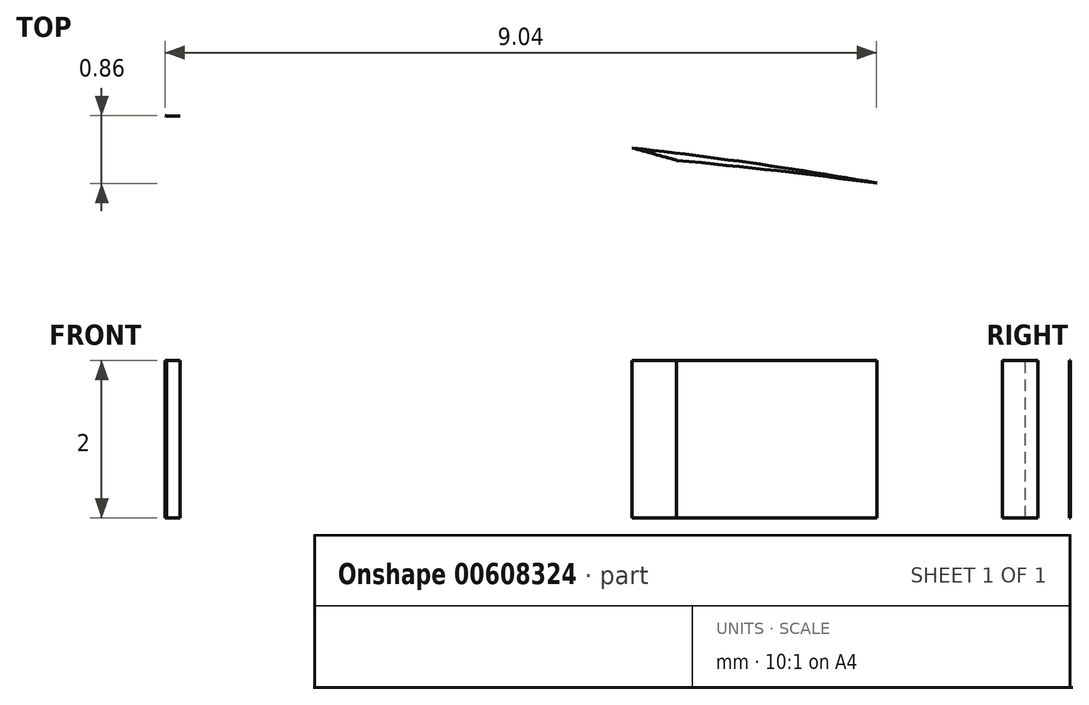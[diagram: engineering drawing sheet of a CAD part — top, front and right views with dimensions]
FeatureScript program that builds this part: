
annotation { "Feature Type Name" : "Feature", "Feature Type Description" : "" }
export const myFeature = defineFeature(function(context is Context, id is Id, definition is map)
    precondition{}
    {
        {
            var Q0;
            Q0=qCreatedBy(makeId("Top.planeOp"),FACE);
            var sketch = newSketch(context, id + "F0", { "sketchPlane" : qUnion([Q0])});
            skFitSpline(sketch, "E0", {"points": [v(-12.37, -64.8) * mm, v(-14.42, -64.57) * mm, v(-15.26, -64.38) * mm, v(-16.13, -63.98) * mm]});
            skFitSpline(sketch, "E1", {"points": [v(-16.13, -63.98) * mm, v(-17.35, -63.42) * mm, v(-19.53, -61.11) * mm, v(-21, -58.82) * mm]});
            skFitSpline(sketch, "E2", {"points": [v(-21, -58.82) * mm, v(-21.68, -57.77) * mm, v(-24.63, -53.13) * mm, v(-27.56, -48.51) * mm]});
            skFitSpline(sketch, "E3", {"points": [v(-33.46, -32.34) * mm, v(-34.25, -21.46) * mm, v(-34.5, -18.5) * mm, v(-34.87, -16.5) * mm]});
            skFitSpline(sketch, "E4", {"points": [v(-34.87, -16.5) * mm, v(-35.26, -14.33) * mm, v(-35.89, -11.88) * mm, v(-36.54, -9.98) * mm]});
            skFitSpline(sketch, "E5", {"points": [v(-36.54, -9.98) * mm, v(-36.87, -9.01) * mm, v(-37.03, -8.22) * mm, v(-37.03, -7.54) * mm]});
            skFitSpline(sketch, "E6", {"points": [v(-37.03, -7.54) * mm, v(-37.03, -6.71) * mm, v(-37.14, -6.31) * mm, v(-37.6, -5.39) * mm]});
            skFitSpline(sketch, "E7", {"points": [v(-37.6, -5.39) * mm, v(-39.55, -1.57) * mm, v(-40.93, 5.83) * mm, v(-40.92, 12.33) * mm]});
            skFitSpline(sketch, "E8", {"points": [v(-40.92, 12.33) * mm, v(-40.92, 15.03) * mm, v(-40.86, 15.87) * mm, v(-40.56, 17.29) * mm]});
            skFitSpline(sketch, "E9", {"points": [v(-40.56, 17.29) * mm, v(-39.91, 20.3) * mm, v(-39, 22.4) * mm, v(-37.7, 23.92) * mm]});
            skLineSegment(sketch, "E10", {"start": v(-27.56, -48.51) * mm, "end": v(-32.9, -40.1) * mm});
            skLineSegment(sketch, "E11", {"start": v(-32.9, -40.1) * mm, "end": v(-33.46, -32.34) * mm});
            skFitSpline(sketch, "E12", {"points": [v(-36.97, 26.7) * mm, v(-36.91, 27.82) * mm, v(-36.79, 32.12) * mm, v(-36.7, 36.25) * mm]});
            skFitSpline(sketch, "E13", {"points": [v(-36.7, 36.25) * mm, v(-36.5, 44.48) * mm, v(-36.48, 44.88) * mm, v(-36.03, 46.58) * mm]});
            skFitSpline(sketch, "E14", {"points": [v(-36.03, 46.58) * mm, v(-34, 54.2) * mm, v(-25.6, 60.7) * mm, v(-14.03, 63.58) * mm]});
            skFitSpline(sketch, "E15", {"points": [v(-14.03, 63.58) * mm, v(-9.87, 64.61) * mm, v(-6.05, 65) * mm, v(0.05, 65) * mm]});
            skFitSpline(sketch, "E16", {"points": [v(0.05, 65) * mm, v(7.64, 65) * mm, v(12.07, 64.37) * mm, v(17.71, 62.49) * mm]});
            skFitSpline(sketch, "E17", {"points": [v(17.71, 62.49) * mm, v(23.1, 60.7) * mm, v(27.42, 58.2) * mm, v(30.77, 54.93) * mm]});
            skFitSpline(sketch, "E18", {"points": [v(30.77, 54.93) * mm, v(33.12, 52.64) * mm, v(34.58, 50.51) * mm, v(35.53, 47.98) * mm]});
            skFitSpline(sketch, "E19", {"points": [v(35.53, 47.98) * mm, v(36.33, 45.85) * mm, v(36.44, 44.7) * mm, v(36.63, 36.91) * mm]});
            skFitSpline(sketch, "E20", {"points": [v(36.63, 36.91) * mm, v(36.72, 32.88) * mm, v(36.84, 28.48) * mm, v(36.9, 27.14) * mm]});
            skLineSegment(sketch, "E21", {"start": v(-37.7, 23.92) * mm, "end": v(-37.07, 24.64) * mm});
            skLineSegment(sketch, "E22", {"start": v(-37.07, 24.64) * mm, "end": v(-36.97, 26.7) * mm});
            skFitSpline(sketch, "E23", {"points": [v(37.74, 23.8) * mm, v(40.15, 20.9) * mm, v(41.27, 15.81) * mm, v(40.83, 9.7) * mm]});
            skFitSpline(sketch, "E24", {"points": [v(40.83, 9.7) * mm, v(40.37, 3.3) * mm, v(39.2, -2.14) * mm, v(37.55, -5.4) * mm]});
            skFitSpline(sketch, "E25", {"points": [v(37.55, -5.4) * mm, v(37.07, -6.35) * mm, v(36.96, -6.75) * mm, v(36.96, -7.58) * mm]});
            skFitSpline(sketch, "E26", {"points": [v(36.96, -7.58) * mm, v(36.96, -8.28) * mm, v(36.8, -9.07) * mm, v(36.46, -10.1) * mm]});
            skFitSpline(sketch, "E27", {"points": [v(36.46, -10.1) * mm, v(35.83, -11.95) * mm, v(35.07, -14.94) * mm, v(34.73, -16.92) * mm]});
            skFitSpline(sketch, "E28", {"points": [v(34.73, -16.92) * mm, v(34.48, -18.3) * mm, v(33.93, -24.93) * mm, v(33.16, -35.76) * mm]});
            skLineSegment(sketch, "E29", {"start": v(36.9, 27.14) * mm, "end": v(37, 24.7) * mm});
            skLineSegment(sketch, "E30", {"start": v(37, 24.7) * mm, "end": v(37.74, 23.8) * mm});
            skFitSpline(sketch, "E31", {"points": [v(27.67, -48.26) * mm, v(19.52, -61.11) * mm, v(19.87, -60.6) * mm, v(18.22, -62.25) * mm]});
            skFitSpline(sketch, "E32", {"points": [v(18.22, -62.25) * mm, v(16.5, -63.98) * mm, v(15.65, -64.4) * mm, v(13.38, -64.7) * mm]});
            skFitSpline(sketch, "E33", {"points": [v(13.38, -64.7) * mm, v(11.7, -64.91) * mm, v(-10.67, -65) * mm, v(-12.37, -64.8) * mm]});
            skLineSegment(sketch, "E34", {"start": v(33.16, -35.76) * mm, "end": v(32.84, -40.1) * mm});
            skLineSegment(sketch, "E35", {"start": v(32.84, -40.1) * mm, "end": v(27.67, -48.26) * mm});
            skFitSpline(sketch, "E36", {"points": [v(11.8, -61.94) * mm, v(14.15, -61.52) * mm, v(14.92, -61.22) * mm, v(15.85, -60.35) * mm]});
            skFitSpline(sketch, "E37", {"points": [v(15.85, -60.35) * mm, v(17, -59.27) * mm, v(17.39, -58.7) * mm, v(23.96, -48.34) * mm]});
            skFitSpline(sketch, "E38", {"points": [v(30.23, -33.5) * mm, v(30.46, -30.43) * mm, v(30.74, -26.57) * mm, v(30.87, -24.92) * mm]});
            skFitSpline(sketch, "E39", {"points": [v(30.87, -24.92) * mm, v(31, -23.27) * mm, v(31.08, -21.9) * mm, v(31.06, -21.87) * mm]});
            skFitSpline(sketch, "E40", {"points": [v(31.06, -21.87) * mm, v(31.03, -21.85) * mm, v(30.73, -22.29) * mm, v(30.39, -22.85) * mm]});
            skFitSpline(sketch, "E41", {"points": [v(30.39, -22.85) * mm, v(30.04, -23.4) * mm, v(28.89, -25.08) * mm, v(27.83, -26.56) * mm]});
            skFitSpline(sketch, "E42", {"points": [v(27.83, -26.56) * mm, v(24.27, -31.52) * mm, v(22.79, -34.32) * mm, v(20.88, -39.66) * mm]});
            skLineSegment(sketch, "E43", {"start": v(23.96, -48.34) * mm, "end": v(29.83, -39.1) * mm});
            skLineSegment(sketch, "E44", {"start": v(29.83, -39.1) * mm, "end": v(30.23, -33.5) * mm});
            skFitSpline(sketch, "E45", {"points": [v(20.7, -43.9) * mm, v(20.94, -45.29) * mm, v(21.14, -46.67) * mm, v(21.14, -46.98) * mm]});
            skFitSpline(sketch, "E46", {"points": [v(21.14, -46.98) * mm, v(21.13, -48) * mm, v(18.6, -53.5) * mm, v(17.35, -55.2) * mm]});
            skFitSpline(sketch, "E47", {"points": [v(17.35, -55.2) * mm, v(16.02, -57.02) * mm, v(14.23, -57.14) * mm, v(9.94, -55.72) * mm]});
            skFitSpline(sketch, "E48", {"points": [v(9.94, -55.72) * mm, v(9.7, -55.65) * mm, v(9.57, -55.9) * mm, v(9.2, -57.09) * mm]});
            skFitSpline(sketch, "E49", {"points": [v(9.2, -57.09) * mm, v(8.95, -57.94) * mm, v(8.6, -58.71) * mm, v(8.37, -58.94) * mm]});
            skLineSegment(sketch, "E50", {"start": v(20.88, -39.66) * mm, "end": v(20.26, -41.4) * mm});
            skLineSegment(sketch, "E51", {"start": v(20.26, -41.4) * mm, "end": v(20.7, -43.9) * mm});
            skFitSpline(sketch, "E52", {"points": [v(-8.42, -58.95) * mm, v(-8.63, -58.74) * mm, v(-9, -57.92) * mm, v(-9.26, -57.1) * mm]});
            skFitSpline(sketch, "E53", {"points": [v(-9.26, -57.1) * mm, v(-9.64, -55.9) * mm, v(-9.77, -55.65) * mm, v(-10, -55.72) * mm]});
            skFitSpline(sketch, "E54", {"points": [v(-10, -55.72) * mm, v(-12.14, -56.43) * mm, v(-13.2, -56.66) * mm, v(-14.3, -56.66) * mm]});
            skFitSpline(sketch, "E55", {"points": [v(-14.3, -56.66) * mm, v(-15.94, -56.66) * mm, v(-16.64, -56.3) * mm, v(-17.5, -55.04) * mm]});
            skFitSpline(sketch, "E56", {"points": [v(-17.5, -55.04) * mm, v(-18.27, -53.9) * mm, v(-19.78, -50.93) * mm, v(-20.63, -48.9) * mm]});
            skFitSpline(sketch, "E57", {"points": [v(-20.63, -48.9) * mm, v(-21.32, -47.22) * mm, v(-21.32, -47.02) * mm, v(-20.7, -43.5) * mm]});
            skLineSegment(sketch, "E58", {"start": v(8.37, -58.94) * mm, "end": v(7.98, -59.33) * mm});
            skLineSegment(sketch, "E59", {"start": v(7.98, -59.33) * mm, "end": v(-0.03, -59.33) * mm});
            skLineSegment(sketch, "E60", {"start": v(-0.03, -59.33) * mm, "end": v(-8.05, -59.33) * mm});
            skLineSegment(sketch, "E61", {"start": v(-8.05, -59.33) * mm, "end": v(-8.42, -58.95) * mm});
            skFitSpline(sketch, "E62", {"points": [v(-21.19, -38.91) * mm, v(-22.53, -35.33) * mm, v(-24.6, -31.2) * mm, v(-26.06, -29.25) * mm]});
            skFitSpline(sketch, "E63", {"points": [v(-26.06, -29.25) * mm, v(-26.74, -28.33) * mm, v(-28.15, -26.3) * mm, v(-29.2, -24.72) * mm]});
            skFitSpline(sketch, "E64", {"points": [v(-29.2, -24.72) * mm, v(-30.25, -23.14) * mm, v(-31.11, -21.86) * mm, v(-31.13, -21.88) * mm]});
            skFitSpline(sketch, "E65", {"points": [v(-31.13, -21.88) * mm, v(-31.24, -22.03) * mm, v(-29.85, -39.05) * mm, v(-29.7, -39.33) * mm]});
            skFitSpline(sketch, "E66", {"points": [v(-29.7, -39.33) * mm, v(-29.45, -39.8) * mm, v(-18.29, -57.39) * mm, v(-17.67, -58.29) * mm]});
            skFitSpline(sketch, "E67", {"points": [v(-17.67, -58.29) * mm, v(-17.4, -58.67) * mm, v(-16.77, -59.44) * mm, v(-16.27, -59.99) * mm]});
            skFitSpline(sketch, "E68", {"points": [v(-16.27, -59.99) * mm, v(-15.16, -61.18) * mm, v(-14.38, -61.51) * mm, v(-11.86, -61.9) * mm]});
            skFitSpline(sketch, "E69", {"points": [v(-11.86, -61.9) * mm, v(-9.22, -62.3) * mm, v(-9.42, -62.29) * mm, v(0.72, -62.25) * mm]});
            skFitSpline(sketch, "E70", {"points": [v(0.72, -62.25) * mm, v(8.81, -62.23) * mm, v(10.45, -62.18) * mm, v(11.8, -61.94) * mm]});
            skLineSegment(sketch, "E71", {"start": v(-20.7, -43.5) * mm, "end": v(-20.32, -41.25) * mm});
            skLineSegment(sketch, "E72", {"start": v(-20.32, -41.25) * mm, "end": v(-21.19, -38.91) * mm});
            skFitSpline(sketch, "E73", {"points": [v(6.4, -55.75) * mm, v(6.52, -55.43) * mm, v(6.63, -55.13) * mm, v(6.63, -55.09) * mm]});
            skFitSpline(sketch, "E74", {"points": [v(6.63, -55.09) * mm, v(6.63, -55.04) * mm, v(3.64, -55) * mm, v(-0.02, -55) * mm]});
            skFitSpline(sketch, "E75", {"points": [v(-6.53, -55.5) * mm, v(-6.46, -55.76) * mm, v(-6.34, -56.06) * mm, v(-6.29, -56.16) * mm]});
            skFitSpline(sketch, "E76", {"points": [v(-6.29, -56.16) * mm, v(-6.22, -56.27) * mm, v(-4.07, -56.33) * mm, v(-0.01, -56.33) * mm]});
            skLineSegment(sketch, "E77", {"start": v(-0.02, -55) * mm, "end": v(-6.68, -55) * mm});
            skLineSegment(sketch, "E78", {"start": v(-6.68, -55) * mm, "end": v(-6.53, -55.5) * mm});
            skFitSpline(sketch, "E79", {"points": [v(-12.22, -53.17) * mm, v(-11.45, -52.9) * mm, v(-10.75, -52.61) * mm, v(-10.66, -52.52) * mm]});
            skFitSpline(sketch, "E80", {"points": [v(-10.66, -52.52) * mm, v(-10.49, -52.35) * mm, v(-11.45, -48.42) * mm, v(-11.74, -48.08) * mm]});
            skFitSpline(sketch, "E81", {"points": [v(-11.74, -48.08) * mm, v(-11.83, -47.98) * mm, v(-12.1, -48.17) * mm, v(-12.46, -48.61) * mm]});
            skFitSpline(sketch, "E82", {"points": [v(-12.46, -48.61) * mm, v(-13.19, -49.48) * mm, v(-14, -50) * mm, v(-14.66, -50) * mm]});
            skFitSpline(sketch, "E83", {"points": [v(-14.66, -50) * mm, v(-15.3, -50) * mm, v(-15.83, -49.4) * mm, v(-16.95, -47.46) * mm]});
            skFitSpline(sketch, "E84", {"points": [v(-16.95, -47.46) * mm, v(-17.4, -46.65) * mm, v(-17.83, -46) * mm, v(-17.89, -46) * mm]});
            skFitSpline(sketch, "E85", {"points": [v(-17.89, -46) * mm, v(-18.42, -46) * mm, v(-17.67, -48.27) * mm, v(-16.13, -51.33) * mm]});
            skFitSpline(sketch, "E86", {"points": [v(-16.13, -51.33) * mm, v(-15.13, -53.31) * mm, v(-14.84, -53.66) * mm, v(-14.2, -53.66) * mm]});
            skFitSpline(sketch, "E87", {"points": [v(-14.2, -53.66) * mm, v(-13.88, -53.66) * mm, v(-12.99, -53.44) * mm, v(-12.22, -53.17) * mm]});
            skLineSegment(sketch, "E88", {"start": v(-0.01, -56.33) * mm, "end": v(6.15, -56.33) * mm});
            skLineSegment(sketch, "E89", {"start": v(6.15, -56.33) * mm, "end": v(6.4, -55.75) * mm});
            skFitSpline(sketch, "E90", {"points": [v(15.16, -52.96) * mm, v(16.4, -50.95) * mm, v(18.16, -46.9) * mm, v(18.02, -46.36) * mm]});
            skFitSpline(sketch, "E91", {"points": [v(18.02, -46.36) * mm, v(17.97, -46.16) * mm, v(17.88, -46) * mm, v(17.82, -46) * mm]});
            skFitSpline(sketch, "E92", {"points": [v(17.82, -46) * mm, v(17.76, -46) * mm, v(17.35, -46.65) * mm, v(16.9, -47.43) * mm]});
            skFitSpline(sketch, "E93", {"points": [v(16.9, -47.43) * mm, v(15.79, -49.4) * mm, v(15.24, -50) * mm, v(14.56, -50) * mm]});
            skFitSpline(sketch, "E94", {"points": [v(14.56, -50) * mm, v(13.97, -50) * mm, v(13.06, -49.38) * mm, v(12.27, -48.44) * mm]});
            skFitSpline(sketch, "E95", {"points": [v(12.27, -48.44) * mm, v(11.98, -48.1) * mm, v(11.77, -47.97) * mm, v(11.67, -48.08) * mm]});
            skFitSpline(sketch, "E96", {"points": [v(11.67, -48.08) * mm, v(11.55, -48.22) * mm, v(10.83, -50.7) * mm, v(10.51, -52.12) * mm]});
            skFitSpline(sketch, "E97", {"points": [v(10.51, -52.12) * mm, v(10.42, -52.55) * mm, v(10.9, -52.81) * mm, v(12.72, -53.35) * mm]});
            skFitSpline(sketch, "E98", {"points": [v(12.72, -53.35) * mm, v(14.35, -53.83) * mm, v(14.65, -53.78) * mm, v(15.16, -52.96) * mm]});
            skFitSpline(sketch, "E99", {"points": [v(7.59, -51.12) * mm, v(7.68, -50.73) * mm, v(8, -49.55) * mm, v(8.28, -48.5) * mm]});
            skFitSpline(sketch, "E100", {"points": [v(8.28, -48.5) * mm, v(8.56, -47.44) * mm, v(8.8, -46.56) * mm, v(8.8, -46.54) * mm]});
            skFitSpline(sketch, "E101", {"points": [v(8.8, -46.54) * mm, v(8.8, -46.52) * mm, v(4.82, -46.5) * mm, v(-0.05, -46.5) * mm]});
            skFitSpline(sketch, "E102", {"points": [v(-0.05, -46.5) * mm, v(-7.06, -46.5) * mm, v(-8.89, -46.54) * mm, v(-8.83, -46.7) * mm]});
            skFitSpline(sketch, "E103", {"points": [v(-8.83, -46.7) * mm, v(-8.8, -46.82) * mm, v(-8.46, -48.02) * mm, v(-8.1, -49.37) * mm]});
            skLineSegment(sketch, "E104", {"start": v(-8.1, -49.37) * mm, "end": v(-7.45, -51.83) * mm});
            skLineSegment(sketch, "E105", {"start": v(-7.45, -51.83) * mm, "end": v(-0.02, -51.83) * mm});
            skLineSegment(sketch, "E106", {"start": v(-0.02, -51.83) * mm, "end": v(7.41, -51.83) * mm});
            skLineSegment(sketch, "E107", {"start": v(7.41, -51.83) * mm, "end": v(7.59, -51.12) * mm});
            skFitSpline(sketch, "E108", {"points": [v(-13.31, -43.77) * mm, v(-14.02, -42.38) * mm, v(-14.97, -41.07) * mm, v(-16.41, -39.53) * mm]});
            skFitSpline(sketch, "E109", {"points": [v(-16.41, -39.53) * mm, v(-18.41, -37.4) * mm, v(-18.43, -37.39) * mm, v(-17.83, -39.2) * mm]});
            skFitSpline(sketch, "E110", {"points": [v(-17.83, -39.2) * mm, v(-17.5, -40.18) * mm, v(-16.78, -41.64) * mm, v(-15.82, -43.28) * mm]});
            skFitSpline(sketch, "E111", {"points": [v(-15.82, -43.28) * mm, v(-15, -44.68) * mm, v(-14.28, -45.83) * mm, v(-14.23, -45.83) * mm]});
            skFitSpline(sketch, "E112", {"points": [v(-14.23, -45.83) * mm, v(-14.17, -45.83) * mm, v(-13.85, -45.56) * mm, v(-13.5, -45.22) * mm]});
            skLineSegment(sketch, "E113", {"start": v(-13.5, -45.22) * mm, "end": v(-12.88, -44.62) * mm});
            skLineSegment(sketch, "E114", {"start": v(-12.88, -44.62) * mm, "end": v(-13.31, -43.77) * mm});
            skFitSpline(sketch, "E115", {"points": [v(15.75, -43.29) * mm, v(16.68, -41.71) * mm, v(17.45, -40.16) * mm, v(17.78, -39.19) * mm]});
            skFitSpline(sketch, "E116", {"points": [v(17.78, -39.19) * mm, v(18.08, -38.33) * mm, v(18.29, -37.6) * mm, v(18.25, -37.56) * mm]});
            skFitSpline(sketch, "E117", {"points": [v(18.25, -37.56) * mm, v(18.14, -37.45) * mm, v(14.96, -41.02) * mm, v(14.3, -42) * mm]});
            skFitSpline(sketch, "E118", {"points": [v(14.3, -42) * mm, v(13.58, -43.06) * mm, v(12.97, -44.23) * mm, v(12.97, -44.53) * mm]});
            skFitSpline(sketch, "E119", {"points": [v(12.97, -44.53) * mm, v(12.97, -44.74) * mm, v(13.95, -45.83) * mm, v(14.15, -45.83) * mm]});
            skFitSpline(sketch, "E120", {"points": [v(14.15, -45.83) * mm, v(14.2, -45.83) * mm, v(14.93, -44.69) * mm, v(15.75, -43.29) * mm]});
            skFitSpline(sketch, "E121", {"points": [v(10.61, -42.12) * mm, v(11.7, -40.15) * mm, v(12.9, -38.67) * mm, v(16.57, -34.8) * mm]});
            skFitSpline(sketch, "E122", {"points": [v(16.57, -34.8) * mm, v(21.04, -30.07) * mm, v(22.06, -28.95) * mm, v(23.68, -26.92) * mm]});
            skFitSpline(sketch, "E123", {"points": [v(23.68, -26.92) * mm, v(26.76, -23.08) * mm, v(27.13, -21.96) * mm, v(27.47, -15.42) * mm]});
            skFitSpline(sketch, "E124", {"points": [v(27.47, -15.42) * mm, v(27.56, -13.67) * mm, v(27.68, -11.74) * mm, v(27.74, -11.13) * mm]});
            skFitSpline(sketch, "E125", {"points": [v(27.2, -10.61) * mm, v(25.5, -12.21) * mm, v(23.11, -13.58) * mm, v(20.55, -14.4) * mm]});
            skFitSpline(sketch, "E126", {"points": [v(20.55, -14.4) * mm, v(18.94, -14.92) * mm, v(11.85, -16.35) * mm, v(10.8, -16.37) * mm]});
            skFitSpline(sketch, "E127", {"points": [v(10.8, -16.37) * mm, v(10.1, -16.39) * mm, v(10.01, -16.33) * mm, v(9.14, -15.38) * mm]});
            skFitSpline(sketch, "E128", {"points": [v(9.14, -15.38) * mm, v(8.4, -14.57) * mm, v(7.14, -12.74) * mm, v(6.93, -12.14) * mm]});
            skFitSpline(sketch, "E129", {"points": [v(6.93, -12.14) * mm, v(6.9, -12.08) * mm, v(6.38, -12.13) * mm, v(5.77, -12.26) * mm]});
            skFitSpline(sketch, "E130", {"points": [v(5.77, -12.26) * mm, v(4.04, -12.62) * mm, v(0.4, -12.86) * mm, v(-1.53, -12.75) * mm]});
            skFitSpline(sketch, "E131", {"points": [v(-1.53, -12.75) * mm, v(-3.14, -12.65) * mm, v(-6.09, -12.27) * mm, v(-6.7, -12.08) * mm]});
            skFitSpline(sketch, "E132", {"points": [v(-6.7, -12.08) * mm, v(-6.89, -12.02) * mm, v(-7.08, -12.24) * mm, v(-7.34, -12.78) * mm]});
            skFitSpline(sketch, "E133", {"points": [v(-7.34, -12.78) * mm, v(-7.77, -13.65) * mm, v(-8.9, -15.17) * mm, v(-9.68, -15.9) * mm]});
            skFitSpline(sketch, "E134", {"points": [v(-9.68, -15.9) * mm, v(-10.09, -16.29) * mm, v(-10.33, -16.38) * mm, v(-10.9, -16.37) * mm]});
            skFitSpline(sketch, "E135", {"points": [v(-10.9, -16.37) * mm, v(-11.92, -16.35) * mm, v(-19.03, -14.9) * mm, v(-20.61, -14.4) * mm]});
            skFitSpline(sketch, "E136", {"points": [v(-20.61, -14.4) * mm, v(-23.23, -13.56) * mm, v(-25.65, -12.17) * mm, v(-27.27, -10.57) * mm]});
            skLineSegment(sketch, "E137", {"start": v(27.74, -11.13) * mm, "end": v(27.84, -10) * mm});
            skLineSegment(sketch, "E138", {"start": v(27.84, -10) * mm, "end": v(27.2, -10.61) * mm});
            skFitSpline(sketch, "E139", {"points": [v(-27.8, -11) * mm, v(-27.75, -11.6) * mm, v(-27.63, -13.43) * mm, v(-27.54, -15.08) * mm]});
            skFitSpline(sketch, "E140", {"points": [v(-27.54, -15.08) * mm, v(-27.32, -19.1) * mm, v(-27.22, -20.04) * mm, v(-26.86, -21.44) * mm]});
            skFitSpline(sketch, "E141", {"points": [v(-26.86, -21.44) * mm, v(-26.45, -23.05) * mm, v(-26, -23.9) * mm, v(-24.1, -26.58) * mm]});
            skFitSpline(sketch, "E142", {"points": [v(-24.1, -26.58) * mm, v(-22.75, -28.48) * mm, v(-21.68, -29.69) * mm, v(-17.9, -33.56) * mm]});
            skFitSpline(sketch, "E143", {"points": [v(-17.9, -33.56) * mm, v(-13.18, -38.4) * mm, v(-11.84, -39.99) * mm, v(-10.68, -42.1) * mm]});
            skLineSegment(sketch, "E144", {"start": v(-27.27, -10.57) * mm, "end": v(-27.92, -9.93) * mm});
            skLineSegment(sketch, "E145", {"start": v(-27.92, -9.93) * mm, "end": v(-27.8, -11) * mm});
            skFitSpline(sketch, "E146", {"points": [v(-30.6, -14.37) * mm, v(-30.66, -13.76) * mm, v(-30.8, -12.5) * mm, v(-30.9, -11.58) * mm]});
            skFitSpline(sketch, "E147", {"points": [v(-30.9, -11.58) * mm, v(-31.2, -8.73) * mm, v(-30.6, -4.2) * mm, v(-29.27, 0.6) * mm]});
            skLineSegment(sketch, "E148", {"start": v(-10.68, -42.1) * mm, "end": v(-10, -43.33) * mm});
            skLineSegment(sketch, "E149", {"start": v(-10, -43.33) * mm, "end": v(-0.03, -43.33) * mm});
            skLineSegment(sketch, "E150", {"start": v(-0.03, -43.33) * mm, "end": v(9.94, -43.33) * mm});
            skLineSegment(sketch, "E151", {"start": v(9.94, -43.33) * mm, "end": v(10.61, -42.12) * mm});
            skFitSpline(sketch, "E152", {"points": [v(-28.75, 11.08) * mm, v(-28.82, 19.6) * mm, v(-28.88, 20.42) * mm, v(-29.61, 24.66) * mm]});
            skFitSpline(sketch, "E153", {"points": [v(-29.61, 24.66) * mm, v(-29.76, 25.53) * mm, v(-29.92, 26.28) * mm, v(-29.96, 26.32) * mm]});
            skFitSpline(sketch, "E154", {"points": [v(-29.96, 26.32) * mm, v(-30, 26.35) * mm, v(-30.03, 21.26) * mm, v(-30.03, 14.99) * mm]});
            skLineSegment(sketch, "E155", {"start": v(-29.27, 0.6) * mm, "end": v(-28.68, 2.75) * mm});
            skLineSegment(sketch, "E156", {"start": v(-28.68, 2.75) * mm, "end": v(-28.75, 11.08) * mm});
            skFitSpline(sketch, "E157", {"points": [v(-32.19, -12.3) * mm, v(-31.53, -13.74) * mm, v(-30.96, -15.05) * mm, v(-30.91, -15.2) * mm]});
            skFitSpline(sketch, "E158", {"points": [v(-30.91, -15.2) * mm, v(-30.86, -15.37) * mm, v(-30.75, -15.5) * mm, v(-30.66, -15.5) * mm]});
            skFitSpline(sketch, "E159", {"points": [v(-30.66, -15.5) * mm, v(-30.57, -15.5) * mm, v(-30.55, -15.06) * mm, v(-30.6, -14.37) * mm]});
            skLineSegment(sketch, "E160", {"start": v(-30.03, 14.99) * mm, "end": v(-30.03, 3.59) * mm});
            skLineSegment(sketch, "E161", {"start": v(-30.03, 3.59) * mm, "end": v(-31.7, -3.04) * mm});
            skLineSegment(sketch, "E162", {"start": v(-31.7, -3.04) * mm, "end": v(-33.37, -9.67) * mm});
            skLineSegment(sketch, "E163", {"start": v(-33.37, -9.67) * mm, "end": v(-32.19, -12.3) * mm});
            skFitSpline(sketch, "E164", {"points": [v(31.1, -14.7) * mm, v(31.28, -14.27) * mm, v(31.85, -12.96) * mm, v(32.37, -11.78) * mm]});
            skFitSpline(sketch, "E165", {"points": [v(29.97, 14.75) * mm, v(29.87, 27.47) * mm, v(29.9, 27.25) * mm, v(29.1, 21.75) * mm]});
            skFitSpline(sketch, "E166", {"points": [v(29.1, 21.75) * mm, v(28.8, 19.72) * mm, v(28.75, 18.33) * mm, v(28.68, 11.2) * mm]});
            skLineSegment(sketch, "E167", {"start": v(32.37, -11.78) * mm, "end": v(33.3, -9.65) * mm});
            skLineSegment(sketch, "E168", {"start": v(33.3, -9.65) * mm, "end": v(31.67, -3.28) * mm});
            skLineSegment(sketch, "E169", {"start": v(31.67, -3.28) * mm, "end": v(30.05, 3.08) * mm});
            skLineSegment(sketch, "E170", {"start": v(30.05, 3.08) * mm, "end": v(29.97, 14.75) * mm});
            skFitSpline(sketch, "E171", {"points": [v(29.36, 0.04) * mm, v(30.67, -5.06) * mm, v(31.13, -8.85) * mm, v(30.82, -11.93) * mm]});
            skFitSpline(sketch, "E172", {"points": [v(30.82, -11.93) * mm, v(30.48, -15.23) * mm, v(30.46, -15.5) * mm, v(30.6, -15.5) * mm]});
            skFitSpline(sketch, "E173", {"points": [v(30.6, -15.5) * mm, v(30.69, -15.5) * mm, v(30.9, -15.14) * mm, v(31.1, -14.7) * mm]});
            skLineSegment(sketch, "E174", {"start": v(28.68, 11.2) * mm, "end": v(28.6, 3) * mm});
            skLineSegment(sketch, "E175", {"start": v(28.6, 3) * mm, "end": v(29.36, 0.04) * mm});
            skFitSpline(sketch, "E176", {"points": [v(-10.54, -12.14) * mm, v(-10.16, -11.58) * mm, v(-9.88, -11.03) * mm, v(-9.91, -10.93) * mm]});
            skFitSpline(sketch, "E177", {"points": [v(-9.91, -10.93) * mm, v(-10, -10.66) * mm, v(-13.72, -8.62) * mm, v(-18.87, -6.03) * mm]});
            skFitSpline(sketch, "E178", {"points": [v(-18.87, -6.03) * mm, v(-25.42, -2.72) * mm, v(-26.18, -2.38) * mm, v(-26.39, -2.68) * mm]});
            skFitSpline(sketch, "E179", {"points": [v(-26.39, -2.68) * mm, v(-26.63, -3.04) * mm, v(-26.46, -6.14) * mm, v(-26.15, -6.87) * mm]});
            skFitSpline(sketch, "E180", {"points": [v(-26.15, -6.87) * mm, v(-26, -7.21) * mm, v(-25.67, -7.76) * mm, v(-25.42, -8.08) * mm]});
            skFitSpline(sketch, "E181", {"points": [v(-25.42, -8.08) * mm, v(-24.48, -9.26) * mm, v(-21.81, -10.82) * mm, v(-19.57, -11.5) * mm]});
            skFitSpline(sketch, "E182", {"points": [v(-19.57, -11.5) * mm, v(-18.25, -11.9) * mm, v(-12.38, -13.13) * mm, v(-11.67, -13.15) * mm]});
            skFitSpline(sketch, "E183", {"points": [v(-11.67, -13.15) * mm, v(-11.3, -13.16) * mm, v(-11.1, -12.98) * mm, v(-10.54, -12.14) * mm]});
            skFitSpline(sketch, "E184", {"points": [v(15.08, -12.5) * mm, v(16.9, -12.14) * mm, v(18.92, -11.69) * mm, v(19.56, -11.5) * mm]});
            skFitSpline(sketch, "E185", {"points": [v(19.56, -11.5) * mm, v(21.35, -10.94) * mm, v(23.88, -9.55) * mm, v(24.88, -8.56) * mm]});
            skFitSpline(sketch, "E186", {"points": [v(24.88, -8.56) * mm, v(26.1, -7.37) * mm, v(26.38, -6.55) * mm, v(26.38, -4.33) * mm]});
            skFitSpline(sketch, "E187", {"points": [v(25.97, -2.63) * mm, v(25.46, -2.68) * mm, v(15.09, -7.83) * mm, v(12.06, -9.54) * mm]});
            skFitSpline(sketch, "E188", {"points": [v(12.06, -9.54) * mm, v(10.87, -10.2) * mm, v(9.88, -10.83) * mm, v(9.85, -10.93) * mm]});
            skFitSpline(sketch, "E189", {"points": [v(9.85, -10.93) * mm, v(9.75, -11.25) * mm, v(11.14, -13.17) * mm, v(11.47, -13.17) * mm]});
            skFitSpline(sketch, "E190", {"points": [v(11.47, -13.17) * mm, v(11.64, -13.17) * mm, v(13.26, -12.87) * mm, v(15.08, -12.5) * mm]});
            skLineSegment(sketch, "E191", {"start": v(26.38, -4.33) * mm, "end": v(26.38, -2.58) * mm});
            skLineSegment(sketch, "E192", {"start": v(26.38, -2.58) * mm, "end": v(25.97, -2.63) * mm});
            skFitSpline(sketch, "E193", {"points": [v(3.38, -9.5) * mm, v(5.87, -9.21) * mm, v(6.98, -8.81) * mm, v(10.3, -7) * mm]});
            skFitSpline(sketch, "E194", {"points": [v(10.3, -7) * mm, v(14.24, -4.83) * mm, v(20.02, -1.89) * mm, v(23.22, -0.42) * mm]});
            skFitSpline(sketch, "E195", {"points": [v(23.22, -0.42) * mm, v(24.6, 0.21) * mm, v(25.77, 0.77) * mm, v(25.83, 0.82) * mm]});
            skFitSpline(sketch, "E196", {"points": [v(25.83, 0.82) * mm, v(25.9, 0.87) * mm, v(25.83, 1.33) * mm, v(25.7, 1.83) * mm]});
            skFitSpline(sketch, "E197", {"points": [v(25.7, 1.83) * mm, v(25.35, 3.11) * mm, v(25.47, 17.14) * mm, v(25.86, 20.51) * mm]});
            skFitSpline(sketch, "E198", {"points": [v(25.86, 20.51) * mm, v(26.5, 26) * mm, v(27.66, 31.66) * mm, v(29.15, 36.55) * mm]});
            skFitSpline(sketch, "E199", {"points": [v(29.15, 36.55) * mm, v(29.43, 37.46) * mm, v(29.63, 38.22) * mm, v(29.6, 38.26) * mm]});
            skFitSpline(sketch, "E200", {"points": [v(29.6, 38.26) * mm, v(29.56, 38.29) * mm, v(27.78, 39.18) * mm, v(25.63, 40.23) * mm]});
            skFitSpline(sketch, "E201", {"points": [v(25.63, 40.23) * mm, v(20.86, 42.56) * mm, v(17.81, 43.65) * mm, v(14.75, 44.13) * mm]});
            skFitSpline(sketch, "E202", {"points": [v(14.75, 44.13) * mm, v(13.85, 44.27) * mm, v(13.79, 44.26) * mm, v(13.72, 43.93) * mm]});
            skFitSpline(sketch, "E203", {"points": [v(13.72, 43.93) * mm, v(13.68, 43.74) * mm, v(12.93, 36.83) * mm, v(12.04, 28.59) * mm]});
            skFitSpline(sketch, "E204", {"points": [v(12.04, 28.59) * mm, v(11.16, 20.34) * mm, v(10.37, 13.46) * mm, v(10.28, 13.3) * mm]});
            skFitSpline(sketch, "E205", {"points": [v(10.28, 13.3) * mm, v(9.95, 12.68) * mm, v(9.3, 12.5) * mm, v(4.68, 11.83) * mm]});
            skFitSpline(sketch, "E206", {"points": [v(-4.74, 11.83) * mm, v(-9.34, 12.5) * mm, v(-10.02, 12.69) * mm, v(-10.34, 13.3) * mm]});
            skFitSpline(sketch, "E207", {"points": [v(-10.34, 13.3) * mm, v(-10.43, 13.45) * mm, v(-11.22, 20.33) * mm, v(-12.1, 28.58) * mm]});
            skFitSpline(sketch, "E208", {"points": [v(-12.1, 28.58) * mm, v(-12.99, 36.83) * mm, v(-13.74, 43.74) * mm, v(-13.78, 43.93) * mm]});
            skFitSpline(sketch, "E209", {"points": [v(-13.78, 43.93) * mm, v(-13.85, 44.26) * mm, v(-13.92, 44.27) * mm, v(-14.82, 44.13) * mm]});
            skFitSpline(sketch, "E210", {"points": [v(-14.82, 44.13) * mm, v(-16.3, 43.9) * mm, v(-18.18, 43.39) * mm, v(-20.28, 42.64) * mm]});
            skFitSpline(sketch, "E211", {"points": [v(-20.28, 42.64) * mm, v(-22.79, 41.75) * mm, v(-29.62, 38.34) * mm, v(-29.59, 38) * mm]});
            skFitSpline(sketch, "E212", {"points": [v(-29.59, 38) * mm, v(-29.57, 37.86) * mm, v(-29.22, 36.57) * mm, v(-28.8, 35.12) * mm]});
            skFitSpline(sketch, "E213", {"points": [v(-28.8, 35.12) * mm, v(-27.5, 30.62) * mm, v(-26.55, 25.8) * mm, v(-25.93, 20.66) * mm]});
            skFitSpline(sketch, "E214", {"points": [v(-25.93, 20.66) * mm, v(-25.55, 17.53) * mm, v(-25.39, 3.36) * mm, v(-25.72, 2) * mm]});
            skFitSpline(sketch, "E215", {"points": [v(-25.72, 2) * mm, v(-25.84, 1.5) * mm, v(-25.94, 1.03) * mm, v(-25.94, 0.96) * mm]});
            skFitSpline(sketch, "E216", {"points": [v(-25.94, 0.96) * mm, v(-25.95, 0.9) * mm, v(-24.22, 0.02) * mm, v(-22.1, -0.97) * mm]});
            skFitSpline(sketch, "E217", {"points": [v(-22.1, -0.97) * mm, v(-18.46, -2.68) * mm, v(-13.75, -5.1) * mm, v(-9.28, -7.58) * mm]});
            skFitSpline(sketch, "E218", {"points": [v(-9.28, -7.58) * mm, v(-7.16, -8.75) * mm, v(-5.71, -9.25) * mm, v(-3.69, -9.48) * mm]});
            skFitSpline(sketch, "E219", {"points": [v(-3.69, -9.48) * mm, v(-1.92, -9.69) * mm, v(1.63, -9.7) * mm, v(3.38, -9.5) * mm]});
            skLineSegment(sketch, "E220", {"start": v(4.68, 11.83) * mm, "end": v(-0.03, 11.14) * mm});
            skLineSegment(sketch, "E221", {"start": v(-0.03, 11.14) * mm, "end": v(-4.74, 11.83) * mm});
            skFitSpline(sketch, "E222", {"points": [v(-33.06, 21.9) * mm, v(-33.07, 38.9) * mm, v(-33.06, 39.38) * mm, v(-32.74, 39.8) * mm]});
            skFitSpline(sketch, "E223", {"points": [v(-32.74, 39.8) * mm, v(-32.34, 40.36) * mm, v(-25.29, 43.99) * mm, v(-22.34, 45.16) * mm]});
            skFitSpline(sketch, "E224", {"points": [v(-22.34, 45.16) * mm, v(-19.82, 46.16) * mm, v(-16.42, 47.06) * mm, v(-14.08, 47.34) * mm]});
            skFitSpline(sketch, "E225", {"points": [v(-14.08, 47.34) * mm, v(-11.37, 47.67) * mm, v(-11.05, 47.39) * mm, v(-10.72, 44.35) * mm]});
            skFitSpline(sketch, "E226", {"points": [v(-10.72, 44.35) * mm, v(-10.61, 43.4) * mm, v(-10.49, 42.56) * mm, v(-10.44, 42.48) * mm]});
            skFitSpline(sketch, "E227", {"points": [v(-10.44, 42.48) * mm, v(-10.39, 42.4) * mm, v(-5.88, 42.33) * mm, v(-0.02, 42.33) * mm]});
            skFitSpline(sketch, "E228", {"points": [v(-0.02, 42.33) * mm, v(8.1, 42.33) * mm, v(10.33, 42.37) * mm, v(10.39, 42.54) * mm]});
            skFitSpline(sketch, "E229", {"points": [v(10.39, 42.54) * mm, v(10.43, 42.65) * mm, v(10.57, 43.6) * mm, v(10.7, 44.66) * mm]});
            skFitSpline(sketch, "E230", {"points": [v(10.7, 44.66) * mm, v(10.93, 46.48) * mm, v(10.96, 46.6) * mm, v(11.48, 47.05) * mm]});
            skFitSpline(sketch, "E231", {"points": [v(11.48, 47.05) * mm, v(12, 47.53) * mm, v(12.05, 47.53) * mm, v(13.28, 47.42) * mm]});
            skFitSpline(sketch, "E232", {"points": [v(13.28, 47.42) * mm, v(17.65, 47.03) * mm, v(21.35, 45.8) * mm, v(27.73, 42.65) * mm]});
            skFitSpline(sketch, "E233", {"points": [v(27.73, 42.65) * mm, v(32.07, 40.5) * mm, v(32.71, 40.09) * mm, v(32.95, 39.21) * mm]});
            skFitSpline(sketch, "E234", {"points": [v(32.95, 39.21) * mm, v(33.07, 38.79) * mm, v(33.13, 32.81) * mm, v(33.13, 21.12) * mm]});
            skLineSegment(sketch, "E235", {"start": v(-33.98, 0.58) * mm, "end": v(-33.05, 4.42) * mm});
            skLineSegment(sketch, "E236", {"start": v(-33.05, 4.42) * mm, "end": v(-33.06, 21.9) * mm});
            skFitSpline(sketch, "E237", {"points": [v(33.99, 0.2) * mm, v(34.46, -1.7) * mm, v(34.9, -3.31) * mm, v(34.97, -3.39) * mm]});
            skFitSpline(sketch, "E238", {"points": [v(34.97, -3.39) * mm, v(35.25, -3.7) * mm, v(36.5, 0.56) * mm, v(37.04, 3.75) * mm]});
            skFitSpline(sketch, "E239", {"points": [v(37.04, 3.75) * mm, v(38.12, 10.1) * mm, v(38.05, 15.72) * mm, v(36.84, 19.08) * mm]});
            skFitSpline(sketch, "E240", {"points": [v(36.84, 19.08) * mm, v(36.33, 20.5) * mm, v(35.82, 21.33) * mm, v(34.78, 22.45) * mm]});
            skFitSpline(sketch, "E241", {"points": [v(34.78, 22.45) * mm, v(34.33, 22.92) * mm, v(33.96, 23.33) * mm, v(33.95, 23.36) * mm]});
            skFitSpline(sketch, "E242", {"points": [v(33.95, 23.36) * mm, v(33.94, 23.4) * mm, v(33.8, 28.18) * mm, v(33.63, 34) * mm]});
            skFitSpline(sketch, "E243", {"points": [v(33.63, 34) * mm, v(33.32, 45.32) * mm, v(33.3, 45.48) * mm, v(32.37, 47.6) * mm]});
            skFitSpline(sketch, "E244", {"points": [v(32.37, 47.6) * mm, v(31.62, 49.3) * mm, v(30.22, 51.2) * mm, v(28.51, 52.84) * mm]});
            skFitSpline(sketch, "E245", {"points": [v(28.51, 52.84) * mm, v(23.7, 57.46) * mm, v(16.34, 60.48) * mm, v(6.8, 61.77) * mm]});
            skFitSpline(sketch, "E246", {"points": [v(6.8, 61.77) * mm, v(3.62, 62.2) * mm, v(-3.69, 62.2) * mm, v(-6.87, 61.77) * mm]});
            skFitSpline(sketch, "E247", {"points": [v(-6.87, 61.77) * mm, v(-12.8, 60.97) * mm, v(-17.13, 59.74) * mm, v(-21.61, 57.57) * mm]});
            skFitSpline(sketch, "E248", {"points": [v(-21.61, 57.57) * mm, v(-24.73, 56.07) * mm, v(-26.62, 54.75) * mm, v(-28.87, 52.5) * mm]});
            skFitSpline(sketch, "E249", {"points": [v(-28.87, 52.5) * mm, v(-31.07, 50.29) * mm, v(-32.05, 48.78) * mm, v(-32.87, 46.34) * mm]});
            skLineSegment(sketch, "E250", {"start": v(33.13, 21.12) * mm, "end": v(33.13, 3.66) * mm});
            skLineSegment(sketch, "E251", {"start": v(33.13, 3.66) * mm, "end": v(33.99, 0.2) * mm});
            skFitSpline(sketch, "E252", {"points": [v(-33.64, 34.76) * mm, v(-33.77, 29.25) * mm, v(-33.92, 24.42) * mm, v(-33.97, 24.02) * mm]});
            skFitSpline(sketch, "E253", {"points": [v(-33.97, 24.02) * mm, v(-34.04, 23.44) * mm, v(-34.23, 23.1) * mm, v(-34.98, 22.3) * mm]});
            skFitSpline(sketch, "E254", {"points": [v(-34.98, 22.3) * mm, v(-35.97, 21.22) * mm, v(-36.87, 19.52) * mm, v(-37.27, 17.93) * mm]});
            skFitSpline(sketch, "E255", {"points": [v(-37.27, 17.93) * mm, v(-38.22, 14.24) * mm, v(-37.98, 7.48) * mm, v(-36.68, 1.58) * mm]});
            skFitSpline(sketch, "E256", {"points": [v(-36.68, 1.58) * mm, v(-36.16, -0.79) * mm, v(-35.22, -3.6) * mm, v(-35.03, -3.38) * mm]});
            skFitSpline(sketch, "E257", {"points": [v(-35.03, -3.38) * mm, v(-34.96, -3.31) * mm, v(-34.49, -1.53) * mm, v(-33.98, 0.58) * mm]});
            skLineSegment(sketch, "E258", {"start": v(-32.87, 46.34) * mm, "end": v(-33.4, 44.78) * mm});
            skLineSegment(sketch, "E259", {"start": v(-33.4, 44.78) * mm, "end": v(-33.64, 34.76) * mm});
            skFitSpline(sketch, "E260", {"points": [v(3.9, 14.83) * mm, v(5.8, 15.1) * mm, v(7.4, 15.38) * mm, v(7.45, 15.43) * mm]});
            skFitSpline(sketch, "E261", {"points": [v(7.45, 15.43) * mm, v(7.58, 15.56) * mm, v(10.12, 39.05) * mm, v(10.02, 39.2) * mm]});
            skFitSpline(sketch, "E262", {"points": [v(10.02, 39.2) * mm, v(9.98, 39.27) * mm, v(5.46, 39.33) * mm, v(-0.03, 39.33) * mm]});
            skFitSpline(sketch, "E263", {"points": [v(-0.03, 39.33) * mm, v(-5.52, 39.33) * mm, v(-10.05, 39.27) * mm, v(-10.09, 39.2) * mm]});
            skFitSpline(sketch, "E264", {"points": [v(-10.09, 39.2) * mm, v(-10.13, 39.14) * mm, v(-9.59, 33.76) * mm, v(-8.88, 27.26) * mm]});
            skFitSpline(sketch, "E265", {"points": [v(-8.88, 27.26) * mm, v(-7.94, 18.52) * mm, v(-7.55, 15.42) * mm, v(-7.38, 15.37) * mm]});
            skFitSpline(sketch, "E266", {"points": [v(-7.38, 15.37) * mm, v(-6.97, 15.23) * mm, v(-0.95, 14.37) * mm, v(-0.26, 14.35) * mm]});
            skFitSpline(sketch, "E267", {"points": [v(-0.26, 14.35) * mm, v(0.12, 14.34) * mm, v(1.99, 14.56) * mm, v(3.9, 14.83) * mm]});
            skFitSpline(sketch, "E268", {"points": [v(-12.46, -64.75) * mm, v(-15.7, -64.35) * mm, v(-17.1, -63.62) * mm, v(-19.12, -61.2) * mm]});
            skFitSpline(sketch, "E269", {"points": [v(-19.12, -61.2) * mm, v(-19.67, -60.54) * mm, v(-22.96, -55.52) * mm, v(-26.43, -50.05) * mm]});
            skFitSpline(sketch, "E270", {"points": [v(-32.89, -38.5) * mm, v(-32.96, -37.63) * mm, v(-33.29, -33.2) * mm, v(-33.61, -28.67) * mm]});
            skFitSpline(sketch, "E271", {"points": [v(-33.61, -28.67) * mm, v(-33.94, -24.13) * mm, v(-34.32, -19.52) * mm, v(-34.46, -18.42) * mm]});
            skFitSpline(sketch, "E272", {"points": [v(-34.46, -18.42) * mm, v(-34.77, -15.94) * mm, v(-35.46, -12.9) * mm, v(-36.33, -10.17) * mm]});
            skFitSpline(sketch, "E273", {"points": [v(-36.33, -10.17) * mm, v(-36.82, -8.61) * mm, v(-36.97, -7.9) * mm, v(-36.91, -7.38) * mm]});
            skFitSpline(sketch, "E274", {"points": [v(-36.91, -7.38) * mm, v(-36.84, -6.79) * mm, v(-36.94, -6.43) * mm, v(-37.5, -5.3) * mm]});
            skFitSpline(sketch, "E275", {"points": [v(-37.5, -5.3) * mm, v(-38.8, -2.67) * mm, v(-39.8, 1.26) * mm, v(-40.45, 6.17) * mm]});
            skFitSpline(sketch, "E276", {"points": [v(-40.45, 6.17) * mm, v(-40.83, 9.1) * mm, v(-40.95, 13.42) * mm, v(-40.71, 15.43) * mm]});
            skFitSpline(sketch, "E277", {"points": [v(-40.71, 15.43) * mm, v(-40.29, 18.93) * mm, v(-39.14, 22.04) * mm, v(-37.63, 23.8) * mm]});
            skFitSpline(sketch, "E278", {"points": [v(-37.63, 23.8) * mm, v(-37.02, 24.5) * mm, v(-36.86, 24.82) * mm, v(-36.86, 25.3) * mm]});
            skFitSpline(sketch, "E279", {"points": [v(-36.86, 25.3) * mm, v(-36.86, 28.51) * mm, v(-36.32, 44.63) * mm, v(-36.2, 45.36) * mm]});
            skFitSpline(sketch, "E280", {"points": [v(-36.2, 45.36) * mm, v(-34.67, 53.89) * mm, v(-25.47, 60.99) * mm, v(-12.2, 63.9) * mm]});
            skFitSpline(sketch, "E281", {"points": [v(-12.2, 63.9) * mm, v(-7.35, 64.95) * mm, v(-0.22, 65.29) * mm, v(6.14, 64.75) * mm]});
            skFitSpline(sketch, "E282", {"points": [v(6.14, 64.75) * mm, v(16.13, 63.9) * mm, v(25.09, 60.3) * mm, v(30.69, 54.84) * mm]});
            skFitSpline(sketch, "E283", {"points": [v(30.69, 54.84) * mm, v(33.54, 52.07) * mm, v(35.27, 49.15) * mm, v(36.04, 45.82) * mm]});
            skFitSpline(sketch, "E284", {"points": [v(36.04, 45.82) * mm, v(36.23, 45) * mm, v(36.36, 42.4) * mm, v(36.54, 35.57) * mm]});
            skFitSpline(sketch, "E285", {"points": [v(36.54, 35.57) * mm, v(36.68, 30.53) * mm, v(36.8, 26.03) * mm, v(36.8, 25.55) * mm]});
            skFitSpline(sketch, "E286", {"points": [v(36.8, 25.55) * mm, v(36.8, 24.78) * mm, v(36.87, 24.6) * mm, v(37.54, 23.83) * mm]});
            skFitSpline(sketch, "E287", {"points": [v(37.54, 23.83) * mm, v(39.56, 21.45) * mm, v(40.56, 18.17) * mm, v(40.74, 13.33) * mm]});
            skFitSpline(sketch, "E288", {"points": [v(40.74, 13.33) * mm, v(40.97, 6.87) * mm, v(39.37, -1.9) * mm, v(37.27, -5.66) * mm]});
            skFitSpline(sketch, "E289", {"points": [v(37.27, -5.66) * mm, v(36.83, -6.44) * mm, v(36.77, -6.68) * mm, v(36.86, -7.38) * mm]});
            skFitSpline(sketch, "E290", {"points": [v(36.86, -7.38) * mm, v(36.93, -8) * mm, v(36.86, -8.48) * mm, v(36.55, -9.36) * mm]});
            skFitSpline(sketch, "E291", {"points": [v(36.55, -9.36) * mm, v(36, -10.93) * mm, v(35.2, -13.82) * mm, v(34.9, -15.33) * mm]});
            skFitSpline(sketch, "E292", {"points": [v(34.9, -15.33) * mm, v(34.42, -17.68) * mm, v(34.14, -20.59) * mm, v(33.47, -29.92) * mm]});
            skFitSpline(sketch, "E293", {"points": [v(33.47, -29.92) * mm, v(33.1, -35.05) * mm, v(32.76, -39.46) * mm, v(32.72, -39.73) * mm]});
            skFitSpline(sketch, "E294", {"points": [v(32.72, -39.73) * mm, v(32.64, -40.14) * mm, v(24.8, -52.7) * mm, v(20.85, -58.71) * mm]});
            skFitSpline(sketch, "E295", {"points": [v(20.85, -58.71) * mm, v(19.41, -60.9) * mm, v(17.69, -62.9) * mm, v(16.72, -63.5) * mm]});
            skFitSpline(sketch, "E296", {"points": [v(16.72, -63.5) * mm, v(15.75, -64.1) * mm, v(14.27, -64.5) * mm, v(12.22, -64.75) * mm]});
            skFitSpline(sketch, "E297", {"points": [v(12.22, -64.75) * mm, v(9.6, -65.06) * mm, v(-9.86, -65.06) * mm, v(-12.46, -64.75) * mm]});
            skLineSegment(sketch, "E298", {"start": v(-26.43, -50.05) * mm, "end": v(-32.75, -40.1) * mm});
            skLineSegment(sketch, "E299", {"start": v(-32.75, -40.1) * mm, "end": v(-32.89, -38.5) * mm});
            skFitSpline(sketch, "E300", {"points": [v(11.55, -62.1) * mm, v(14.27, -61.65) * mm, v(14.9, -61.42) * mm, v(15.92, -60.45) * mm]});
            skFitSpline(sketch, "E301", {"points": [v(15.92, -60.45) * mm, v(16.41, -59.98) * mm, v(17.08, -59.25) * mm, v(17.39, -58.82) * mm]});
            skFitSpline(sketch, "E302", {"points": [v(17.39, -58.82) * mm, v(18.71, -57.02) * mm, v(29.97, -39.08) * mm, v(29.97, -38.76) * mm]});
            skFitSpline(sketch, "E303", {"points": [v(29.97, -38.76) * mm, v(29.98, -38.57) * mm, v(30.26, -34.64) * mm, v(30.6, -30.03) * mm]});
            skFitSpline(sketch, "E304", {"points": [v(30.6, -30.03) * mm, v(30.94, -25.41) * mm, v(31.17, -21.6) * mm, v(31.11, -21.57) * mm]});
            skFitSpline(sketch, "E305", {"points": [v(31.11, -21.57) * mm, v(31.05, -21.53) * mm, v(30.73, -21.97) * mm, v(30.4, -22.54) * mm]});
            skFitSpline(sketch, "E306", {"points": [v(30.4, -22.54) * mm, v(30.06, -23.12) * mm, v(28.88, -24.86) * mm, v(27.77, -26.42) * mm]});
            skFitSpline(sketch, "E307", {"points": [v(27.77, -26.42) * mm, v(24.1, -31.55) * mm, v(22.7, -34.17) * mm, v(20.78, -39.56) * mm]});
            skFitSpline(sketch, "E308", {"points": [v(20.63, -48.42) * mm, v(19.82, -50.49) * mm, v(18.06, -53.98) * mm, v(17.32, -55.02) * mm]});
            skFitSpline(sketch, "E309", {"points": [v(17.32, -55.02) * mm, v(16.42, -56.26) * mm, v(15.75, -56.59) * mm, v(14.13, -56.56) * mm]});
            skFitSpline(sketch, "E310", {"points": [v(14.13, -56.56) * mm, v(13.24, -56.54) * mm, v(12.44, -56.4) * mm, v(11.3, -56.02) * mm]});
            skFitSpline(sketch, "E311", {"points": [v(11.3, -56.02) * mm, v(10.43, -55.74) * mm, v(9.67, -55.56) * mm, v(9.62, -55.63) * mm]});
            skFitSpline(sketch, "E312", {"points": [v(9.62, -55.63) * mm, v(9.56, -55.7) * mm, v(9.34, -56.27) * mm, v(9.13, -56.91) * mm]});
            skFitSpline(sketch, "E313", {"points": [v(9.13, -56.91) * mm, v(8.6, -58.58) * mm, v(8.38, -58.94) * mm, v(7.78, -59.15) * mm]});
            skFitSpline(sketch, "E314", {"points": [v(7.78, -59.15) * mm, v(6.93, -59.44) * mm, v(-7.21, -59.4) * mm, v(-7.94, -59.1) * mm]});
            skFitSpline(sketch, "E315", {"points": [v(-7.94, -59.1) * mm, v(-8.51, -58.86) * mm, v(-8.87, -58.17) * mm, v(-9.35, -56.38) * mm]});
            skFitSpline(sketch, "E316", {"points": [v(-9.35, -56.38) * mm, v(-9.46, -56) * mm, v(-9.6, -55.64) * mm, v(-9.68, -55.6) * mm]});
            skFitSpline(sketch, "E317", {"points": [v(-9.68, -55.6) * mm, v(-9.76, -55.54) * mm, v(-10.37, -55.69) * mm, v(-11.04, -55.92) * mm]});
            skFitSpline(sketch, "E318", {"points": [v(-11.04, -55.92) * mm, v(-13.9, -56.89) * mm, v(-15.69, -56.83) * mm, v(-16.78, -55.74) * mm]});
            skFitSpline(sketch, "E319", {"points": [v(-16.78, -55.74) * mm, v(-17.53, -55) * mm, v(-18.52, -53.26) * mm, v(-19.7, -50.66) * mm]});
            skFitSpline(sketch, "E320", {"points": [v(-19.7, -50.66) * mm, v(-21.33, -47.1) * mm, v(-21.27, -47.45) * mm, v(-20.69, -44.21) * mm]});
            skLineSegment(sketch, "E321", {"start": v(20.78, -39.56) * mm, "end": v(20.11, -41.41) * mm});
            skLineSegment(sketch, "E322", {"start": v(20.11, -41.41) * mm, "end": v(20.63, -44.26) * mm});
            skLineSegment(sketch, "E323", {"start": v(20.63, -44.26) * mm, "end": v(21.15, -47.1) * mm});
            skLineSegment(sketch, "E324", {"start": v(21.15, -47.1) * mm, "end": v(20.63, -48.42) * mm});
            skFitSpline(sketch, "E325", {"points": [v(-20.7, -39.92) * mm, v(-22.25, -35.47) * mm, v(-24.27, -31.35) * mm, v(-26.03, -29.08) * mm]});
            skFitSpline(sketch, "E326", {"points": [v(-26.03, -29.08) * mm, v(-26.63, -28.3) * mm, v(-29.71, -23.73) * mm, v(-30.98, -21.73) * mm]});
            skFitSpline(sketch, "E327", {"points": [v(-30.98, -21.73) * mm, v(-31.15, -21.46) * mm, v(-31.18, -21.51) * mm, v(-31.19, -22.13) * mm]});
            skFitSpline(sketch, "E328", {"points": [v(-31.19, -22.13) * mm, v(-31.2, -23.48) * mm, v(-30.03, -38.91) * mm, v(-29.88, -39.25) * mm]});
            skFitSpline(sketch, "E329", {"points": [v(-29.88, -39.25) * mm, v(-29.61, -39.87) * mm, v(-18.02, -58.04) * mm, v(-17.3, -58.98) * mm]});
            skFitSpline(sketch, "E330", {"points": [v(-17.3, -58.98) * mm, v(-16.14, -60.47) * mm, v(-15.17, -61.28) * mm, v(-14.17, -61.57) * mm]});
            skFitSpline(sketch, "E331", {"points": [v(-14.17, -61.57) * mm, v(-11.43, -62.34) * mm, v(-9.17, -62.47) * mm, v(0.88, -62.42) * mm]});
            skFitSpline(sketch, "E332", {"points": [v(0.88, -62.42) * mm, v(8.33, -62.39) * mm, v(10.17, -62.33) * mm, v(11.55, -62.1) * mm]});
            skLineSegment(sketch, "E333", {"start": v(-20.69, -44.21) * mm, "end": v(-20.18, -41.42) * mm});
            skLineSegment(sketch, "E334", {"start": v(-20.18, -41.42) * mm, "end": v(-20.7, -39.92) * mm});
            skFitSpline(sketch, "E335", {"points": [v(6.29, -56.26) * mm, v(6.4, -56.13) * mm, v(6.53, -55.76) * mm, v(6.58, -55.43) * mm]});
            skFitSpline(sketch, "E336", {"points": [v(-6.65, -55.43) * mm, v(-6.46, -56.55) * mm, v(-6.78, -56.5) * mm, v(-0.03, -56.5) * mm]});
            skFitSpline(sketch, "E337", {"points": [v(-0.03, -56.5) * mm, v(5.04, -56.5) * mm, v(6.13, -56.46) * mm, v(6.29, -56.26) * mm]});
            skLineSegment(sketch, "E338", {"start": v(6.58, -55.43) * mm, "end": v(6.68, -54.83) * mm});
            skLineSegment(sketch, "E339", {"start": v(6.68, -54.83) * mm, "end": v(-0.03, -54.83) * mm});
            skLineSegment(sketch, "E340", {"start": v(-0.03, -54.83) * mm, "end": v(-6.74, -54.83) * mm});
            skLineSegment(sketch, "E341", {"start": v(-6.74, -54.83) * mm, "end": v(-6.65, -55.43) * mm});
            skFitSpline(sketch, "E342", {"points": [v(-12.33, -53.33) * mm, v(-11.48, -53.06) * mm, v(-10.67, -52.76) * mm, v(-10.54, -52.68) * mm]});
            skFitSpline(sketch, "E343", {"points": [v(-10.54, -52.68) * mm, v(-10.34, -52.55) * mm, v(-10.38, -52.23) * mm, v(-10.83, -50.64) * mm]});
            skFitSpline(sketch, "E344", {"points": [v(-10.83, -50.64) * mm, v(-11.12, -49.6) * mm, v(-11.4, -48.54) * mm, v(-11.46, -48.29) * mm]});
            skFitSpline(sketch, "E345", {"points": [v(-11.46, -48.29) * mm, v(-11.52, -48.04) * mm, v(-11.66, -47.83) * mm, v(-11.76, -47.83) * mm]});
            skFitSpline(sketch, "E346", {"points": [v(-11.76, -47.83) * mm, v(-11.87, -47.83) * mm, v(-12.4, -48.28) * mm, v(-12.94, -48.83) * mm]});
            skFitSpline(sketch, "E347", {"points": [v(-12.94, -48.83) * mm, v(-13.79, -49.7) * mm, v(-13.99, -49.83) * mm, v(-14.54, -49.83) * mm]});
            skFitSpline(sketch, "E348", {"points": [v(-14.54, -49.83) * mm, v(-15.27, -49.83) * mm, v(-15.66, -49.45) * mm, v(-16.55, -47.88) * mm]});
            skFitSpline(sketch, "E349", {"points": [v(-16.55, -47.88) * mm, v(-17.66, -45.91) * mm, v(-17.89, -45.6) * mm, v(-18.05, -45.85) * mm]});
            skFitSpline(sketch, "E350", {"points": [v(-18.05, -45.85) * mm, v(-18.36, -46.34) * mm, v(-18.16, -47.16) * mm, v(-17.23, -49.26) * mm]});
            skFitSpline(sketch, "E351", {"points": [v(-17.23, -49.26) * mm, v(-16.22, -51.52) * mm, v(-15.35, -53.15) * mm, v(-14.92, -53.58) * mm]});
            skFitSpline(sketch, "E352", {"points": [v(-14.92, -53.58) * mm, v(-14.56, -53.94) * mm, v(-14.06, -53.9) * mm, v(-12.33, -53.33) * mm]});
            skFitSpline(sketch, "E353", {"points": [v(14.87, -53.57) * mm, v(15.27, -53.17) * mm, v(16.23, -51.37) * mm, v(17.23, -49.15) * mm]});
            skFitSpline(sketch, "E354", {"points": [v(17.23, -49.15) * mm, v(17.93, -47.6) * mm, v(18.14, -46.95) * mm, v(18.1, -46.46) * mm]});
            skFitSpline(sketch, "E355", {"points": [v(18.1, -46.46) * mm, v(18.07, -46.11) * mm, v(17.97, -45.82) * mm, v(17.88, -45.81) * mm]});
            skFitSpline(sketch, "E356", {"points": [v(17.88, -45.81) * mm, v(17.8, -45.8) * mm, v(17.28, -46.54) * mm, v(16.74, -47.44) * mm]});
            skFitSpline(sketch, "E357", {"points": [v(16.74, -47.44) * mm, v(15.5, -49.56) * mm, v(15.23, -49.83) * mm, v(14.47, -49.83) * mm]});
            skFitSpline(sketch, "E358", {"points": [v(14.47, -49.83) * mm, v(13.96, -49.83) * mm, v(13.73, -49.69) * mm, v(12.88, -48.83) * mm]});
            skFitSpline(sketch, "E359", {"points": [v(12.88, -48.83) * mm, v(12.34, -48.28) * mm, v(11.81, -47.83) * mm, v(11.71, -47.83) * mm]});
            skFitSpline(sketch, "E360", {"points": [v(11.71, -47.83) * mm, v(11.57, -47.83) * mm, v(10.3, -52.06) * mm, v(10.3, -52.53) * mm]});
            skFitSpline(sketch, "E361", {"points": [v(10.3, -52.53) * mm, v(10.3, -52.76) * mm, v(13.46, -53.8) * mm, v(14.25, -53.82) * mm]});
            skFitSpline(sketch, "E362", {"points": [v(14.25, -53.82) * mm, v(14.45, -53.83) * mm, v(14.73, -53.71) * mm, v(14.87, -53.57) * mm]});
            skFitSpline(sketch, "E363", {"points": [v(7.63, -51.37) * mm, v(8.61, -47.83) * mm, v(8.93, -46.57) * mm, v(8.86, -46.46) * mm]});
            skFitSpline(sketch, "E364", {"points": [v(8.86, -46.46) * mm, v(8.77, -46.31) * mm, v(-8.76, -46.28) * mm, v(-8.9, -46.43) * mm]});
            skFitSpline(sketch, "E365", {"points": [v(-8.9, -46.43) * mm, v(-9, -46.51) * mm, v(-8.44, -48.78) * mm, v(-7.79, -51.04) * mm]});
            skFitSpline(sketch, "E366", {"points": [v(-13.5, -45.38) * mm, v(-13.15, -45.04) * mm, v(-12.87, -44.66) * mm, v(-12.87, -44.53) * mm]});
            skFitSpline(sketch, "E367", {"points": [v(-12.87, -44.53) * mm, v(-12.87, -44.17) * mm, v(-13.8, -42.52) * mm, v(-14.58, -41.48) * mm]});
            skFitSpline(sketch, "E368", {"points": [v(-14.58, -41.48) * mm, v(-15.6, -40.14) * mm, v(-18.33, -37.24) * mm, v(-18.46, -37.37) * mm]});
            skFitSpline(sketch, "E369", {"points": [v(-18.46, -37.37) * mm, v(-18.7, -37.62) * mm, v(-17.28, -41.03) * mm, v(-16, -43.25) * mm]});
            skFitSpline(sketch, "E370", {"points": [v(-16, -43.25) * mm, v(-14.57, -45.71) * mm, v(-14.38, -46) * mm, v(-14.23, -46) * mm]});
            skFitSpline(sketch, "E371", {"points": [v(-14.23, -46) * mm, v(-14.17, -46) * mm, v(-13.85, -45.72) * mm, v(-13.5, -45.38) * mm]});
            skLineSegment(sketch, "E372", {"start": v(-7.79, -51.04) * mm, "end": v(-7.5, -52) * mm});
            skLineSegment(sketch, "E373", {"start": v(-7.5, -52) * mm, "end": v(-0.03, -52) * mm});
            skLineSegment(sketch, "E374", {"start": v(-0.03, -52) * mm, "end": v(7.45, -52) * mm});
            skLineSegment(sketch, "E375", {"start": v(7.45, -52) * mm, "end": v(7.63, -51.37) * mm});
            skFitSpline(sketch, "E376", {"points": [v(15.26, -44.4) * mm, v(15.75, -43.58) * mm, v(16.4, -42.46) * mm, v(16.71, -41.91) * mm]});
            skFitSpline(sketch, "E377", {"points": [v(16.71, -41.91) * mm, v(17.36, -40.77) * mm, v(18.7, -37.17) * mm, v(18.47, -37.17) * mm]});
            skFitSpline(sketch, "E378", {"points": [v(18.47, -37.17) * mm, v(18.16, -37.17) * mm, v(14.56, -41.31) * mm, v(13.78, -42.58) * mm]});
            skFitSpline(sketch, "E379", {"points": [v(13.78, -42.58) * mm, v(12.64, -44.42) * mm, v(12.62, -44.55) * mm, v(13.4, -45.35) * mm]});
            skFitSpline(sketch, "E380", {"points": [v(13.4, -45.35) * mm, v(13.75, -45.7) * mm, v(14.12, -45.98) * mm, v(14.21, -45.95) * mm]});
            skFitSpline(sketch, "E381", {"points": [v(14.21, -45.95) * mm, v(14.3, -45.91) * mm, v(14.78, -45.22) * mm, v(15.26, -44.4) * mm]});
            skFitSpline(sketch, "E382", {"points": [v(10.45, -42.71) * mm, v(11.54, -40.47) * mm, v(12.62, -39.14) * mm, v(17.65, -33.82) * mm]});
            skFitSpline(sketch, "E383", {"points": [v(17.65, -33.82) * mm, v(21.65, -29.6) * mm, v(22.64, -28.48) * mm, v(24.37, -26.27) * mm]});
            skFitSpline(sketch, "E384", {"points": [v(24.37, -26.27) * mm, v(26.83, -23.11) * mm, v(27.19, -21.93) * mm, v(27.56, -15.93) * mm]});
            skFitSpline(sketch, "E385", {"points": [v(27.56, -15.93) * mm, v(27.7, -13.63) * mm, v(27.86, -11.32) * mm, v(27.9, -10.8) * mm]});
            skFitSpline(sketch, "E386", {"points": [v(27.9, -10.8) * mm, v(27.96, -10.26) * mm, v(27.94, -9.83) * mm, v(27.86, -9.84) * mm]});
            skFitSpline(sketch, "E387", {"points": [v(27.86, -9.84) * mm, v(27.78, -9.84) * mm, v(27.38, -10.18) * mm, v(26.97, -10.6) * mm]});
            skFitSpline(sketch, "E388", {"points": [v(26.97, -10.6) * mm, v(25.42, -12.16) * mm, v(22.77, -13.62) * mm, v(20.07, -14.4) * mm]});
            skFitSpline(sketch, "E389", {"points": [v(20.07, -14.4) * mm, v(17.94, -15.02) * mm, v(10.96, -16.36) * mm, v(10.46, -16.25) * mm]});
            skFitSpline(sketch, "E390", {"points": [v(10.46, -16.25) * mm, v(9.76, -16.1) * mm, v(8.16, -14.26) * mm, v(7.45, -12.79) * mm]});
            skFitSpline(sketch, "E391", {"points": [v(7.45, -12.79) * mm, v(7, -11.88) * mm, v(7.05, -11.9) * mm, v(4.93, -12.29) * mm]});
            skFitSpline(sketch, "E392", {"points": [v(4.93, -12.29) * mm, v(2.77, -12.68) * mm, v(-2.83, -12.68) * mm, v(-5, -12.29) * mm]});
            skFitSpline(sketch, "E393", {"points": [v(-5, -12.29) * mm, v(-5.84, -12.13) * mm, v(-6.66, -12) * mm, v(-6.82, -12) * mm]});
            skFitSpline(sketch, "E394", {"points": [v(-6.82, -12) * mm, v(-7.01, -12) * mm, v(-7.3, -12.37) * mm, v(-7.66, -13.04) * mm]});
            skFitSpline(sketch, "E395", {"points": [v(-7.66, -13.04) * mm, v(-8.35, -14.37) * mm, v(-9.89, -16.1) * mm, v(-10.5, -16.24) * mm]});
            skFitSpline(sketch, "E396", {"points": [v(-10.5, -16.24) * mm, v(-11.03, -16.36) * mm, v(-17.94, -15.04) * mm, v(-20.13, -14.4) * mm]});
            skFitSpline(sketch, "E397", {"points": [v(-20.13, -14.4) * mm, v(-22.9, -13.6) * mm, v(-25.2, -12.33) * mm, v(-26.98, -10.62) * mm]});
            skFitSpline(sketch, "E398", {"points": [v(-28.03, -10.11) * mm, v(-28.03, -10.39) * mm, v(-27.96, -11.2) * mm, v(-27.87, -11.93) * mm]});
            skFitSpline(sketch, "E399", {"points": [v(-27.87, -11.93) * mm, v(-27.78, -12.66) * mm, v(-27.63, -14.75) * mm, v(-27.54, -16.6) * mm]});
            skFitSpline(sketch, "E400", {"points": [v(-27.54, -16.6) * mm, v(-27.28, -21.75) * mm, v(-26.92, -22.83) * mm, v(-24.27, -26.57) * mm]});
            skFitSpline(sketch, "E401", {"points": [v(-24.27, -26.57) * mm, v(-22.9, -28.49) * mm, v(-21.81, -29.72) * mm, v(-18.06, -33.57) * mm]});
            skFitSpline(sketch, "E402", {"points": [v(-18.06, -33.57) * mm, v(-13.3, -38.44) * mm, v(-11.87, -40.16) * mm, v(-10.77, -42.25) * mm]});
            skLineSegment(sketch, "E403", {"start": v(-26.98, -10.62) * mm, "end": v(-28.03, -9.61) * mm});
            skLineSegment(sketch, "E404", {"start": v(-28.03, -9.61) * mm, "end": v(-28.03, -10.11) * mm});
            skFitSpline(sketch, "E405", {"points": [v(-30.69, -12.22) * mm, v(-30.93, -10.16) * mm, v(-30.91, -8.74) * mm, v(-30.62, -6.57) * mm]});
            skFitSpline(sketch, "E406", {"points": [v(-30.62, -6.57) * mm, v(-30.3, -4.22) * mm, v(-29.84, -1.96) * mm, v(-29.1, 0.8) * mm]});
            skLineSegment(sketch, "E407", {"start": v(-10.77, -42.25) * mm, "end": v(-10.12, -43.5) * mm});
            skLineSegment(sketch, "E408", {"start": v(-10.12, -43.5) * mm, "end": v(-0.02, -43.5) * mm});
            skLineSegment(sketch, "E409", {"start": v(-0.02, -43.5) * mm, "end": v(10.07, -43.5) * mm});
            skLineSegment(sketch, "E410", {"start": v(10.07, -43.5) * mm, "end": v(10.45, -42.71) * mm});
            skFitSpline(sketch, "E411", {"points": [v(-28.58, 10.96) * mm, v(-28.67, 19.21) * mm, v(-28.76, 20.63) * mm, v(-29.54, 25) * mm]});
            skFitSpline(sketch, "E412", {"points": [v(-29.54, 25) * mm, v(-29.73, 26.05) * mm, v(-29.95, 26.99) * mm, v(-30.04, 27.07) * mm]});
            skFitSpline(sketch, "E413", {"points": [v(-30.04, 27.07) * mm, v(-30.14, 27.17) * mm, v(-30.2, 22.84) * mm, v(-30.2, 15.36) * mm]});
            skLineSegment(sketch, "E414", {"start": v(-29.1, 0.8) * mm, "end": v(-28.5, 3.01) * mm});
            skLineSegment(sketch, "E415", {"start": v(-28.5, 3.01) * mm, "end": v(-28.58, 10.96) * mm});
            skFitSpline(sketch, "E416", {"points": [v(-31.78, -2.83) * mm, v(-32.65, -6.31) * mm, v(-33.36, -9.35) * mm, v(-33.36, -9.58) * mm]});
            skFitSpline(sketch, "E417", {"points": [v(-33.36, -9.58) * mm, v(-33.36, -9.93) * mm, v(-32.03, -13.12) * mm, v(-30.93, -15.4) * mm]});
            skLineSegment(sketch, "E418", {"start": v(-30.2, 15.36) * mm, "end": v(-30.2, 3.5) * mm});
            skLineSegment(sketch, "E419", {"start": v(-30.2, 3.5) * mm, "end": v(-31.78, -2.83) * mm});
            skFitSpline(sketch, "E420", {"points": [v(-30.56, -14.9) * mm, v(-30.53, -14.27) * mm, v(-30.59, -13.06) * mm, v(-30.69, -12.22) * mm]});
            skLineSegment(sketch, "E421", {"start": v(-30.93, -15.4) * mm, "end": v(-30.61, -16.05) * mm});
            skLineSegment(sketch, "E422", {"start": v(-30.61, -16.05) * mm, "end": v(-30.56, -14.9) * mm});
            skFitSpline(sketch, "E423", {"points": [v(31.05, -15.04) * mm, v(32.34, -12.27) * mm, v(33.3, -9.94) * mm, v(33.3, -9.57) * mm]});
            skFitSpline(sketch, "E424", {"points": [v(33.3, -9.57) * mm, v(33.3, -9.35) * mm, v(32.59, -6.31) * mm, v(31.72, -2.83) * mm]});
            skFitSpline(sketch, "E425", {"points": [v(30.13, 15.36) * mm, v(30.13, 23.29) * mm, v(30.08, 27.18) * mm, v(29.97, 27.06) * mm]});
            skFitSpline(sketch, "E426", {"points": [v(29.97, 27.06) * mm, v(29.77, 26.87) * mm, v(29.1, 22.85) * mm, v(28.77, 20) * mm]});
            skFitSpline(sketch, "E427", {"points": [v(28.77, 20) * mm, v(28.62, 18.68) * mm, v(28.55, 15.63) * mm, v(28.55, 10.25) * mm]});
            skLineSegment(sketch, "E428", {"start": v(31.72, -2.83) * mm, "end": v(30.13, 3.5) * mm});
            skLineSegment(sketch, "E429", {"start": v(30.13, 3.5) * mm, "end": v(30.13, 15.36) * mm});
            skFitSpline(sketch, "E430", {"points": [v(29.25, -0.17) * mm, v(30.65, -5.32) * mm, v(30.94, -8.3) * mm, v(30.56, -13.8) * mm]});
            skFitSpline(sketch, "E431", {"points": [v(30.56, -13.8) * mm, v(30.48, -15) * mm, v(30.46, -16) * mm, v(30.51, -16) * mm]});
            skFitSpline(sketch, "E432", {"points": [v(30.51, -16) * mm, v(30.56, -16) * mm, v(30.8, -15.57) * mm, v(31.05, -15.04) * mm]});
            skLineSegment(sketch, "E433", {"start": v(28.55, 10.25) * mm, "end": v(28.55, 2.42) * mm});
            skLineSegment(sketch, "E434", {"start": v(28.55, 2.42) * mm, "end": v(29.25, -0.17) * mm});
            skFitSpline(sketch, "E435", {"points": [v(-10.64, -12.53) * mm, v(-9.8, -11.4) * mm, v(-9.65, -10.93) * mm, v(-10, -10.62) * mm]});
            skFitSpline(sketch, "E436", {"points": [v(-10, -10.62) * mm, v(-10.5, -10.18) * mm, v(-17.2, -6.64) * mm, v(-21.28, -4.66) * mm]});
            skFitSpline(sketch, "E437", {"points": [v(-21.28, -4.66) * mm, v(-25.81, -2.46) * mm, v(-26.33, -2.24) * mm, v(-26.5, -2.4) * mm]});
            skFitSpline(sketch, "E438", {"points": [v(-26.5, -2.4) * mm, v(-26.69, -2.6) * mm, v(-26.62, -5.86) * mm, v(-26.4, -6.6) * mm]});
            skFitSpline(sketch, "E439", {"points": [v(-26.4, -6.6) * mm, v(-25.86, -8.42) * mm, v(-23.3, -10.39) * mm, v(-20.03, -11.49) * mm]});
            skFitSpline(sketch, "E440", {"points": [v(-20.03, -11.49) * mm, v(-18.97, -11.84) * mm, v(-12.3, -13.29) * mm, v(-11.59, -13.32) * mm]});
            skFitSpline(sketch, "E441", {"points": [v(-11.59, -13.32) * mm, v(-11.34, -13.33) * mm, v(-11.04, -13.08) * mm, v(-10.64, -12.53) * mm]});
            skFitSpline(sketch, "E442", {"points": [v(15.28, -12.58) * mm, v(20.25, -11.57) * mm, v(21.8, -11) * mm, v(24.06, -9.4) * mm]});
            skFitSpline(sketch, "E443", {"points": [v(24.06, -9.4) * mm, v(26.02, -8.02) * mm, v(26.52, -7) * mm, v(26.54, -4.39) * mm]});
            skFitSpline(sketch, "E444", {"points": [v(26.54, -4.39) * mm, v(26.54, -3.37) * mm, v(26.5, -2.48) * mm, v(26.43, -2.4) * mm]});
            skFitSpline(sketch, "E445", {"points": [v(26.43, -2.4) * mm, v(26.26, -2.24) * mm, v(25.78, -2.45) * mm, v(21.38, -4.58) * mm]});
            skFitSpline(sketch, "E446", {"points": [v(21.38, -4.58) * mm, v(17.2, -6.6) * mm, v(10.39, -10.21) * mm, v(9.93, -10.65) * mm]});
            skFitSpline(sketch, "E447", {"points": [v(9.93, -10.65) * mm, v(9.65, -10.91) * mm, v(9.65, -10.96) * mm, v(9.98, -11.57) * mm]});
            skFitSpline(sketch, "E448", {"points": [v(9.98, -11.57) * mm, v(10.45, -12.44) * mm, v(11.17, -13.33) * mm, v(11.4, -13.33) * mm]});
            skFitSpline(sketch, "E449", {"points": [v(11.4, -13.33) * mm, v(11.51, -13.33) * mm, v(13.26, -13) * mm, v(15.28, -12.58) * mm]});
            skFitSpline(sketch, "E450", {"points": [v(5.13, -9.34) * mm, v(6.8, -9) * mm, v(7.09, -8.87) * mm, v(11.63, -6.42) * mm]});
            skFitSpline(sketch, "E451", {"points": [v(11.63, -6.42) * mm, v(16.82, -3.64) * mm, v(19.72, -2.17) * mm, v(23.52, -0.4) * mm]});
            skFitSpline(sketch, "E452", {"points": [v(25.86, 1.4) * mm, v(25.62, 2.54) * mm, v(25.68, 17.8) * mm, v(25.94, 20.08) * mm]});
            skFitSpline(sketch, "E453", {"points": [v(25.94, 20.08) * mm, v(26.53, 25.46) * mm, v(27.74, 31.45) * mm, v(29.27, 36.52) * mm]});
            skFitSpline(sketch, "E454", {"points": [v(29.27, 36.52) * mm, v(29.54, 37.4) * mm, v(29.7, 38.2) * mm, v(29.65, 38.3) * mm]});
            skFitSpline(sketch, "E455", {"points": [v(29.65, 38.3) * mm, v(29.48, 38.57) * mm, v(22.92, 41.75) * mm, v(21, 42.5) * mm]});
            skFitSpline(sketch, "E456", {"points": [v(21, 42.5) * mm, v(19.01, 43.27) * mm, v(15.97, 44.1) * mm, v(14.6, 44.27) * mm]});
            skFitSpline(sketch, "E457", {"points": [v(14.6, 44.27) * mm, v(14.06, 44.33) * mm, v(13.63, 44.35) * mm, v(13.63, 44.31) * mm]});
            skFitSpline(sketch, "E458", {"points": [v(13.63, 44.31) * mm, v(13.63, 44.28) * mm, v(12.89, 37.36) * mm, v(11.98, 28.95) * mm]});
            skFitSpline(sketch, "E459", {"points": [v(11.98, 28.95) * mm, v(10.76, 17.69) * mm, v(10.26, 13.54) * mm, v(10.07, 13.25) * mm]});
            skFitSpline(sketch, "E460", {"points": [v(10.07, 13.25) * mm, v(9.71, 12.7) * mm, v(9.3, 12.6) * mm, v(4.34, 11.9) * mm]});
            skLineSegment(sketch, "E461", {"start": v(23.52, -0.4) * mm, "end": v(26, 0.74) * mm});
            skLineSegment(sketch, "E462", {"start": v(26, 0.74) * mm, "end": v(25.86, 1.4) * mm});
            skFitSpline(sketch, "E463", {"points": [v(-4.33, 11.9) * mm, v(-9.4, 12.63) * mm, v(-9.79, 12.72) * mm, v(-10.12, 13.23) * mm]});
            skFitSpline(sketch, "E464", {"points": [v(-10.12, 13.23) * mm, v(-10.3, 13.52) * mm, v(-10.82, 17.7) * mm, v(-12.04, 28.94) * mm]});
            skFitSpline(sketch, "E465", {"points": [v(-12.04, 28.94) * mm, v(-12.95, 37.36) * mm, v(-13.7, 44.28) * mm, v(-13.7, 44.31) * mm]});
            skFitSpline(sketch, "E466", {"points": [v(-13.7, 44.31) * mm, v(-13.7, 44.35) * mm, v(-14.13, 44.33) * mm, v(-14.66, 44.27) * mm]});
            skFitSpline(sketch, "E467", {"points": [v(-14.66, 44.27) * mm, v(-15.98, 44.11) * mm, v(-19, 43.3) * mm, v(-20.88, 42.58) * mm]});
            skFitSpline(sketch, "E468", {"points": [v(-20.88, 42.58) * mm, v(-22.63, 41.9) * mm, v(-29.12, 38.79) * mm, v(-29.54, 38.4) * mm]});
            skFitSpline(sketch, "E469", {"points": [v(-29.54, 38.4) * mm, v(-29.78, 38.19) * mm, v(-29.74, 37.94) * mm, v(-29.07, 35.62) * mm]});
            skFitSpline(sketch, "E470", {"points": [v(-29.07, 35.62) * mm, v(-27.69, 30.82) * mm, v(-26.68, 25.85) * mm, v(-26.08, 20.82) * mm]});
            skFitSpline(sketch, "E471", {"points": [v(-26.08, 20.82) * mm, v(-25.84, 18.85) * mm, v(-25.79, 16.94) * mm, v(-25.78, 10.25) * mm]});
            skFitSpline(sketch, "E472", {"points": [v(-25.78, 10.25) * mm, v(-25.78, 5.76) * mm, v(-25.84, 1.78) * mm, v(-25.92, 1.4) * mm]});
            skLineSegment(sketch, "E473", {"start": v(4.34, 11.9) * mm, "end": v(-0.04, 11.27) * mm});
            skLineSegment(sketch, "E474", {"start": v(-0.04, 11.27) * mm, "end": v(-4.33, 11.9) * mm});
            skFitSpline(sketch, "E475", {"points": [v(-23.59, -0.4) * mm, v(-20.06, -2.04) * mm, v(-15.22, -4.5) * mm, v(-10.8, -6.89) * mm]});
            skFitSpline(sketch, "E476", {"points": [v(-10.8, -6.89) * mm, v(-6.78, -9.08) * mm, v(-6.2, -9.29) * mm, v(-3.2, -9.66) * mm]});
            skFitSpline(sketch, "E477", {"points": [v(-3.2, -9.66) * mm, v(-1.17, -9.91) * mm, v(3.12, -9.74) * mm, v(5.13, -9.34) * mm]});
            skLineSegment(sketch, "E478", {"start": v(-25.92, 1.4) * mm, "end": v(-26.06, 0.74) * mm});
            skLineSegment(sketch, "E479", {"start": v(-26.06, 0.74) * mm, "end": v(-23.59, -0.4) * mm});
            skFitSpline(sketch, "E480", {"points": [v(-33.03, 21.5) * mm, v(-33.03, 38.3) * mm, v(-33.02, 39.1) * mm, v(-32.72, 39.58) * mm]});
            skFitSpline(sketch, "E481", {"points": [v(-32.72, 39.58) * mm, v(-32.38, 40.15) * mm, v(-30.19, 41.4) * mm, v(-26.11, 43.34) * mm]});
            skFitSpline(sketch, "E482", {"points": [v(-26.11, 43.34) * mm, v(-22.85, 44.9) * mm, v(-20.41, 45.84) * mm, v(-17.95, 46.46) * mm]});
            skFitSpline(sketch, "E483", {"points": [v(-17.95, 46.46) * mm, v(-14.52, 47.34) * mm, v(-12.41, 47.54) * mm, v(-11.74, 47.07) * mm]});
            skFitSpline(sketch, "E484", {"points": [v(-11.74, 47.07) * mm, v(-11.17, 46.67) * mm, v(-11.07, 46.37) * mm, v(-10.86, 44.4) * mm]});
            skFitSpline(sketch, "E485", {"points": [v(-10.86, 44.4) * mm, v(-10.75, 43.4) * mm, v(-10.57, 42.49) * mm, v(-10.46, 42.37) * mm]});
            skFitSpline(sketch, "E486", {"points": [v(-10.46, 42.37) * mm, v(-10.18, 42.07) * mm, v(10.18, 42.07) * mm, v(10.43, 42.37) * mm]});
            skFitSpline(sketch, "E487", {"points": [v(10.43, 42.37) * mm, v(10.52, 42.49) * mm, v(10.69, 43.4) * mm, v(10.8, 44.4) * mm]});
            skFitSpline(sketch, "E488", {"points": [v(10.8, 44.4) * mm, v(11, 46.36) * mm, v(11.1, 46.67) * mm, v(11.67, 47.07) * mm]});
            skFitSpline(sketch, "E489", {"points": [v(11.67, 47.07) * mm, v(12.88, 47.92) * mm, v(19.1, 46.5) * mm, v(24.12, 44.25) * mm]});
            skFitSpline(sketch, "E490", {"points": [v(24.12, 44.25) * mm, v(28.76, 42.17) * mm, v(32.35, 40.2) * mm, v(32.7, 39.53) * mm]});
            skFitSpline(sketch, "E491", {"points": [v(32.7, 39.53) * mm, v(32.92, 39.14) * mm, v(32.95, 36.65) * mm, v(32.96, 21.45) * mm]});
            skLineSegment(sketch, "E492", {"start": v(-33.96, 0.12) * mm, "end": v(-33.02, 3.92) * mm});
            skLineSegment(sketch, "E493", {"start": v(-33.02, 3.92) * mm, "end": v(-33.03, 21.5) * mm});
            skFitSpline(sketch, "E494", {"points": [v(33.9, 0.07) * mm, v(34.5, -2.27) * mm, v(34.91, -3.66) * mm, v(35.03, -3.62) * mm]});
            skFitSpline(sketch, "E495", {"points": [v(35.03, -3.62) * mm, v(35.33, -3.52) * mm, v(36.41, -0.08) * mm, v(36.87, 2.25) * mm]});
            skFitSpline(sketch, "E496", {"points": [v(36.87, 2.25) * mm, v(37.5, 5.48) * mm, v(37.8, 7.94) * mm, v(37.9, 11) * mm]});
            skFitSpline(sketch, "E497", {"points": [v(37.9, 11) * mm, v(38.1, 16.42) * mm, v(37.21, 19.98) * mm, v(35.07, 22.3) * mm]});
            skFitSpline(sketch, "E498", {"points": [v(35.07, 22.3) * mm, v(34.56, 22.86) * mm, v(34.1, 23.49) * mm, v(34.06, 23.7) * mm]});
            skFitSpline(sketch, "E499", {"points": [v(34.06, 23.7) * mm, v(34.02, 23.9) * mm, v(33.86, 28.7) * mm, v(33.72, 34.35) * mm]});
            skFitSpline(sketch, "E500", {"points": [v(33.72, 34.35) * mm, v(33.43, 45.76) * mm, v(33.43, 45.74) * mm, v(32.2, 48.22) * mm]});
            skFitSpline(sketch, "E501", {"points": [v(32.2, 48.22) * mm, v(31.3, 49.99) * mm, v(30.35, 51.24) * mm, v(28.61, 52.92) * mm]});
            skFitSpline(sketch, "E502", {"points": [v(28.61, 52.92) * mm, v(23.76, 57.6) * mm, v(16.3, 60.65) * mm, v(6.53, 61.94) * mm]});
            skFitSpline(sketch, "E503", {"points": [v(6.53, 61.94) * mm, v(3.54, 62.33) * mm, v(-3.6, 62.33) * mm, v(-6.6, 61.94) * mm]});
            skFitSpline(sketch, "E504", {"points": [v(-6.6, 61.94) * mm, v(-19.52, 60.23) * mm, v(-28.72, 55.26) * mm, v(-32.36, 48.02) * mm]});
            skFitSpline(sketch, "E505", {"points": [v(-32.36, 48.02) * mm, v(-33.46, 45.83) * mm, v(-33.49, 45.52) * mm, v(-33.77, 34.46) * mm]});
            skFitSpline(sketch, "E506", {"points": [v(-33.77, 34.46) * mm, v(-33.91, 28.93) * mm, v(-34.06, 24.16) * mm, v(-34.1, 23.85) * mm]});
            skFitSpline(sketch, "E507", {"points": [v(-34.1, 23.85) * mm, v(-34.16, 23.46) * mm, v(-34.46, 23) * mm, v(-35.12, 22.31) * mm]});
            skFitSpline(sketch, "E508", {"points": [v(-35.12, 22.31) * mm, v(-37.24, 20.09) * mm, v(-38.17, 16.44) * mm, v(-37.98, 11.08) * mm]});
            skFitSpline(sketch, "E509", {"points": [v(-37.98, 11.08) * mm, v(-37.83, 6.93) * mm, v(-37.15, 2.44) * mm, v(-36.19, -0.83) * mm]});
            skFitSpline(sketch, "E510", {"points": [v(-36.19, -0.83) * mm, v(-35.63, -2.71) * mm, v(-35.25, -3.67) * mm, v(-35.05, -3.67) * mm]});
            skFitSpline(sketch, "E511", {"points": [v(-35.05, -3.67) * mm, v(-34.97, -3.67) * mm, v(-34.48, -1.96) * mm, v(-33.96, 0.12) * mm]});
            skLineSegment(sketch, "E512", {"start": v(32.96, 21.45) * mm, "end": v(32.97, 3.83) * mm});
            skLineSegment(sketch, "E513", {"start": v(32.97, 3.83) * mm, "end": v(33.9, 0.07) * mm});
            skFitSpline(sketch, "E514", {"points": [v(3.8, 14.69) * mm, v(5.77, 14.97) * mm, v(7.45, 15.27) * mm, v(7.53, 15.34) * mm]});
            skFitSpline(sketch, "E515", {"points": [v(7.53, 15.34) * mm, v(7.7, 15.5) * mm, v(10.28, 39.03) * mm, v(10.14, 39.2) * mm]});
            skFitSpline(sketch, "E516", {"points": [v(10.14, 39.2) * mm, v(10.08, 39.27) * mm, v(5.48, 39.33) * mm, v(-0.08, 39.33) * mm]});
            skFitSpline(sketch, "E517", {"points": [v(-10.2, 38.79) * mm, v(-10.2, 37.84) * mm, v(-7.73, 15.48) * mm, v(-7.62, 15.36) * mm]});
            skFitSpline(sketch, "E518", {"points": [v(-7.62, 15.36) * mm, v(-7.5, 15.24) * mm, v(-1.12, 14.22) * mm, v(-0.28, 14.18) * mm]});
            skFitSpline(sketch, "E519", {"points": [v(-0.28, 14.18) * mm, v(0, 14.17) * mm, v(1.83, 14.4) * mm, v(3.8, 14.69) * mm]});
            skLineSegment(sketch, "E520", {"start": v(-0.08, 39.33) * mm, "end": v(-10.2, 39.33) * mm});
            skLineSegment(sketch, "E521", {"start": v(-10.2, 39.33) * mm, "end": v(-10.2, 38.79) * mm});
            skFitSpline(sketch, "E522", {"points": [v(-12.28, -64.73) * mm, v(-15.57, -64.28) * mm, v(-17.04, -63.56) * mm, v(-18.76, -61.54) * mm]});
            skFitSpline(sketch, "E523", {"points": [v(-18.76, -61.54) * mm, v(-19.85, -60.26) * mm, v(-20.27, -59.63) * mm, v(-26.92, -49.14) * mm]});
            skFitSpline(sketch, "E524", {"points": [v(-33.36, -30.9) * mm, v(-33.73, -25.87) * mm, v(-34.1, -20.89) * mm, v(-34.2, -19.83) * mm]});
            skFitSpline(sketch, "E525", {"points": [v(-34.2, -19.83) * mm, v(-34.47, -17.07) * mm, v(-35.23, -13.45) * mm, v(-36.12, -10.67) * mm]});
            skFitSpline(sketch, "E526", {"points": [v(-36.12, -10.67) * mm, v(-36.77, -8.68) * mm, v(-36.88, -8.12) * mm, v(-36.8, -7.46) * mm]});
            skFitSpline(sketch, "E527", {"points": [v(-36.8, -7.46) * mm, v(-36.72, -6.76) * mm, v(-36.79, -6.52) * mm, v(-37.29, -5.6) * mm]});
            skFitSpline(sketch, "E528", {"points": [v(-37.29, -5.6) * mm, v(-37.97, -4.37) * mm, v(-39.03, -1.2) * mm, v(-39.5, 1) * mm]});
            skFitSpline(sketch, "E529", {"points": [v(-39.5, 1) * mm, v(-40.46, 5.44) * mm, v(-40.96, 11) * mm, v(-40.7, 14.39) * mm]});
            skFitSpline(sketch, "E530", {"points": [v(-40.7, 14.39) * mm, v(-40.4, 18.39) * mm, v(-39.44, 21.3) * mm, v(-37.7, 23.58) * mm]});
            skLineSegment(sketch, "E531", {"start": v(-26.92, -49.14) * mm, "end": v(-32.7, -40.04) * mm});
            skLineSegment(sketch, "E532", {"start": v(-32.7, -40.04) * mm, "end": v(-33.36, -30.9) * mm});
            skFitSpline(sketch, "E533", {"points": [v(-36.58, 34.08) * mm, v(-36.34, 44.29) * mm, v(-36.2, 45.78) * mm, v(-35.36, 47.97) * mm]});
            skFitSpline(sketch, "E534", {"points": [v(-35.36, 47.97) * mm, v(-32.33, 55.83) * mm, v(-23.15, 61.8) * mm, v(-10.45, 64.15) * mm]});
            skFitSpline(sketch, "E535", {"points": [v(-10.45, 64.15) * mm, v(-3.95, 65.36) * mm, v(4.86, 65.26) * mm, v(11.59, 63.9) * mm]});
            skFitSpline(sketch, "E536", {"points": [v(11.59, 63.9) * mm, v(24.26, 61.34) * mm, v(33.32, 54.9) * mm, v(35.73, 46.71) * mm]});
            skFitSpline(sketch, "E537", {"points": [v(35.73, 46.71) * mm, v(36.23, 45.02) * mm, v(36.23, 45.02) * mm, v(36.53, 33) * mm]});
            skLineSegment(sketch, "E538", {"start": v(-37.7, 23.58) * mm, "end": v(-36.8, 24.75) * mm});
            skLineSegment(sketch, "E539", {"start": v(-36.8, 24.75) * mm, "end": v(-36.58, 34.08) * mm});
            skFitSpline(sketch, "E540", {"points": [v(37.6, 23.6) * mm, v(39.84, 20.67) * mm, v(40.69, 17.5) * mm, v(40.68, 12.17) * mm]});
            skFitSpline(sketch, "E541", {"points": [v(40.68, 12.17) * mm, v(40.67, 5.76) * mm, v(39.14, -2.1) * mm, v(37.23, -5.6) * mm]});
            skFitSpline(sketch, "E542", {"points": [v(37.23, -5.6) * mm, v(36.75, -6.46) * mm, v(36.69, -6.72) * mm, v(36.76, -7.45) * mm]});
            skFitSpline(sketch, "E543", {"points": [v(36.76, -7.45) * mm, v(36.82, -8.13) * mm, v(36.71, -8.67) * mm, v(36.24, -10.1) * mm]});
            skFitSpline(sketch, "E544", {"points": [v(36.24, -10.1) * mm, v(35.12, -13.49) * mm, v(34.47, -16.59) * mm, v(34.14, -20.08) * mm]});
            skFitSpline(sketch, "E545", {"points": [v(34.14, -20.08) * mm, v(34.04, -21.1) * mm, v(33.66, -26) * mm, v(33.3, -30.97) * mm]});
            skLineSegment(sketch, "E546", {"start": v(36.53, 33) * mm, "end": v(36.75, 24.75) * mm});
            skLineSegment(sketch, "E547", {"start": v(36.75, 24.75) * mm, "end": v(37.6, 23.6) * mm});
            skFitSpline(sketch, "E548", {"points": [v(26.38, -49.9) * mm, v(22.94, -55.33) * mm, v(19.64, -60.37) * mm, v(19.06, -61.1) * mm]});
            skFitSpline(sketch, "E549", {"points": [v(19.06, -61.1) * mm, v(17.12, -63.52) * mm, v(15.68, -64.27) * mm, v(12.02, -64.75) * mm]});
            skFitSpline(sketch, "E550", {"points": [v(12.02, -64.75) * mm, v(9.4, -65.09) * mm, v(-9.74, -65.08) * mm, v(-12.28, -64.73) * mm]});
            skLineSegment(sketch, "E551", {"start": v(33.3, -30.97) * mm, "end": v(32.64, -40.03) * mm});
            skLineSegment(sketch, "E552", {"start": v(32.64, -40.03) * mm, "end": v(26.38, -49.9) * mm});
            skFitSpline(sketch, "E553", {"points": [v(12.13, -62.1) * mm, v(14.92, -61.55) * mm, v(15.55, -61.2) * mm, v(17.03, -59.36) * mm]});
            skFitSpline(sketch, "E554", {"points": [v(17.03, -59.36) * mm, v(18.33, -57.74) * mm, v(29.84, -39.53) * mm, v(30, -38.83) * mm]});
            skFitSpline(sketch, "E555", {"points": [v(30, -38.83) * mm, v(30.11, -38.35) * mm, v(31.3, -22.39) * mm, v(31.3, -21.45) * mm]});
            skFitSpline(sketch, "E556", {"points": [v(31.3, -21.45) * mm, v(31.3, -20.98) * mm, v(31.04, -21.25) * mm, v(30.4, -22.4) * mm]});
            skFitSpline(sketch, "E557", {"points": [v(30.4, -22.4) * mm, v(30.08, -22.97) * mm, v(28.84, -24.81) * mm, v(27.64, -26.48) * mm]});
            skFitSpline(sketch, "E558", {"points": [v(27.64, -26.48) * mm, v(25.35, -29.7) * mm, v(24.2, -31.5) * mm, v(23.26, -33.42) * mm]});
            skFitSpline(sketch, "E559", {"points": [v(23.26, -33.42) * mm, v(22.48, -35) * mm, v(20.92, -38.8) * mm, v(20.45, -40.29) * mm]});
            skFitSpline(sketch, "E560", {"points": [v(20.52, -44.04) * mm, v(20.77, -45.44) * mm, v(20.97, -46.79) * mm, v(20.97, -47.04) * mm]});
            skFitSpline(sketch, "E561", {"points": [v(20.97, -47.04) * mm, v(20.96, -47.67) * mm, v(18.94, -52.2) * mm, v(17.88, -53.97) * mm]});
            skFitSpline(sketch, "E562", {"points": [v(17.88, -53.97) * mm, v(17.4, -54.76) * mm, v(16.74, -55.63) * mm, v(16.4, -55.9) * mm]});
            skFitSpline(sketch, "E563", {"points": [v(16.4, -55.9) * mm, v(15.84, -56.36) * mm, v(15.62, -56.42) * mm, v(14.5, -56.47) * mm]});
            skFitSpline(sketch, "E564", {"points": [v(14.5, -56.47) * mm, v(13.48, -56.5) * mm, v(12.93, -56.43) * mm, v(11.8, -56.08) * mm]});
            skFitSpline(sketch, "E565", {"points": [v(11.8, -56.08) * mm, v(9.32, -55.31) * mm, v(9.56, -55.24) * mm, v(9.04, -56.92) * mm]});
            skFitSpline(sketch, "E566", {"points": [v(9.04, -56.92) * mm, v(8.78, -57.77) * mm, v(8.43, -58.55) * mm, v(8.2, -58.77) * mm]});
            skLineSegment(sketch, "E567", {"start": v(20.45, -40.29) * mm, "end": v(20.07, -41.5) * mm});
            skLineSegment(sketch, "E568", {"start": v(20.07, -41.5) * mm, "end": v(20.52, -44.04) * mm});
            skFitSpline(sketch, "E569", {"points": [v(-8.26, -58.79) * mm, v(-8.47, -58.58) * mm, v(-8.84, -57.75) * mm, v(-9.09, -56.95) * mm]});
            skFitSpline(sketch, "E570", {"points": [v(-9.09, -56.95) * mm, v(-9.39, -56) * mm, v(-9.63, -55.5) * mm, v(-9.78, -55.5) * mm]});
            skFitSpline(sketch, "E571", {"points": [v(-9.78, -55.5) * mm, v(-9.92, -55.5) * mm, v(-10.6, -55.7) * mm, v(-11.32, -55.93) * mm]});
            skFitSpline(sketch, "E572", {"points": [v(-11.32, -55.93) * mm, v(-12.1, -56.2) * mm, v(-13.16, -56.4) * mm, v(-13.96, -56.45) * mm]});
            skFitSpline(sketch, "E573", {"points": [v(-13.96, -56.45) * mm, v(-16.13, -56.6) * mm, v(-16.83, -56.07) * mm, v(-18.44, -53.08) * mm]});
            skFitSpline(sketch, "E574", {"points": [v(-18.44, -53.08) * mm, v(-19.42, -51.28) * mm, v(-20.86, -47.97) * mm, v(-20.97, -47.29) * mm]});
            skFitSpline(sketch, "E575", {"points": [v(-20.97, -47.29) * mm, v(-21.02, -46.99) * mm, v(-20.87, -45.68) * mm, v(-20.63, -44.39) * mm]});
            skFitSpline(sketch, "E576", {"points": [v(-20.63, -44.39) * mm, v(-20.4, -43.1) * mm, v(-20.2, -41.81) * mm, v(-20.2, -41.54) * mm]});
            skFitSpline(sketch, "E577", {"points": [v(-20.2, -41.54) * mm, v(-20.2, -41.04) * mm, v(-20.97, -38.82) * mm, v(-22.1, -36.08) * mm]});
            skFitSpline(sketch, "E578", {"points": [v(-22.1, -36.08) * mm, v(-23.1, -33.67) * mm, v(-24.62, -30.86) * mm, v(-25.76, -29.32) * mm]});
            skFitSpline(sketch, "E579", {"points": [v(-25.76, -29.32) * mm, v(-26.95, -27.71) * mm, v(-30.46, -22.5) * mm, v(-30.91, -21.67) * mm]});
            skFitSpline(sketch, "E580", {"points": [v(-30.91, -21.67) * mm, v(-31.07, -21.37) * mm, v(-31.25, -21.16) * mm, v(-31.3, -21.21) * mm]});
            skFitSpline(sketch, "E581", {"points": [v(-31.3, -21.21) * mm, v(-31.41, -21.32) * mm, v(-30.25, -37.83) * mm, v(-30.06, -38.75) * mm]});
            skFitSpline(sketch, "E582", {"points": [v(-30.06, -38.75) * mm, v(-29.92, -39.43) * mm, v(-19.22, -56.51) * mm, v(-17.4, -58.95) * mm]});
            skFitSpline(sketch, "E583", {"points": [v(-17.4, -58.95) * mm, v(-15.77, -61.15) * mm, v(-15.01, -61.6) * mm, v(-12.12, -62.07) * mm]});
            skFitSpline(sketch, "E584", {"points": [v(-12.12, -62.07) * mm, v(-9.79, -62.46) * mm, v(-9.86, -62.45) * mm, v(0.72, -62.42) * mm]});
            skFitSpline(sketch, "E585", {"points": [v(0.72, -62.42) * mm, v(9.26, -62.38) * mm, v(10.92, -62.34) * mm, v(12.13, -62.1) * mm]});
            skLineSegment(sketch, "E586", {"start": v(8.2, -58.77) * mm, "end": v(7.82, -59.16) * mm});
            skLineSegment(sketch, "E587", {"start": v(7.82, -59.16) * mm, "end": v(-0.03, -59.16) * mm});
            skLineSegment(sketch, "E588", {"start": v(-0.03, -59.16) * mm, "end": v(-7.88, -59.16) * mm});
            skLineSegment(sketch, "E589", {"start": v(-7.88, -59.16) * mm, "end": v(-8.26, -58.79) * mm});
            skFitSpline(sketch, "E590", {"points": [v(6.44, -56.2) * mm, v(6.53, -56.05) * mm, v(6.65, -55.67) * mm, v(6.71, -55.37) * mm]});
            skFitSpline(sketch, "E591", {"points": [v(-6.8, -55.24) * mm, v(-6.74, -55.47) * mm, v(-6.62, -55.84) * mm, v(-6.54, -56.07) * mm]});
            skLineSegment(sketch, "E592", {"start": v(6.71, -55.37) * mm, "end": v(6.83, -54.83) * mm});
            skLineSegment(sketch, "E593", {"start": v(6.83, -54.83) * mm, "end": v(-0.04, -54.83) * mm});
            skLineSegment(sketch, "E594", {"start": v(-0.04, -54.83) * mm, "end": v(-6.9, -54.83) * mm});
            skLineSegment(sketch, "E595", {"start": v(-6.9, -54.83) * mm, "end": v(-6.8, -55.24) * mm});
            skFitSpline(sketch, "E596", {"points": [v(-0.04, -56.5) * mm, v(5.82, -56.5) * mm, v(6.3, -56.48) * mm, v(6.44, -56.2) * mm]});
            skLineSegment(sketch, "E597", {"start": v(-6.54, -56.07) * mm, "end": v(-6.37, -56.5) * mm});
            skLineSegment(sketch, "E598", {"start": v(-6.37, -56.5) * mm, "end": v(-0.04, -56.5) * mm});
            skFitSpline(sketch, "E599", {"points": [v(-11.7, -53.22) * mm, v(-10.78, -52.87) * mm, v(-10.44, -52.65) * mm, v(-10.4, -52.4) * mm]});
            skFitSpline(sketch, "E600", {"points": [v(-10.4, -52.4) * mm, v(-10.36, -52.1) * mm, v(-11.44, -47.87) * mm, v(-11.61, -47.7) * mm]});
            skFitSpline(sketch, "E601", {"points": [v(-11.61, -47.7) * mm, v(-11.66, -47.65) * mm, v(-12.22, -48.11) * mm, v(-12.86, -48.72) * mm]});
            skFitSpline(sketch, "E602", {"points": [v(-12.86, -48.72) * mm, v(-14.63, -50.4) * mm, v(-15.08, -50.27) * mm, v(-16.54, -47.75) * mm]});
            skFitSpline(sketch, "E603", {"points": [v(-16.54, -47.75) * mm, v(-17.86, -45.45) * mm, v(-17.87, -45.44) * mm, v(-18.07, -45.64) * mm]});
            skFitSpline(sketch, "E604", {"points": [v(-18.07, -45.64) * mm, v(-18.53, -46.1) * mm, v(-18.27, -47.23) * mm, v(-17.18, -49.58) * mm]});
            skFitSpline(sketch, "E605", {"points": [v(-17.18, -49.58) * mm, v(-16.59, -50.86) * mm, v(-15.82, -52.36) * mm, v(-15.47, -52.9) * mm]});
            skFitSpline(sketch, "E606", {"points": [v(-13.9, -53.79) * mm, v(-13.37, -53.74) * mm, v(-12.39, -53.49) * mm, v(-11.7, -53.22) * mm]});
            skLineSegment(sketch, "E607", {"start": v(-15.47, -52.9) * mm, "end": v(-14.84, -53.87) * mm});
            skLineSegment(sketch, "E608", {"start": v(-14.84, -53.87) * mm, "end": v(-13.9, -53.79) * mm});
            skFitSpline(sketch, "E609", {"points": [v(15.1, -53.41) * mm, v(15.56, -52.83) * mm, v(16.8, -50.4) * mm, v(17.62, -48.45) * mm]});
            skFitSpline(sketch, "E610", {"points": [v(17.62, -48.45) * mm, v(18.17, -47.15) * mm, v(18.29, -46.7) * mm, v(18.2, -46.24) * mm]});
            skFitSpline(sketch, "E611", {"points": [v(18.2, -46.24) * mm, v(18.14, -45.92) * mm, v(18.03, -45.62) * mm, v(17.96, -45.57) * mm]});
            skFitSpline(sketch, "E612", {"points": [v(17.96, -45.57) * mm, v(17.88, -45.53) * mm, v(17.28, -46.4) * mm, v(16.63, -47.5) * mm]});
            skFitSpline(sketch, "E613", {"points": [v(16.63, -47.5) * mm, v(14.95, -50.33) * mm, v(14.62, -50.44) * mm, v(12.8, -48.72) * mm]});
            skFitSpline(sketch, "E614", {"points": [v(12.8, -48.72) * mm, v(12.15, -48.11) * mm, v(11.59, -47.66) * mm, v(11.54, -47.7) * mm]});
            skFitSpline(sketch, "E615", {"points": [v(11.54, -47.7) * mm, v(11.42, -47.82) * mm, v(10.44, -51.44) * mm, v(10.34, -52.12) * mm]});
            skFitSpline(sketch, "E616", {"points": [v(10.34, -52.12) * mm, v(10.27, -52.62) * mm, v(10.31, -52.69) * mm, v(10.9, -52.94) * mm]});
            skFitSpline(sketch, "E617", {"points": [v(10.9, -52.94) * mm, v(12.1, -53.45) * mm, v(13.38, -53.8) * mm, v(14.08, -53.82) * mm]});
            skFitSpline(sketch, "E618", {"points": [v(14.08, -53.82) * mm, v(14.64, -53.83) * mm, v(14.84, -53.75) * mm, v(15.1, -53.41) * mm]});
            skFitSpline(sketch, "E619", {"points": [v(7.4, -52.04) * mm, v(7.5, -51.97) * mm, v(7.66, -51.61) * mm, v(7.76, -51.25) * mm]});
            skFitSpline(sketch, "E620", {"points": [v(7.76, -51.25) * mm, v(7.85, -50.88) * mm, v(8.17, -49.72) * mm, v(8.45, -48.66) * mm]});
            skFitSpline(sketch, "E621", {"points": [v(8.45, -48.66) * mm, v(8.73, -47.61) * mm, v(8.96, -46.65) * mm, v(8.97, -46.54) * mm]});
            skFitSpline(sketch, "E622", {"points": [v(8.97, -46.54) * mm, v(8.97, -46.38) * mm, v(7.06, -46.33) * mm, v(-0.03, -46.33) * mm]});
            skFitSpline(sketch, "E623", {"points": [v(-0.03, -46.33) * mm, v(-7.42, -46.33) * mm, v(-9.03, -46.37) * mm, v(-9.03, -46.55) * mm]});
            skFitSpline(sketch, "E624", {"points": [v(-9.03, -46.55) * mm, v(-9.03, -46.96) * mm, v(-7.67, -51.74) * mm, v(-7.5, -51.96) * mm]});
            skFitSpline(sketch, "E625", {"points": [v(-7.5, -51.96) * mm, v(-7.36, -52.12) * mm, v(-5.67, -52.16) * mm, v(-0.05, -52.16) * mm]});
            skFitSpline(sketch, "E626", {"points": [v(-0.05, -52.16) * mm, v(3.94, -52.16) * mm, v(7.3, -52.1) * mm, v(7.4, -52.04) * mm]});
            skFitSpline(sketch, "E627", {"points": [v(-13.2, -43.53) * mm, v(-13.52, -42.92) * mm, v(-14.2, -41.85) * mm, v(-14.73, -41.16) * mm]});
            skFitSpline(sketch, "E628", {"points": [v(-14.73, -41.16) * mm, v(-15.73, -39.85) * mm, v(-18.7, -36.8) * mm, v(-18.7, -37.1) * mm]});
            skFitSpline(sketch, "E629", {"points": [v(-18.7, -37.1) * mm, v(-18.7, -37.34) * mm, v(-17.6, -40.54) * mm, v(-17.36, -41.01) * mm]});
            skFitSpline(sketch, "E630", {"points": [v(-17.36, -41.01) * mm, v(-16.72, -42.25) * mm, v(-14.34, -46.16) * mm, v(-14.23, -46.16) * mm]});
            skFitSpline(sketch, "E631", {"points": [v(-14.23, -46.16) * mm, v(-14.16, -46.16) * mm, v(-13.77, -45.82) * mm, v(-13.36, -45.4) * mm]});
            skLineSegment(sketch, "E632", {"start": v(-13.36, -45.4) * mm, "end": v(-12.62, -44.65) * mm});
            skLineSegment(sketch, "E633", {"start": v(-12.62, -44.65) * mm, "end": v(-13.2, -43.53) * mm});
            skFitSpline(sketch, "E634", {"points": [v(15.9, -43.46) * mm, v(16.96, -41.64) * mm, v(17.61, -40.28) * mm, v(18.1, -38.9) * mm]});
            skFitSpline(sketch, "E635", {"points": [v(18.1, -38.9) * mm, v(18.48, -37.81) * mm, v(18.75, -36.9) * mm, v(18.71, -36.85) * mm]});
            skFitSpline(sketch, "E636", {"points": [v(18.71, -36.85) * mm, v(18.62, -36.76) * mm, v(15.81, -39.72) * mm, v(14.78, -41) * mm]});
            skFitSpline(sketch, "E637", {"points": [v(14.78, -41) * mm, v(14.05, -41.9) * mm, v(12.99, -43.65) * mm, v(12.71, -44.36) * mm]});
            skFitSpline(sketch, "E638", {"points": [v(12.71, -44.36) * mm, v(12.6, -44.68) * mm, v(13.9, -46.22) * mm, v(14.2, -46.11) * mm]});
            skFitSpline(sketch, "E639", {"points": [v(14.2, -46.11) * mm, v(14.3, -46.08) * mm, v(15.06, -44.89) * mm, v(15.9, -43.46) * mm]});
            skFitSpline(sketch, "E640", {"points": [v(10.06, -43.37) * mm, v(10.2, -43.21) * mm, v(10.7, -42.45) * mm, v(11.14, -41.68) * mm]});
            skFitSpline(sketch, "E641", {"points": [v(11.14, -41.68) * mm, v(12.3, -39.7) * mm, v(12.88, -39) * mm, v(16.41, -35.26) * mm]});
            skFitSpline(sketch, "E642", {"points": [v(16.41, -35.26) * mm, v(24.53, -26.68) * mm, v(26.3, -24.38) * mm, v(27.05, -21.42) * mm]});
            skFitSpline(sketch, "E643", {"points": [v(27.05, -21.42) * mm, v(27.35, -20.24) * mm, v(27.63, -17.43) * mm, v(27.64, -15.58) * mm]});
            skFitSpline(sketch, "E644", {"points": [v(27.64, -15.58) * mm, v(27.64, -14.85) * mm, v(27.74, -13.27) * mm, v(27.87, -12.08) * mm]});
            skFitSpline(sketch, "E645", {"points": [v(27.87, -12.08) * mm, v(28, -10.9) * mm, v(28.05, -9.86) * mm, v(27.98, -9.8) * mm]});
            skFitSpline(sketch, "E646", {"points": [v(27.98, -9.8) * mm, v(27.92, -9.72) * mm, v(27.46, -10.06) * mm, v(26.96, -10.54) * mm]});
            skFitSpline(sketch, "E647", {"points": [v(26.96, -10.54) * mm, v(25.12, -12.32) * mm, v(22.28, -13.8) * mm, v(19.22, -14.57) * mm]});
            skFitSpline(sketch, "E648", {"points": [v(19.22, -14.57) * mm, v(17.05, -15.11) * mm, v(11.45, -16.17) * mm, v(10.73, -16.17) * mm]});
            skFitSpline(sketch, "E649", {"points": [v(10.73, -16.17) * mm, v(10.24, -16.17) * mm, v(10.02, -16) * mm, v(9.16, -15.07) * mm]});
            skFitSpline(sketch, "E650", {"points": [v(9.16, -15.07) * mm, v(8.61, -14.47) * mm, v(7.9, -13.5) * mm, v(7.6, -12.9) * mm]});
            skFitSpline(sketch, "E651", {"points": [v(7.6, -12.9) * mm, v(7.08, -11.86) * mm, v(7.03, -11.82) * mm, v(6.55, -11.91) * mm]});
            skFitSpline(sketch, "E652", {"points": [v(6.55, -11.91) * mm, v(3.3, -12.57) * mm, v(-1.6, -12.7) * mm, v(-4.68, -12.23) * mm]});
            skFitSpline(sketch, "E653", {"points": [v(-4.68, -12.23) * mm, v(-7.03, -11.86) * mm, v(-7.04, -11.87) * mm, v(-7.26, -12.25) * mm]});
            skFitSpline(sketch, "E654", {"points": [v(-7.26, -12.25) * mm, v(-7.94, -13.46) * mm, v(-8.95, -14.86) * mm, v(-9.6, -15.48) * mm]});
            skFitSpline(sketch, "E655", {"points": [v(-11.33, -16.11) * mm, v(-12.96, -15.94) * mm, v(-19.02, -14.69) * mm, v(-20.53, -14.2) * mm]});
            skFitSpline(sketch, "E656", {"points": [v(-20.53, -14.2) * mm, v(-23.17, -13.37) * mm, v(-26.25, -11.56) * mm, v(-27.44, -10.15) * mm]});
            skFitSpline(sketch, "E657", {"points": [v(-27.44, -10.15) * mm, v(-28.05, -9.42) * mm, v(-28.2, -9.68) * mm, v(-28.02, -11.08) * mm]});
            skFitSpline(sketch, "E658", {"points": [v(-28.02, -11.08) * mm, v(-27.94, -11.72) * mm, v(-27.8, -13.79) * mm, v(-27.7, -15.67) * mm]});
            skFitSpline(sketch, "E659", {"points": [v(-27.7, -15.67) * mm, v(-27.41, -21.31) * mm, v(-26.98, -22.88) * mm, v(-24.85, -25.87) * mm]});
            skFitSpline(sketch, "E660", {"points": [v(-24.85, -25.87) * mm, v(-22.66, -28.97) * mm, v(-22.32, -29.35) * mm, v(-17.85, -33.93) * mm]});
            skFitSpline(sketch, "E661", {"points": [v(-17.85, -33.93) * mm, v(-13.26, -38.63) * mm, v(-12, -40.12) * mm, v(-10.94, -42.1) * mm]});
            skFitSpline(sketch, "E662", {"points": [v(-10.94, -42.1) * mm, v(-10.6, -42.73) * mm, v(-10.2, -43.34) * mm, v(-10.06, -43.46) * mm]});
            skFitSpline(sketch, "E663", {"points": [v(-10.06, -43.46) * mm, v(-9.86, -43.62) * mm, v(-7.6, -43.66) * mm, v(0, -43.66) * mm]});
            skFitSpline(sketch, "E664", {"points": [v(0, -43.66) * mm, v(9.12, -43.66) * mm, v(9.82, -43.64) * mm, v(10.06, -43.37) * mm]});
            skLineSegment(sketch, "E665", {"start": v(-9.6, -15.48) * mm, "end": v(-10.35, -16.22) * mm});
            skLineSegment(sketch, "E666", {"start": v(-10.35, -16.22) * mm, "end": v(-11.33, -16.11) * mm});
            skFitSpline(sketch, "E667", {"points": [v(-30.59, -12.33) * mm, v(-30.96, -8.55) * mm, v(-30.51, -4.67) * mm, v(-29.12, 0.4) * mm]});
            skFitSpline(sketch, "E668", {"points": [v(-28.53, 10.19) * mm, v(-28.53, 16) * mm, v(-28.6, 18.41) * mm, v(-28.8, 20.21) * mm]});
            skFitSpline(sketch, "E669", {"points": [v(-28.8, 20.21) * mm, v(-29.1, 23.1) * mm, v(-29.8, 27.24) * mm, v(-30.02, 27.63) * mm]});
            skFitSpline(sketch, "E670", {"points": [v(-30.02, 27.63) * mm, v(-30.13, 27.82) * mm, v(-30.19, 23.91) * mm, v(-30.2, 15.87) * mm]});
            skLineSegment(sketch, "E671", {"start": v(-29.12, 0.4) * mm, "end": v(-28.53, 2.53) * mm});
            skLineSegment(sketch, "E672", {"start": v(-28.53, 2.53) * mm, "end": v(-28.53, 10.19) * mm});
            skFitSpline(sketch, "E673", {"points": [v(-32.95, -11.12) * mm, v(-32.6, -11.93) * mm, v(-31.9, -13.45) * mm, v(-31.39, -14.5) * mm]});
            skLineSegment(sketch, "E674", {"start": v(-30.2, 15.87) * mm, "end": v(-30.2, 3.83) * mm});
            skLineSegment(sketch, "E675", {"start": v(-30.2, 3.83) * mm, "end": v(-31.88, -2.92) * mm});
            skLineSegment(sketch, "E676", {"start": v(-31.88, -2.92) * mm, "end": v(-33.57, -9.66) * mm});
            skLineSegment(sketch, "E677", {"start": v(-33.57, -9.66) * mm, "end": v(-32.95, -11.12) * mm});
            skFitSpline(sketch, "E678", {"points": [v(-30.4, -15.58) * mm, v(-30.37, -15.12) * mm, v(-30.46, -13.66) * mm, v(-30.59, -12.33) * mm]});
            skLineSegment(sketch, "E679", {"start": v(-31.39, -14.5) * mm, "end": v(-30.46, -16.42) * mm});
            skLineSegment(sketch, "E680", {"start": v(-30.46, -16.42) * mm, "end": v(-30.4, -15.58) * mm});
            skFitSpline(sketch, "E681", {"points": [v(30.12, 15.92) * mm, v(30.12, 22.53) * mm, v(30.06, 27.8) * mm, v(29.98, 27.66) * mm]});
            skFitSpline(sketch, "E682", {"points": [v(29.98, 27.66) * mm, v(29.9, 27.53) * mm, v(29.68, 26.51) * mm, v(29.48, 25.41) * mm]});
            skFitSpline(sketch, "E683", {"points": [v(29.48, 25.41) * mm, v(28.62, 20.63) * mm, v(28.6, 20.14) * mm, v(28.51, 11.27) * mm]});
            skLineSegment(sketch, "E684", {"start": v(32.14, -12.83) * mm, "end": v(33.5, -9.75) * mm});
            skLineSegment(sketch, "E685", {"start": v(33.5, -9.75) * mm, "end": v(31.82, -2.92) * mm});
            skLineSegment(sketch, "E686", {"start": v(31.82, -2.92) * mm, "end": v(30.12, 3.92) * mm});
            skLineSegment(sketch, "E687", {"start": v(30.12, 3.92) * mm, "end": v(30.12, 15.92) * mm});
            skFitSpline(sketch, "E688", {"points": [v(29.1, 0.2) * mm, v(30.57, -5.49) * mm, v(30.94, -8.67) * mm, v(30.55, -12.34) * mm]});
            skFitSpline(sketch, "E689", {"points": [v(30.55, -12.34) * mm, v(30.41, -13.64) * mm, v(30.3, -15.09) * mm, v(30.3, -15.55) * mm]});
            skFitSpline(sketch, "E690", {"points": [v(30.3, -15.55) * mm, v(30.3, -16.29) * mm, v(30.33, -16.37) * mm, v(30.53, -16.16) * mm]});
            skFitSpline(sketch, "E691", {"points": [v(30.53, -16.16) * mm, v(30.66, -16.03) * mm, v(31.38, -14.53) * mm, v(32.14, -12.83) * mm]});
            skLineSegment(sketch, "E692", {"start": v(28.51, 11.27) * mm, "end": v(28.44, 2.8) * mm});
            skLineSegment(sketch, "E693", {"start": v(28.44, 2.8) * mm, "end": v(29.1, 0.2) * mm});
            skFitSpline(sketch, "E694", {"points": [v(-10.73, -12.73) * mm, v(-10.04, -11.9) * mm, v(-9.63, -11.1) * mm, v(-9.74, -10.8) * mm]});
            skFitSpline(sketch, "E695", {"points": [v(-9.74, -10.8) * mm, v(-9.9, -10.38) * mm, v(-19.01, -5.56) * mm, v(-24.01, -3.25) * mm]});
            skFitSpline(sketch, "E696", {"points": [v(-24.01, -3.25) * mm, v(-25.9, -2.37) * mm, v(-26.44, -2.18) * mm, v(-26.55, -2.36) * mm]});
            skFitSpline(sketch, "E697", {"points": [v(-26.55, -2.36) * mm, v(-26.8, -2.75) * mm, v(-26.72, -5.7) * mm, v(-26.43, -6.68) * mm]});
            skFitSpline(sketch, "E698", {"points": [v(-26.43, -6.68) * mm, v(-25.9, -8.46) * mm, v(-23.23, -10.49) * mm, v(-19.99, -11.58) * mm]});
            skFitSpline(sketch, "E699", {"points": [v(-19.99, -11.58) * mm, v(-18.62, -12.04) * mm, v(-12.65, -13.3) * mm, v(-11.75, -13.32) * mm]});
            skFitSpline(sketch, "E700", {"points": [v(-11.75, -13.32) * mm, v(-11.34, -13.33) * mm, v(-11.11, -13.2) * mm, v(-10.73, -12.73) * mm]});
            skFitSpline(sketch, "E701", {"points": [v(15.3, -12.67) * mm, v(17.13, -12.3) * mm, v(19.21, -11.81) * mm, v(19.92, -11.58) * mm]});
            skFitSpline(sketch, "E702", {"points": [v(19.92, -11.58) * mm, v(23.22, -10.47) * mm, v(25.84, -8.48) * mm, v(26.37, -6.68) * mm]});
            skFitSpline(sketch, "E703", {"points": [v(26.37, -6.68) * mm, v(26.65, -5.71) * mm, v(26.73, -2.75) * mm, v(26.49, -2.36) * mm]});
            skFitSpline(sketch, "E704", {"points": [v(26.49, -2.36) * mm, v(26.38, -2.2) * mm, v(25.76, -2.42) * mm, v(23.78, -3.33) * mm]});
            skFitSpline(sketch, "E705", {"points": [v(23.78, -3.33) * mm, v(18.95, -5.57) * mm, v(9.84, -10.37) * mm, v(9.69, -10.76) * mm]});
            skFitSpline(sketch, "E706", {"points": [v(9.69, -10.76) * mm, v(9.47, -11.34) * mm, v(10.92, -13.33) * mm, v(11.56, -13.33) * mm]});
            skFitSpline(sketch, "E707", {"points": [v(11.56, -13.33) * mm, v(11.78, -13.33) * mm, v(13.47, -13.03) * mm, v(15.3, -12.67) * mm]});
            skFitSpline(sketch, "E708", {"points": [v(3.72, -9.66) * mm, v(6.25, -9.31) * mm, v(6.95, -9.04) * mm, v(10.89, -6.9) * mm]});
            skFitSpline(sketch, "E709", {"points": [v(10.89, -6.9) * mm, v(15.33, -4.49) * mm, v(20.18, -2.03) * mm, v(23.69, -0.41) * mm]});
            skFitSpline(sketch, "E710", {"points": [v(23.69, -0.41) * mm, v(26.1, 0.7) * mm, v(26.16, 0.74) * mm, v(26.03, 1.15) * mm]});
            skFitSpline(sketch, "E711", {"points": [v(26.03, 1.15) * mm, v(25.96, 1.39) * mm, v(25.88, 5.18) * mm, v(25.85, 9.58) * mm]});
            skFitSpline(sketch, "E712", {"points": [v(25.85, 9.58) * mm, v(25.78, 18.4) * mm, v(25.89, 20.2) * mm, v(26.8, 25.62) * mm]});
            skFitSpline(sketch, "E713", {"points": [v(26.8, 25.62) * mm, v(27.32, 28.7) * mm, v(28.5, 33.71) * mm, v(29.32, 36.39) * mm]});
            skFitSpline(sketch, "E714", {"points": [v(29.32, 36.39) * mm, v(29.6, 37.29) * mm, v(29.78, 38.14) * mm, v(29.73, 38.27) * mm]});
            skFitSpline(sketch, "E715", {"points": [v(29.73, 38.27) * mm, v(29.6, 38.59) * mm, v(22.75, 41.93) * mm, v(20.55, 42.75) * mm]});
            skFitSpline(sketch, "E716", {"points": [v(20.55, 42.75) * mm, v(18.83, 43.39) * mm, v(15.82, 44.2) * mm, v(14.43, 44.4) * mm]});
            skFitSpline(sketch, "E717", {"points": [v(14.43, 44.4) * mm, v(13.7, 44.5) * mm, v(13.64, 44.49) * mm, v(13.56, 44.13) * mm]});
            skFitSpline(sketch, "E718", {"points": [v(13.56, 44.13) * mm, v(13.51, 43.92) * mm, v(12.76, 37.03) * mm, v(11.88, 28.83) * mm]});
            skFitSpline(sketch, "E719", {"points": [v(11.88, 28.83) * mm, v(11, 20.63) * mm, v(10.22, 13.75) * mm, v(10.14, 13.55) * mm]});
            skFitSpline(sketch, "E720", {"points": [v(10.14, 13.55) * mm, v(10.05, 13.35) * mm, v(9.8, 13.07) * mm, v(9.6, 12.94) * mm]});
            skFitSpline(sketch, "E721", {"points": [v(9.6, 12.94) * mm, v(9.38, 12.8) * mm, v(7.19, 12.4) * mm, v(4.6, 12.02) * mm]});
            skFitSpline(sketch, "E722", {"points": [v(-4.66, 12.02) * mm, v(-7.25, 12.4) * mm, v(-9.45, 12.8) * mm, v(-9.66, 12.94) * mm]});
            skFitSpline(sketch, "E723", {"points": [v(-9.66, 12.94) * mm, v(-9.88, 13.07) * mm, v(-10.12, 13.35) * mm, v(-10.2, 13.55) * mm]});
            skFitSpline(sketch, "E724", {"points": [v(-10.2, 13.55) * mm, v(-10.28, 13.75) * mm, v(-11.07, 20.63) * mm, v(-11.94, 28.83) * mm]});
            skFitSpline(sketch, "E725", {"points": [v(-11.94, 28.83) * mm, v(-12.82, 37.03) * mm, v(-13.57, 43.92) * mm, v(-13.62, 44.13) * mm]});
            skFitSpline(sketch, "E726", {"points": [v(-13.62, 44.13) * mm, v(-13.7, 44.49) * mm, v(-13.77, 44.5) * mm, v(-14.5, 44.4) * mm]});
            skFitSpline(sketch, "E727", {"points": [v(-14.5, 44.4) * mm, v(-15.84, 44.21) * mm, v(-18.9, 43.38) * mm, v(-20.7, 42.71) * mm]});
            skFitSpline(sketch, "E728", {"points": [v(-20.7, 42.71) * mm, v(-21.65, 42.37) * mm, v(-24.08, 41.26) * mm, v(-26.1, 40.25) * mm]});
            skFitSpline(sketch, "E729", {"points": [v(-26.1, 40.25) * mm, v(-29.47, 38.57) * mm, v(-29.78, 38.38) * mm, v(-29.76, 38) * mm]});
            skFitSpline(sketch, "E730", {"points": [v(-29.76, 38) * mm, v(-29.75, 37.77) * mm, v(-29.4, 36.42) * mm, v(-28.99, 35) * mm]});
            skFitSpline(sketch, "E731", {"points": [v(-28.99, 35) * mm, v(-27.63, 30.33) * mm, v(-26.51, 24.47) * mm, v(-26.03, 19.5) * mm]});
            skFitSpline(sketch, "E732", {"points": [v(-26.03, 19.5) * mm, v(-25.83, 17.37) * mm, v(-25.88, 1.88) * mm, v(-26.1, 1.15) * mm]});
            skFitSpline(sketch, "E733", {"points": [v(-26.1, 1.15) * mm, v(-26.22, 0.73) * mm, v(-26.16, 0.7) * mm, v(-23.59, -0.49) * mm]});
            skFitSpline(sketch, "E734", {"points": [v(-23.59, -0.49) * mm, v(-20.4, -1.95) * mm, v(-14.42, -5) * mm, v(-10.2, -7.3) * mm]});
            skFitSpline(sketch, "E735", {"points": [v(-10.2, -7.3) * mm, v(-6.99, -9.04) * mm, v(-6.48, -9.24) * mm, v(-4.28, -9.59) * mm]});
            skFitSpline(sketch, "E736", {"points": [v(-4.28, -9.59) * mm, v(-2.67, -9.84) * mm, v(2.1, -9.89) * mm, v(3.72, -9.66) * mm]});
            skLineSegment(sketch, "E737", {"start": v(4.6, 12.02) * mm, "end": v(-0.03, 11.35) * mm});
            skLineSegment(sketch, "E738", {"start": v(-0.03, 11.35) * mm, "end": v(-4.66, 12.02) * mm});
            skFitSpline(sketch, "E739", {"points": [v(-34.71, -3.2) * mm, v(-34.62, -2.87) * mm, v(-34.17, -1.07) * mm, v(-33.7, 0.78) * mm]});
            skFitSpline(sketch, "E740", {"points": [v(-32.31, 39.9) * mm, v(-31.26, 40.88) * mm, v(-23.3, 44.73) * mm, v(-20.28, 45.72) * mm]});
            skFitSpline(sketch, "E741", {"points": [v(-20.28, 45.72) * mm, v(-17.02, 46.79) * mm, v(-13, 47.48) * mm, v(-12.03, 47.14) * mm]});
            skFitSpline(sketch, "E742", {"points": [v(-12.03, 47.14) * mm, v(-11.33, 46.9) * mm, v(-11.19, 46.54) * mm, v(-10.93, 44.38) * mm]});
            skFitSpline(sketch, "E743", {"points": [v(-10.93, 44.38) * mm, v(-10.81, 43.34) * mm, v(-10.67, 42.42) * mm, v(-10.61, 42.33) * mm]});
            skFitSpline(sketch, "E744", {"points": [v(-10.61, 42.33) * mm, v(-10.48, 42.1) * mm, v(10.4, 42.1) * mm, v(10.55, 42.33) * mm]});
            skFitSpline(sketch, "E745", {"points": [v(10.55, 42.33) * mm, v(10.6, 42.42) * mm, v(10.75, 43.34) * mm, v(10.87, 44.38) * mm]});
            skFitSpline(sketch, "E746", {"points": [v(10.87, 44.38) * mm, v(11.12, 46.54) * mm, v(11.26, 46.9) * mm, v(11.96, 47.14) * mm]});
            skFitSpline(sketch, "E747", {"points": [v(11.96, 47.14) * mm, v(13.09, 47.53) * mm, v(18.02, 46.56) * mm, v(21.55, 45.25) * mm]});
            skFitSpline(sketch, "E748", {"points": [v(21.55, 45.25) * mm, v(23.83, 44.41) * mm, v(31.8, 40.45) * mm, v(32.3, 39.9) * mm]});
            skLineSegment(sketch, "E749", {"start": v(-33.7, 0.78) * mm, "end": v(-32.86, 4.15) * mm});
            skLineSegment(sketch, "E750", {"start": v(-32.86, 4.15) * mm, "end": v(-32.86, 21.76) * mm});
            skLineSegment(sketch, "E751", {"start": v(-32.86, 21.76) * mm, "end": v(-32.86, 39.37) * mm});
            skLineSegment(sketch, "E752", {"start": v(-32.86, 39.37) * mm, "end": v(-32.31, 39.9) * mm});
            skFitSpline(sketch, "E753", {"points": [v(33.83, -0.14) * mm, v(34.34, -2.1) * mm, v(34.81, -3.74) * mm, v(34.87, -3.8) * mm]});
            skFitSpline(sketch, "E754", {"points": [v(34.87, -3.8) * mm, v(35.07, -4) * mm, v(35.32, -3.52) * mm, v(35.88, -1.87) * mm]});
            skFitSpline(sketch, "E755", {"points": [v(35.88, -1.87) * mm, v(36.55, 0.12) * mm, v(36.99, 2.1) * mm, v(37.44, 5.17) * mm]});
            skFitSpline(sketch, "E756", {"points": [v(37.44, 5.17) * mm, v(38.73, 13.77) * mm, v(37.96, 19.33) * mm, v(35.06, 22.48) * mm]});
            skLineSegment(sketch, "E757", {"start": v(32.3, 39.9) * mm, "end": v(32.72, 39.47) * mm});
            skLineSegment(sketch, "E758", {"start": v(32.72, 39.47) * mm, "end": v(32.8, 21.44) * mm});
            skLineSegment(sketch, "E759", {"start": v(32.8, 21.44) * mm, "end": v(32.9, 3.42) * mm});
            skLineSegment(sketch, "E760", {"start": v(32.9, 3.42) * mm, "end": v(33.83, -0.14) * mm});
            skFitSpline(sketch, "E761", {"points": [v(34.07, 25.35) * mm, v(34.02, 26.4) * mm, v(33.89, 30.96) * mm, v(33.79, 35.5) * mm]});
            skFitSpline(sketch, "E762", {"points": [v(33.79, 35.5) * mm, v(33.58, 45.07) * mm, v(33.52, 45.58) * mm, v(32.3, 48.1) * mm]});
            skFitSpline(sketch, "E763", {"points": [v(32.3, 48.1) * mm, v(28.89, 55.14) * mm, v(20, 60.04) * mm, v(7.22, 61.94) * mm]});
            skFitSpline(sketch, "E764", {"points": [v(7.22, 61.94) * mm, v(4.33, 62.37) * mm, v(-4.42, 62.37) * mm, v(-7.28, 61.94) * mm]});
            skFitSpline(sketch, "E765", {"points": [v(-7.28, 61.94) * mm, v(-17.05, 60.47) * mm, v(-24.2, 57.46) * mm, v(-28.88, 52.83) * mm]});
            skFitSpline(sketch, "E766", {"points": [v(-28.88, 52.83) * mm, v(-31.12, 50.62) * mm, v(-32.38, 48.64) * mm, v(-33.2, 46.08) * mm]});
            skFitSpline(sketch, "E767", {"points": [v(-33.2, 46.08) * mm, v(-33.55, 44.97) * mm, v(-33.58, 44.38) * mm, v(-33.87, 34.2) * mm]});
            skLineSegment(sketch, "E768", {"start": v(35.06, 22.48) * mm, "end": v(34.17, 23.45) * mm});
            skLineSegment(sketch, "E769", {"start": v(34.17, 23.45) * mm, "end": v(34.07, 25.35) * mm});
            skFitSpline(sketch, "E770", {"points": [v(-35.1, 22.48) * mm, v(-36.9, 20.55) * mm, v(-37.72, 18.21) * mm, v(-38.02, 14.28) * mm]});
            skFitSpline(sketch, "E771", {"points": [v(-38.02, 14.28) * mm, v(-38.35, 10.04) * mm, v(-37.4, 2.4) * mm, v(-36.04, -1.53) * mm]});
            skFitSpline(sketch, "E772", {"points": [v(-36.04, -1.53) * mm, v(-35.15, -4.15) * mm, v(-35, -4.32) * mm, v(-34.71, -3.2) * mm]});
            skLineSegment(sketch, "E773", {"start": v(-33.87, 34.2) * mm, "end": v(-34.16, 23.5) * mm});
            skLineSegment(sketch, "E774", {"start": v(-34.16, 23.5) * mm, "end": v(-35.1, 22.48) * mm});
            skFitSpline(sketch, "E775", {"points": [v(4.13, 14.67) * mm, v(6, 14.94) * mm, v(7.59, 15.23) * mm, v(7.65, 15.3) * mm]});
            skFitSpline(sketch, "E776", {"points": [v(7.65, 15.3) * mm, v(7.8, 15.47) * mm, v(10.33, 39.14) * mm, v(10.21, 39.33) * mm]});
            skFitSpline(sketch, "E777", {"points": [v(10.21, 39.33) * mm, v(10.09, 39.54) * mm, v(-10.04, 39.56) * mm, v(-10.24, 39.36) * mm]});
            skFitSpline(sketch, "E778", {"points": [v(-10.24, 39.36) * mm, v(-10.36, 39.24) * mm, v(-8.02, 16.57) * mm, v(-7.78, 15.55) * mm]});
            skFitSpline(sketch, "E779", {"points": [v(-7.78, 15.55) * mm, v(-7.72, 15.27) * mm, v(-7.54, 15.16) * mm, v(-7, 15.08) * mm]});
            skFitSpline(sketch, "E780", {"points": [v(-7, 15.08) * mm, v(-6.6, 15.02) * mm, v(-4.9, 14.77) * mm, v(-3.2, 14.5) * mm]});
            skFitSpline(sketch, "E781", {"points": [v(-3.2, 14.5) * mm, v(-1.5, 14.25) * mm, v(0.07, 14.07) * mm, v(0.3, 14.1) * mm]});
            skFitSpline(sketch, "E782", {"points": [v(0.3, 14.1) * mm, v(0.53, 14.14) * mm, v(2.25, 14.4) * mm, v(4.13, 14.67) * mm]});
            skFitSpline(sketch, "E783", {"points": [v(-12.03, -64.73) * mm, v(-15.7, -64.18) * mm, v(-17.12, -63.44) * mm, v(-19.05, -61.07) * mm]});
            skFitSpline(sketch, "E784", {"points": [v(-19.05, -61.07) * mm, v(-20.28, -59.57) * mm, v(-32.52, -40.3) * mm, v(-32.62, -39.7) * mm]});
            skFitSpline(sketch, "E785", {"points": [v(-32.62, -39.7) * mm, v(-32.66, -39.45) * mm, v(-32.96, -35.57) * mm, v(-33.28, -31.08) * mm]});
            skFitSpline(sketch, "E786", {"points": [v(-33.28, -31.08) * mm, v(-34, -21) * mm, v(-34.15, -19.35) * mm, v(-34.47, -17.25) * mm]});
            skFitSpline(sketch, "E787", {"points": [v(-34.47, -17.25) * mm, v(-34.78, -15.2) * mm, v(-35.68, -11.57) * mm, v(-36.35, -9.64) * mm]});
            skFitSpline(sketch, "E788", {"points": [v(-36.35, -9.64) * mm, v(-36.75, -8.49) * mm, v(-36.83, -8.04) * mm, v(-36.75, -7.37) * mm]});
            skFitSpline(sketch, "E789", {"points": [v(-36.75, -7.37) * mm, v(-36.67, -6.68) * mm, v(-36.73, -6.43) * mm, v(-37.08, -5.81) * mm]});
            skFitSpline(sketch, "E790", {"points": [v(-37.08, -5.81) * mm, v(-38.43, -3.5) * mm, v(-39.54, 0.62) * mm, v(-40.3, 6.17) * mm]});
            skFitSpline(sketch, "E791", {"points": [v(-40.3, 6.17) * mm, v(-40.67, 8.82) * mm, v(-40.72, 15) * mm, v(-40.39, 16.83) * mm]});
            skFitSpline(sketch, "E792", {"points": [v(-40.39, 16.83) * mm, v(-39.86, 19.7) * mm, v(-38.94, 21.93) * mm, v(-37.54, 23.67) * mm]});
            skFitSpline(sketch, "E793", {"points": [v(-37.54, 23.67) * mm, v(-36.78, 24.62) * mm, v(-36.7, 24.8) * mm, v(-36.7, 25.57) * mm]});
            skFitSpline(sketch, "E794", {"points": [v(-36.7, 25.57) * mm, v(-36.7, 26.03) * mm, v(-36.58, 30.53) * mm, v(-36.44, 35.57) * mm]});
            skFitSpline(sketch, "E795", {"points": [v(-36.44, 35.57) * mm, v(-36.18, 45.05) * mm, v(-36.12, 45.74) * mm, v(-35.36, 47.8) * mm]});
            skFitSpline(sketch, "E796", {"points": [v(-35.36, 47.8) * mm, v(-34.44, 50.25) * mm, v(-33, 52.4) * mm, v(-30.71, 54.66) * mm]});
            skFitSpline(sketch, "E797", {"points": [v(-30.71, 54.66) * mm, v(-25.54, 59.8) * mm, v(-17.36, 63.25) * mm, v(-7.12, 64.6) * mm]});
            skFitSpline(sketch, "E798", {"points": [v(-7.12, 64.6) * mm, v(-4.06, 65.01) * mm, v(4, 65.01) * mm, v(7.05, 64.6) * mm]});
            skFitSpline(sketch, "E799", {"points": [v(7.05, 64.6) * mm, v(20.92, 62.77) * mm, v(30.99, 57.08) * mm, v(34.8, 48.94) * mm]});
            skFitSpline(sketch, "E800", {"points": [v(34.8, 48.94) * mm, v(36.05, 46.3) * mm, v(36.1, 45.79) * mm, v(36.38, 35.8) * mm]});
            skFitSpline(sketch, "E801", {"points": [v(36.38, 35.8) * mm, v(36.52, 30.92) * mm, v(36.63, 26.41) * mm, v(36.63, 25.8) * mm]});
            skFitSpline(sketch, "E802", {"points": [v(36.63, 25.8) * mm, v(36.63, 24.73) * mm, v(36.66, 24.66) * mm, v(37.37, 23.83) * mm]});
            skFitSpline(sketch, "E803", {"points": [v(37.37, 23.83) * mm, v(38.86, 22.08) * mm, v(39.9, 19.47) * mm, v(40.37, 16.3) * mm]});
            skFitSpline(sketch, "E804", {"points": [v(40.37, 16.3) * mm, v(41.29, 10.11) * mm, v(39.6, -1.22) * mm, v(37.12, -5.63) * mm]});
            skFitSpline(sketch, "E805", {"points": [v(37.12, -5.63) * mm, v(36.66, -6.45) * mm, v(36.61, -6.65) * mm, v(36.7, -7.42) * mm]});
            skFitSpline(sketch, "E806", {"points": [v(36.7, -7.42) * mm, v(36.8, -8.12) * mm, v(36.73, -8.5) * mm, v(36.38, -9.43) * mm]});
            skFitSpline(sketch, "E807", {"points": [v(36.38, -9.43) * mm, v(35.76, -11.07) * mm, v(34.86, -14.58) * mm, v(34.47, -16.89) * mm]});
            skFitSpline(sketch, "E808", {"points": [v(34.47, -16.89) * mm, v(34.2, -18.5) * mm, v(33.53, -26.6) * mm, v(32.7, -38.37) * mm]});
            skFitSpline(sketch, "E809", {"points": [v(26.29, -49.92) * mm, v(22.82, -55.38) * mm, v(19.6, -60.32) * mm, v(19.13, -60.91) * mm]});
            skFitSpline(sketch, "E810", {"points": [v(19.13, -60.91) * mm, v(17.35, -63.16) * mm, v(16.18, -63.88) * mm, v(13.35, -64.52) * mm]});
            skFitSpline(sketch, "E811", {"points": [v(13.18, -64.52) * mm, v(11.6, -64.88) * mm, v(11.21, -64.89) * mm, v(0.47, -64.93) * mm]});
            skFitSpline(sketch, "E812", {"points": [v(0.63, -64.93) * mm, v(-8.35, -64.97) * mm, v(-10.75, -64.93) * mm, v(-12.03, -64.73) * mm]});
            skLineSegment(sketch, "E813", {"start": v(32.7, -38.37) * mm, "end": v(32.59, -40) * mm});
            skLineSegment(sketch, "E814", {"start": v(32.59, -40) * mm, "end": v(26.29, -49.92) * mm});
            skFitSpline(sketch, "E815", {"points": [v(9.07, -62.5) * mm, v(11.46, -62.3) * mm, v(14.26, -61.78) * mm, v(15, -61.4) * mm]});
            skFitSpline(sketch, "E816", {"points": [v(15, -61.4) * mm, v(15.63, -61.07) * mm, v(16.8, -59.85) * mm, v(17.72, -58.58) * mm]});
            skFitSpline(sketch, "E817", {"points": [v(17.72, -58.58) * mm, v(18.11, -58.03) * mm, v(21.06, -53.44) * mm, v(24.27, -48.37) * mm]});
            skFitSpline(sketch, "E818", {"points": [v(30.21, -37.62) * mm, v(30.27, -36.78) * mm, v(30.57, -32.74) * mm, v(30.87, -28.67) * mm]});
            skFitSpline(sketch, "E819", {"points": [v(30.87, -28.67) * mm, v(31.18, -24.59) * mm, v(31.37, -21.19) * mm, v(31.3, -21.11) * mm]});
            skFitSpline(sketch, "E820", {"points": [v(31.3, -21.11) * mm, v(31.23, -21.03) * mm, v(30.82, -21.56) * mm, v(30.4, -22.28) * mm]});
            skFitSpline(sketch, "E821", {"points": [v(30.4, -22.28) * mm, v(29.97, -23) * mm, v(28.6, -25) * mm, v(27.37, -26.73) * mm]});
            skFitSpline(sketch, "E822", {"points": [v(27.37, -26.73) * mm, v(24.1, -31.33) * mm, v(22.78, -33.8) * mm, v(20.81, -39.04) * mm]});
            skLineSegment(sketch, "E823", {"start": v(24.27, -48.37) * mm, "end": v(30.1, -39.17) * mm});
            skLineSegment(sketch, "E824", {"start": v(30.1, -39.17) * mm, "end": v(30.21, -37.62) * mm});
            skFitSpline(sketch, "E825", {"points": [v(20.55, -48.26) * mm, v(19.56, -50.79) * mm, v(17.6, -54.5) * mm, v(16.82, -55.34) * mm]});
            skFitSpline(sketch, "E826", {"points": [v(16.82, -55.34) * mm, v(15.53, -56.72) * mm, v(14.01, -56.82) * mm, v(10.93, -55.75) * mm]});
            skFitSpline(sketch, "E827", {"points": [v(10.93, -55.75) * mm, v(10.28, -55.52) * mm, v(9.69, -55.33) * mm, v(9.62, -55.33) * mm]});
            skFitSpline(sketch, "E828", {"points": [v(9.62, -55.33) * mm, v(9.55, -55.33) * mm, v(9.26, -56.04) * mm, v(8.97, -56.91) * mm]});
            skFitSpline(sketch, "E829", {"points": [v(8.97, -56.91) * mm, v(8.15, -59.37) * mm, v(8.97, -59.16) * mm, v(-0.01, -59.16) * mm]});
            skFitSpline(sketch, "E830", {"points": [v(-0.01, -59.16) * mm, v(-7.13, -59.16) * mm, v(-7.64, -59.15) * mm, v(-8.03, -58.86) * mm]});
            skFitSpline(sketch, "E831", {"points": [v(-8.03, -58.86) * mm, v(-8.31, -58.65) * mm, v(-8.63, -58.06) * mm, v(-8.98, -57.07) * mm]});
            skFitSpline(sketch, "E832", {"points": [v(-8.98, -57.07) * mm, v(-9.27, -56.25) * mm, v(-9.54, -55.51) * mm, v(-9.57, -55.43) * mm]});
            skFitSpline(sketch, "E833", {"points": [v(-9.57, -55.43) * mm, v(-9.6, -55.35) * mm, v(-10.22, -55.48) * mm, v(-10.93, -55.72) * mm]});
            skFitSpline(sketch, "E834", {"points": [v(-10.93, -55.72) * mm, v(-12.84, -56.38) * mm, v(-14.47, -56.6) * mm, v(-15.44, -56.33) * mm]});
            skFitSpline(sketch, "E835", {"points": [v(-15.44, -56.33) * mm, v(-16.82, -55.95) * mm, v(-18.04, -54.16) * mm, v(-19.97, -49.68) * mm]});
            skLineSegment(sketch, "E836", {"start": v(20.81, -39.04) * mm, "end": v(19.95, -41.34) * mm});
            skLineSegment(sketch, "E837", {"start": v(19.95, -41.34) * mm, "end": v(20.48, -44.22) * mm});
            skLineSegment(sketch, "E838", {"start": v(20.48, -44.22) * mm, "end": v(21, -47.11) * mm});
            skLineSegment(sketch, "E839", {"start": v(21, -47.11) * mm, "end": v(20.55, -48.26) * mm});
            skFitSpline(sketch, "E840", {"points": [v(-20.68, -39.54) * mm, v(-22.39, -34.78) * mm, v(-24.23, -31.12) * mm, v(-26.17, -28.62) * mm]});
            skFitSpline(sketch, "E841", {"points": [v(-26.17, -28.62) * mm, v(-27, -27.57) * mm, v(-30.37, -22.5) * mm, v(-30.91, -21.5) * mm]});
            skFitSpline(sketch, "E842", {"points": [v(-30.91, -21.5) * mm, v(-31.08, -21.19) * mm, v(-31.27, -21.01) * mm, v(-31.35, -21.1) * mm]});
            skFitSpline(sketch, "E843", {"points": [v(-31.35, -21.1) * mm, v(-31.42, -21.18) * mm, v(-31.2, -25.04) * mm, v(-30.85, -29.67) * mm]});
            skFitSpline(sketch, "E844", {"points": [v(-30.85, -29.67) * mm, v(-30.5, -34.3) * mm, v(-30.21, -38.31) * mm, v(-30.2, -38.6) * mm]});
            skFitSpline(sketch, "E845", {"points": [v(-30.2, -38.6) * mm, v(-30.2, -38.98) * mm, v(-28.61, -41.6) * mm, v(-24.02, -48.84) * mm]});
            skFitSpline(sketch, "E846", {"points": [v(-24.02, -48.84) * mm, v(-20.63, -54.19) * mm, v(-17.58, -58.9) * mm, v(-17.25, -59.3) * mm]});
            skFitSpline(sketch, "E847", {"points": [v(-17.25, -59.3) * mm, v(-16.42, -60.3) * mm, v(-15.53, -61.15) * mm, v(-15.01, -61.42) * mm]});
            skFitSpline(sketch, "E848", {"points": [v(-15.01, -61.42) * mm, v(-14.37, -61.76) * mm, v(-11.44, -62.32) * mm, v(-9.5, -62.48) * mm]});
            skFitSpline(sketch, "E849", {"points": [v(-9.5, -62.48) * mm, v(-7, -62.68) * mm, v(6.56, -62.7) * mm, v(9.07, -62.5) * mm]});
            skLineSegment(sketch, "E850", {"start": v(-19.97, -49.68) * mm, "end": v(-21.06, -47.17) * mm});
            skLineSegment(sketch, "E851", {"start": v(-21.06, -47.17) * mm, "end": v(-20.54, -44.28) * mm});
            skLineSegment(sketch, "E852", {"start": v(-20.54, -44.28) * mm, "end": v(-20.02, -41.38) * mm});
            skLineSegment(sketch, "E853", {"start": v(-20.02, -41.38) * mm, "end": v(-20.68, -39.54) * mm});
            skFitSpline(sketch, "E854", {"points": [v(6.36, -56.4) * mm, v(6.66, -56.12) * mm, v(6.89, -55.1) * mm, v(6.72, -54.84) * mm]});
            skFitSpline(sketch, "E855", {"points": [v(6.72, -54.84) * mm, v(6.65, -54.72) * mm, v(4.49, -54.66) * mm, v(-0.03, -54.66) * mm]});
            skFitSpline(sketch, "E856", {"points": [v(-0.03, -54.66) * mm, v(-4.55, -54.66) * mm, v(-6.71, -54.72) * mm, v(-6.79, -54.84) * mm]});
            skFitSpline(sketch, "E857", {"points": [v(-6.79, -54.84) * mm, v(-6.95, -55.1) * mm, v(-6.72, -56.12) * mm, v(-6.43, -56.4) * mm]});
            skFitSpline(sketch, "E858", {"points": [v(-6.43, -56.4) * mm, v(-6.05, -56.8) * mm, v(5.98, -56.8) * mm, v(6.36, -56.4) * mm]});
            skFitSpline(sketch, "E859", {"points": [v(-11.75, -53.3) * mm, v(-10.99, -53.02) * mm, v(-10.32, -52.73) * mm, v(-10.27, -52.64) * mm]});
            skFitSpline(sketch, "E860", {"points": [v(-10.27, -52.64) * mm, v(-10.15, -52.45) * mm, v(-11.33, -48) * mm, v(-11.58, -47.7) * mm]});
            skFitSpline(sketch, "E861", {"points": [v(-11.58, -47.7) * mm, v(-11.72, -47.53) * mm, v(-12, -47.73) * mm, v(-12.88, -48.6) * mm]});
            skFitSpline(sketch, "E862", {"points": [v(-12.88, -48.6) * mm, v(-14.07, -49.78) * mm, v(-14.67, -50) * mm, v(-15.28, -49.5) * mm]});
            skFitSpline(sketch, "E863", {"points": [v(-15.28, -49.5) * mm, v(-15.43, -49.37) * mm, v(-16.08, -48.38) * mm, v(-16.73, -47.28) * mm]});
            skFitSpline(sketch, "E864", {"points": [v(-16.73, -47.28) * mm, v(-17.96, -45.2) * mm, v(-18.15, -45.07) * mm, v(-18.31, -46.3) * mm]});
            skFitSpline(sketch, "E865", {"points": [v(-18.31, -46.3) * mm, v(-18.39, -46.85) * mm, v(-18.25, -47.3) * mm, v(-17.47, -49.08) * mm]});
            skFitSpline(sketch, "E866", {"points": [v(-17.47, -49.08) * mm, v(-16.43, -51.46) * mm, v(-15.5, -53.2) * mm, v(-15, -53.7) * mm]});
            skFitSpline(sketch, "E867", {"points": [v(-15, -53.7) * mm, v(-14.58, -54.12) * mm, v(-13.72, -54.01) * mm, v(-11.75, -53.3) * mm]});
            skFitSpline(sketch, "E868", {"points": [v(15.06, -53.55) * mm, v(15.48, -53.1) * mm, v(17.27, -49.57) * mm, v(17.97, -47.81) * mm]});
            skFitSpline(sketch, "E869", {"points": [v(17.97, -47.81) * mm, v(18.26, -47.08) * mm, v(18.32, -46.7) * mm, v(18.23, -46.1) * mm]});
            skFitSpline(sketch, "E870", {"points": [v(18.23, -46.1) * mm, v(18.16, -45.68) * mm, v(18.05, -45.33) * mm, v(17.97, -45.33) * mm]});
            skFitSpline(sketch, "E871", {"points": [v(17.97, -45.33) * mm, v(17.89, -45.33) * mm, v(17.3, -46.22) * mm, v(16.66, -47.3) * mm]});
            skFitSpline(sketch, "E872", {"points": [v(16.66, -47.3) * mm, v(16.02, -48.38) * mm, v(15.37, -49.37) * mm, v(15.22, -49.5) * mm]});
            skFitSpline(sketch, "E873", {"points": [v(15.22, -49.5) * mm, v(14.6, -50) * mm, v(14, -49.78) * mm, v(12.82, -48.6) * mm]});
            skFitSpline(sketch, "E874", {"points": [v(12.82, -48.6) * mm, v(11.94, -47.72) * mm, v(11.65, -47.53) * mm, v(11.51, -47.7) * mm]});
            skFitSpline(sketch, "E875", {"points": [v(11.51, -47.7) * mm, v(11.37, -47.87) * mm, v(10.13, -52.26) * mm, v(10.13, -52.6) * mm]});
            skFitSpline(sketch, "E876", {"points": [v(10.13, -52.6) * mm, v(10.13, -52.83) * mm, v(13.52, -53.97) * mm, v(14.27, -53.99) * mm]});
            skFitSpline(sketch, "E877", {"points": [v(14.27, -53.99) * mm, v(14.48, -54) * mm, v(14.84, -53.8) * mm, v(15.06, -53.55) * mm]});
            skFitSpline(sketch, "E878", {"points": [v(7.77, -51.41) * mm, v(8.24, -49.97) * mm, v(9.12, -46.44) * mm, v(9.03, -46.3) * mm]});
            skFitSpline(sketch, "E879", {"points": [v(9.03, -46.3) * mm, v(8.92, -46.13) * mm, v(-8.98, -46.12) * mm, v(-9.1, -46.3) * mm]});
            skFitSpline(sketch, "E880", {"points": [v(-9.1, -46.3) * mm, v(-9.18, -46.44) * mm, v(-7.83, -51.66) * mm, v(-7.62, -51.99) * mm]});
            skFitSpline(sketch, "E881", {"points": [v(-7.62, -51.99) * mm, v(-7.54, -52.11) * mm, v(-5.2, -52.15) * mm, v(0.02, -52.12) * mm]});
            skFitSpline(sketch, "E882", {"points": [v(-13.3, -45.43) * mm, v(-12.97, -45.02) * mm, v(-12.7, -44.6) * mm, v(-12.7, -44.5) * mm]});
            skFitSpline(sketch, "E883", {"points": [v(-12.7, -44.5) * mm, v(-12.7, -44.18) * mm, v(-13.48, -42.79) * mm, v(-14.33, -41.58) * mm]});
            skFitSpline(sketch, "E884", {"points": [v(-14.33, -41.58) * mm, v(-15.3, -40.21) * mm, v(-18.6, -36.7) * mm, v(-18.78, -36.86) * mm]});
            skFitSpline(sketch, "E885", {"points": [v(-18.78, -36.86) * mm, v(-18.84, -36.92) * mm, v(-18.58, -37.86) * mm, v(-18.2, -38.94) * mm]});
            skFitSpline(sketch, "E886", {"points": [v(-18.2, -38.94) * mm, v(-17.4, -41.23) * mm, v(-14.65, -46.16) * mm, v(-14.18, -46.16) * mm]});
            skFitSpline(sketch, "E887", {"points": [v(-14.18, -46.16) * mm, v(-14.03, -46.16) * mm, v(-13.63, -45.83) * mm, v(-13.3, -45.43) * mm]});
            skLineSegment(sketch, "E888", {"start": v(0.02, -52.12) * mm, "end": v(7.55, -52.08) * mm});
            skLineSegment(sketch, "E889", {"start": v(7.55, -52.08) * mm, "end": v(7.77, -51.41) * mm});
            skFitSpline(sketch, "E890", {"points": [v(15.88, -43.64) * mm, v(16.87, -41.94) * mm, v(17.6, -40.45) * mm, v(18.08, -39.13) * mm]});
            skFitSpline(sketch, "E891", {"points": [v(18.08, -39.13) * mm, v(18.96, -36.7) * mm, v(18.99, -36.43) * mm, v(18.28, -37.1) * mm]});
            skFitSpline(sketch, "E892", {"points": [v(18.28, -37.1) * mm, v(16.9, -38.38) * mm, v(14.35, -41.39) * mm, v(13.61, -42.58) * mm]});
            skFitSpline(sketch, "E893", {"points": [v(13.61, -42.58) * mm, v(12.48, -44.4) * mm, v(12.47, -44.5) * mm, v(13.24, -45.4) * mm]});
            skFitSpline(sketch, "E894", {"points": [v(13.24, -45.4) * mm, v(13.6, -45.82) * mm, v(14, -46.16) * mm, v(14.14, -46.16) * mm]});
            skFitSpline(sketch, "E895", {"points": [v(14.14, -46.16) * mm, v(14.3, -46.16) * mm, v(14.98, -45.17) * mm, v(15.88, -43.64) * mm]});
            skFitSpline(sketch, "E896", {"points": [v(10.57, -42.79) * mm, v(11.77, -40.41) * mm, v(12.61, -39.37) * mm, v(17.46, -34.25) * mm]});
            skFitSpline(sketch, "E897", {"points": [v(17.46, -34.25) * mm, v(22.04, -29.4) * mm, v(22.84, -28.5) * mm, v(24.54, -26.25) * mm]});
            skFitSpline(sketch, "E898", {"points": [v(24.54, -26.25) * mm, v(26.94, -23.08) * mm, v(27.37, -21.78) * mm, v(27.63, -16.83) * mm]});
            skFitSpline(sketch, "E899", {"points": [v(27.63, -16.83) * mm, v(27.72, -15.14) * mm, v(27.88, -12.83) * mm, v(28, -11.7) * mm]});
            skFitSpline(sketch, "E900", {"points": [v(28, -11.7) * mm, v(28.1, -10.59) * mm, v(28.14, -9.62) * mm, v(28.08, -9.56) * mm]});
            skFitSpline(sketch, "E901", {"points": [v(28.08, -9.56) * mm, v(28.02, -9.5) * mm, v(27.45, -9.95) * mm, v(26.8, -10.55) * mm]});
            skFitSpline(sketch, "E902", {"points": [v(26.8, -10.55) * mm, v(24.83, -12.42) * mm, v(22.15, -13.77) * mm, v(18.8, -14.6) * mm]});
            skFitSpline(sketch, "E903", {"points": [v(18.8, -14.6) * mm, v(16.12, -15.25) * mm, v(10.8, -16.2) * mm, v(10.37, -16.1) * mm]});
            skFitSpline(sketch, "E904", {"points": [v(10.37, -16.1) * mm, v(9.86, -15.97) * mm, v(8.25, -14.04) * mm, v(7.62, -12.8) * mm]});
            skFitSpline(sketch, "E905", {"points": [v(7.62, -12.8) * mm, v(7.3, -12.18) * mm, v(7.02, -11.83) * mm, v(6.84, -11.83) * mm]});
            skFitSpline(sketch, "E906", {"points": [v(6.84, -11.83) * mm, v(6.68, -11.83) * mm, v(5.88, -11.96) * mm, v(5.05, -12.12) * mm]});
            skFitSpline(sketch, "E907", {"points": [v(5.05, -12.12) * mm, v(2.94, -12.52) * mm, v(-3, -12.52) * mm, v(-5.12, -12.12) * mm]});
            skFitSpline(sketch, "E908", {"points": [v(-5.12, -12.12) * mm, v(-5.94, -11.96) * mm, v(-6.74, -11.83) * mm, v(-6.9, -11.83) * mm]});
            skFitSpline(sketch, "E909", {"points": [v(-6.9, -11.83) * mm, v(-7.06, -11.83) * mm, v(-7.32, -12.15) * mm, v(-7.54, -12.6) * mm]});
            skFitSpline(sketch, "E910", {"points": [v(-7.54, -12.6) * mm, v(-8.03, -13.62) * mm, v(-9.77, -15.8) * mm, v(-10.27, -16.03) * mm]});
            skFitSpline(sketch, "E911", {"points": [v(-10.27, -16.03) * mm, v(-10.7, -16.22) * mm, v(-13.38, -15.8) * mm, v(-17.8, -14.83) * mm]});
            skFitSpline(sketch, "E912", {"points": [v(-17.8, -14.83) * mm, v(-21.81, -13.96) * mm, v(-24.63, -12.64) * mm, v(-26.81, -10.6) * mm]});
            skFitSpline(sketch, "E913", {"points": [v(-26.81, -10.6) * mm, v(-27.49, -9.97) * mm, v(-28.09, -9.5) * mm, v(-28.15, -9.56) * mm]});
            skFitSpline(sketch, "E914", {"points": [v(-28.15, -9.56) * mm, v(-28.2, -9.61) * mm, v(-28.16, -10.54) * mm, v(-28.05, -11.62) * mm]});
            skFitSpline(sketch, "E915", {"points": [v(-28.05, -11.62) * mm, v(-27.94, -12.7) * mm, v(-27.78, -14.93) * mm, v(-27.7, -16.58) * mm]});
            skFitSpline(sketch, "E916", {"points": [v(-27.7, -16.58) * mm, v(-27.42, -21.84) * mm, v(-27.1, -22.84) * mm, v(-24.56, -26.42) * mm]});
            skFitSpline(sketch, "E917", {"points": [v(-24.56, -26.42) * mm, v(-22.65, -29.1) * mm, v(-21.96, -29.88) * mm, v(-17.11, -34.83) * mm]});
            skFitSpline(sketch, "E918", {"points": [v(-17.11, -34.83) * mm, v(-12.95, -39.07) * mm, v(-11.76, -40.53) * mm, v(-10.63, -42.79) * mm]});
            skFitSpline(sketch, "E919", {"points": [v(-30.44, -13.89) * mm, v(-30.84, -8.35) * mm, v(-30.56, -5.36) * mm, v(-29.15, -0.17) * mm]});
            skLineSegment(sketch, "E920", {"start": v(-10.63, -42.79) * mm, "end": v(-10.2, -43.66) * mm});
            skLineSegment(sketch, "E921", {"start": v(-10.2, -43.66) * mm, "end": v(-0.03, -43.66) * mm});
            skLineSegment(sketch, "E922", {"start": v(-0.03, -43.66) * mm, "end": v(10.13, -43.66) * mm});
            skLineSegment(sketch, "E923", {"start": v(10.13, -43.66) * mm, "end": v(10.57, -42.79) * mm});
            skFitSpline(sketch, "E924", {"points": [v(-28.45, 10.33) * mm, v(-28.46, 18.68) * mm, v(-28.55, 20.18) * mm, v(-29.38, 25) * mm]});
            skFitSpline(sketch, "E925", {"points": [v(-29.38, 25) * mm, v(-29.83, 27.6) * mm, v(-30.02, 28.28) * mm, v(-30.2, 27.98) * mm]});
            skFitSpline(sketch, "E926", {"points": [v(-30.2, 27.98) * mm, v(-30.3, 27.85) * mm, v(-30.36, 22.48) * mm, v(-30.36, 15.53) * mm]});
            skLineSegment(sketch, "E927", {"start": v(-29.15, -0.17) * mm, "end": v(-28.45, 2.42) * mm});
            skLineSegment(sketch, "E928", {"start": v(-28.45, 2.42) * mm, "end": v(-28.45, 10.33) * mm});
            skFitSpline(sketch, "E929", {"points": [v(-31.95, -2.91) * mm, v(-32.82, -6.33) * mm, v(-33.53, -9.32) * mm, v(-33.53, -9.55) * mm]});
            skFitSpline(sketch, "E930", {"points": [v(-33.53, -9.55) * mm, v(-33.53, -10.3) * mm, v(-30.59, -16.7) * mm, v(-30.39, -16.37) * mm]});
            skFitSpline(sketch, "E931", {"points": [v(-30.39, -16.37) * mm, v(-30.33, -16.27) * mm, v(-30.35, -15.16) * mm, v(-30.44, -13.89) * mm]});
            skLineSegment(sketch, "E932", {"start": v(-30.36, 15.53) * mm, "end": v(-30.36, 3.3) * mm});
            skLineSegment(sketch, "E933", {"start": v(-30.36, 3.3) * mm, "end": v(-31.95, -2.91) * mm});
            skFitSpline(sketch, "E934", {"points": [v(32.11, -13.04) * mm, v(32.86, -11.37) * mm, v(33.47, -9.82) * mm, v(33.47, -9.58) * mm]});
            skFitSpline(sketch, "E935", {"points": [v(33.47, -9.58) * mm, v(33.47, -9.35) * mm, v(32.75, -6.31) * mm, v(31.88, -2.83) * mm]});
            skFitSpline(sketch, "E936", {"points": [v(30.3, 15.74) * mm, v(30.3, 23.32) * mm, v(30.24, 28.02) * mm, v(30.14, 28.08) * mm]});
            skFitSpline(sketch, "E937", {"points": [v(30.14, 28.08) * mm, v(29.94, 28.2) * mm, v(29.73, 27.42) * mm, v(29.3, 24.91) * mm]});
            skFitSpline(sketch, "E938", {"points": [v(29.3, 24.91) * mm, v(28.52, 20.25) * mm, v(28.44, 19) * mm, v(28.35, 10.92) * mm]});
            skLineSegment(sketch, "E939", {"start": v(31.88, -2.83) * mm, "end": v(30.3, 3.5) * mm});
            skLineSegment(sketch, "E940", {"start": v(30.3, 3.5) * mm, "end": v(30.3, 15.74) * mm});
            skFitSpline(sketch, "E941", {"points": [v(28.86, 0.87) * mm, v(30.18, -4) * mm, v(30.72, -7.53) * mm, v(30.57, -10.41) * mm]});
            skFitSpline(sketch, "E942", {"points": [v(30.57, -10.41) * mm, v(30.24, -16.94) * mm, v(30.24, -16.6) * mm, v(30.51, -16.33) * mm]});
            skFitSpline(sketch, "E943", {"points": [v(30.51, -16.33) * mm, v(30.65, -16.2) * mm, v(31.37, -14.72) * mm, v(32.11, -13.04) * mm]});
            skLineSegment(sketch, "E944", {"start": v(28.35, 10.92) * mm, "end": v(28.26, 3.08) * mm});
            skLineSegment(sketch, "E945", {"start": v(28.26, 3.08) * mm, "end": v(28.86, 0.87) * mm});
            skFitSpline(sketch, "E946", {"points": [v(-10.55, -12.62) * mm, v(-9.8, -11.63) * mm, v(-9.5, -10.98) * mm, v(-9.69, -10.69) * mm]});
            skFitSpline(sketch, "E947", {"points": [v(-9.69, -10.69) * mm, v(-9.9, -10.35) * mm, v(-15.32, -7.45) * mm, v(-20.45, -4.93) * mm]});
            skFitSpline(sketch, "E948", {"points": [v(-20.45, -4.93) * mm, v(-26.2, -2.1) * mm, v(-26.31, -2.05) * mm, v(-26.58, -2.32) * mm]});
            skFitSpline(sketch, "E949", {"points": [v(-26.58, -2.32) * mm, v(-26.89, -2.62) * mm, v(-26.8, -5.9) * mm, v(-26.47, -6.8) * mm]});
            skFitSpline(sketch, "E950", {"points": [v(-26.47, -6.8) * mm, v(-25.77, -8.68) * mm, v(-23.55, -10.37) * mm, v(-20.2, -11.58) * mm]});
            skFitSpline(sketch, "E951", {"points": [v(-20.2, -11.58) * mm, v(-19.13, -11.96) * mm, v(-12.34, -13.45) * mm, v(-11.5, -13.49) * mm]});
            skFitSpline(sketch, "E952", {"points": [v(-11.5, -13.49) * mm, v(-11.34, -13.5) * mm, v(-10.92, -13.11) * mm, v(-10.55, -12.62) * mm]});
            skFitSpline(sketch, "E953", {"points": [v(14.88, -12.83) * mm, v(16.78, -12.45) * mm, v(18.94, -11.96) * mm, v(19.7, -11.72) * mm]});
            skFitSpline(sketch, "E954", {"points": [v(19.7, -11.72) * mm, v(22.46, -10.86) * mm, v(25.17, -9.1) * mm, v(26.04, -7.61) * mm]});
            skFitSpline(sketch, "E955", {"points": [v(26.04, -7.61) * mm, v(26.58, -6.7) * mm, v(26.88, -4.77) * mm, v(26.73, -3.3) * mm]});
            skFitSpline(sketch, "E956", {"points": [v(26.73, -3.3) * mm, v(26.64, -2.45) * mm, v(26.54, -2.17) * mm, v(26.35, -2.17) * mm]});
            skFitSpline(sketch, "E957", {"points": [v(26.35, -2.17) * mm, v(25.52, -2.17) * mm, v(10, -10.08) * mm, v(9.62, -10.7) * mm]});
            skFitSpline(sketch, "E958", {"points": [v(9.62, -10.7) * mm, v(9.4, -11.04) * mm, v(10.88, -13.5) * mm, v(11.3, -13.5) * mm]});
            skFitSpline(sketch, "E959", {"points": [v(11.3, -13.5) * mm, v(11.37, -13.5) * mm, v(12.99, -13.2) * mm, v(14.88, -12.83) * mm]});
            skFitSpline(sketch, "E960", {"points": [v(2.82, -9.82) * mm, v(6, -9.5) * mm, v(6.58, -9.3) * mm, v(10.3, -7.29) * mm]});
            skFitSpline(sketch, "E961", {"points": [v(10.3, -7.29) * mm, v(14.3, -5.11) * mm, v(20.78, -1.83) * mm, v(23.95, -0.37) * mm]});
            skFitSpline(sketch, "E962", {"points": [v(26.03, 1.37) * mm, v(25.95, 1.76) * mm, v(25.88, 5.8) * mm, v(25.89, 10.33) * mm]});
            skFitSpline(sketch, "E963", {"points": [v(25.89, 10.33) * mm, v(25.89, 17.23) * mm, v(25.94, 18.98) * mm, v(26.19, 21) * mm]});
            skFitSpline(sketch, "E964", {"points": [v(26.19, 21) * mm, v(26.81, 26.06) * mm, v(27.78, 30.8) * mm, v(29.19, 35.66) * mm]});
            skFitSpline(sketch, "E965", {"points": [v(29.19, 35.66) * mm, v(29.6, 37.08) * mm, v(29.9, 38.31) * mm, v(29.84, 38.4) * mm]});
            skFitSpline(sketch, "E966", {"points": [v(29.84, 38.4) * mm, v(29.67, 38.67) * mm, v(22.07, 42.29) * mm, v(20.38, 42.9) * mm]});
            skFitSpline(sketch, "E967", {"points": [v(20.38, 42.9) * mm, v(18.47, 43.59) * mm, v(15.81, 44.29) * mm, v(14.52, 44.44) * mm]});
            skFitSpline(sketch, "E968", {"points": [v(14.52, 44.44) * mm, v(13.83, 44.52) * mm, v(13.62, 44.49) * mm, v(13.55, 44.3) * mm]});
            skFitSpline(sketch, "E969", {"points": [v(13.55, 44.3) * mm, v(13.5, 44.16) * mm, v(12.71, 37.23) * mm, v(11.81, 28.89) * mm]});
            skFitSpline(sketch, "E970", {"points": [v(11.81, 28.89) * mm, v(10.91, 20.54) * mm, v(10.09, 13.56) * mm, v(9.98, 13.37) * mm]});
            skFitSpline(sketch, "E971", {"points": [v(9.98, 13.37) * mm, v(9.88, 13.17) * mm, v(9.51, 12.93) * mm, v(9.17, 12.84) * mm]});
            skFitSpline(sketch, "E972", {"points": [v(9.17, 12.84) * mm, v(8.36, 12.61) * mm, v(0.7, 11.5) * mm, v(-0.04, 11.5) * mm]});
            skFitSpline(sketch, "E973", {"points": [v(-0.04, 11.5) * mm, v(-0.77, 11.5) * mm, v(-8.4, 12.61) * mm, v(-9.24, 12.84) * mm]});
            skFitSpline(sketch, "E974", {"points": [v(-9.24, 12.84) * mm, v(-9.58, 12.93) * mm, v(-9.94, 13.17) * mm, v(-10.05, 13.36) * mm]});
            skFitSpline(sketch, "E975", {"points": [v(-10.05, 13.36) * mm, v(-10.15, 13.55) * mm, v(-10.97, 20.57) * mm, v(-11.88, 28.97) * mm]});
            skFitSpline(sketch, "E976", {"points": [v(-11.88, 28.97) * mm, v(-12.8, 37.36) * mm, v(-13.6, 44.3) * mm, v(-13.7, 44.4) * mm]});
            skFitSpline(sketch, "E977", {"points": [v(-13.7, 44.4) * mm, v(-14.05, 44.75) * mm, v(-17.66, 43.9) * mm, v(-20.85, 42.72) * mm]});
            skFitSpline(sketch, "E978", {"points": [v(-20.85, 42.72) * mm, v(-22.73, 42.02) * mm, v(-29.33, 38.85) * mm, v(-29.72, 38.45) * mm]});
            skFitSpline(sketch, "E979", {"points": [v(-29.72, 38.45) * mm, v(-29.98, 38.2) * mm, v(-29.97, 38.08) * mm, v(-29.6, 36.88) * mm]});
            skFitSpline(sketch, "E980", {"points": [v(-29.6, 36.88) * mm, v(-27.89, 31.39) * mm, v(-26.66, 25.2) * mm, v(-26.12, 19.41) * mm]});
            skFitSpline(sketch, "E981", {"points": [v(-26.12, 19.41) * mm, v(-25.9, 17.17) * mm, v(-25.86, 15.05) * mm, v(-25.92, 9.17) * mm]});
            skFitSpline(sketch, "E982", {"points": [v(-25.92, 9.17) * mm, v(-25.95, 5.09) * mm, v(-26.04, 1.5) * mm, v(-26.1, 1.2) * mm]});
            skLineSegment(sketch, "E983", {"start": v(23.95, -0.37) * mm, "end": v(26.17, 0.67) * mm});
            skLineSegment(sketch, "E984", {"start": v(26.17, 0.67) * mm, "end": v(26.03, 1.37) * mm});
            skFitSpline(sketch, "E985", {"points": [v(-24.18, -0.29) * mm, v(-20.77, -1.86) * mm, v(-14.85, -4.86) * mm, v(-10.92, -7) * mm]});
            skFitSpline(sketch, "E986", {"points": [v(-10.92, -7) * mm, v(-8.12, -8.52) * mm, v(-6.9, -9.1) * mm, v(-5.92, -9.34) * mm]});
            skFitSpline(sketch, "E987", {"points": [v(-5.92, -9.34) * mm, v(-3.5, -9.95) * mm, v(-0.19, -10.13) * mm, v(2.82, -9.82) * mm]});
            skLineSegment(sketch, "E988", {"start": v(-26.1, 1.2) * mm, "end": v(-26.24, 0.66) * mm});
            skLineSegment(sketch, "E989", {"start": v(-26.24, 0.66) * mm, "end": v(-24.18, -0.29) * mm});
            skFitSpline(sketch, "E990", {"points": [v(-32.88, 21.3) * mm, v(-32.87, 36.33) * mm, v(-32.83, 39.08) * mm, v(-32.63, 39.48) * mm]});
            skFitSpline(sketch, "E991", {"points": [v(-32.63, 39.48) * mm, v(-32.35, 40) * mm, v(-30.18, 41.24) * mm, v(-26.03, 43.22) * mm]});
            skFitSpline(sketch, "E992", {"points": [v(-26.03, 43.22) * mm, v(-21.63, 45.32) * mm, v(-18.51, 46.38) * mm, v(-15.2, 46.91) * mm]});
            skFitSpline(sketch, "E993", {"points": [v(-15.2, 46.91) * mm, v(-11.48, 47.5) * mm, v(-11.27, 47.35) * mm, v(-10.94, 43.78) * mm]});
            skFitSpline(sketch, "E994", {"points": [v(-10.94, 43.78) * mm, v(-10.87, 43.01) * mm, v(-10.73, 42.38) * mm, v(-10.58, 42.24) * mm]});
            skFitSpline(sketch, "E995", {"points": [v(-10.58, 42.24) * mm, v(-10.38, 42.03) * mm, v(-8.82, 42) * mm, v(-0.1, 42) * mm]});
            skFitSpline(sketch, "E996", {"points": [v(-0.1, 42) * mm, v(6.17, 42) * mm, v(10.27, 42.06) * mm, v(10.46, 42.16) * mm]});
            skFitSpline(sketch, "E997", {"points": [v(10.46, 42.16) * mm, v(10.7, 42.28) * mm, v(10.78, 42.62) * mm, v(10.88, 43.7) * mm]});
            skFitSpline(sketch, "E998", {"points": [v(10.88, 43.7) * mm, v(11.2, 47.4) * mm, v(11.4, 47.54) * mm, v(15.5, 46.84) * mm]});
            skFitSpline(sketch, "E999", {"points": [v(15.5, 46.84) * mm, v(19.11, 46.2) * mm, v(21.58, 45.33) * mm, v(26.72, 42.84) * mm]});
            skFitSpline(sketch, "E1000", {"points": [v(26.72, 42.84) * mm, v(31.06, 40.74) * mm, v(32.37, 39.97) * mm, v(32.61, 39.38) * mm]});
            skFitSpline(sketch, "E1001", {"points": [v(32.61, 39.38) * mm, v(32.75, 39.04) * mm, v(32.8, 34.14) * mm, v(32.8, 21.33) * mm]});
            skLineSegment(sketch, "E1002", {"start": v(-33.84, -0.16) * mm, "end": v(-32.9, 3.58) * mm});
            skLineSegment(sketch, "E1003", {"start": v(-32.9, 3.58) * mm, "end": v(-32.88, 21.3) * mm});
            skFitSpline(sketch, "E1004", {"points": [v(33.77, -0.07) * mm, v(34.3, -2.17) * mm, v(34.82, -3.92) * mm, v(34.93, -3.96) * mm]});
            skFitSpline(sketch, "E1005", {"points": [v(34.93, -3.96) * mm, v(35.38, -4.11) * mm, v(36.54, -0.48) * mm, v(37.2, 3.17) * mm]});
            skFitSpline(sketch, "E1006", {"points": [v(37.2, 3.17) * mm, v(38.91, 12.72) * mm, v(38.2, 19.32) * mm, v(35.1, 22.5) * mm]});
            skFitSpline(sketch, "E1007", {"points": [v(35.1, 22.5) * mm, v(34.67, 22.96) * mm, v(34.27, 23.5) * mm, v(34.22, 23.7) * mm]});
            skFitSpline(sketch, "E1008", {"points": [v(34.22, 23.7) * mm, v(34.18, 23.91) * mm, v(34.02, 28.68) * mm, v(33.88, 34.3) * mm]});
            skFitSpline(sketch, "E1009", {"points": [v(33.88, 34.3) * mm, v(33.58, 45.72) * mm, v(33.57, 45.8) * mm, v(32.33, 48.27) * mm]});
            skFitSpline(sketch, "E1010", {"points": [v(32.33, 48.27) * mm, v(28.71, 55.45) * mm, v(19.29, 60.48) * mm, v(6.38, 62.1) * mm]});
            skFitSpline(sketch, "E1011", {"points": [v(6.38, 62.1) * mm, v(2.94, 62.54) * mm, v(-3.55, 62.5) * mm, v(-7.07, 62.02) * mm]});
            skFitSpline(sketch, "E1012", {"points": [v(-7.07, 62.02) * mm, v(-13.13, 61.2) * mm, v(-18, 59.77) * mm, v(-22.32, 57.55) * mm]});
            skFitSpline(sketch, "E1013", {"points": [v(-22.32, 57.55) * mm, v(-27.48, 54.9) * mm, v(-30.78, 51.75) * mm, v(-32.64, 47.73) * mm]});
            skFitSpline(sketch, "E1014", {"points": [v(-32.64, 47.73) * mm, v(-33.63, 45.59) * mm, v(-33.66, 45.3) * mm, v(-33.94, 34.25) * mm]});
            skFitSpline(sketch, "E1015", {"points": [v(-33.94, 34.25) * mm, v(-34.09, 28.66) * mm, v(-34.24, 23.9) * mm, v(-34.3, 23.67) * mm]});
            skFitSpline(sketch, "E1016", {"points": [v(-34.3, 23.67) * mm, v(-34.35, 23.45) * mm, v(-34.74, 22.92) * mm, v(-35.17, 22.5) * mm]});
            skFitSpline(sketch, "E1017", {"points": [v(-35.17, 22.5) * mm, v(-37.56, 20.14) * mm, v(-38.6, 15.2) * mm, v(-38.03, 8.92) * mm]});
            skFitSpline(sketch, "E1018", {"points": [v(-38.03, 8.92) * mm, v(-37.57, 3.87) * mm, v(-36.64, -0.58) * mm, v(-35.45, -3.39) * mm]});
            skFitSpline(sketch, "E1019", {"points": [v(-35.45, -3.39) * mm, v(-35.3, -3.74) * mm, v(-35.1, -4) * mm, v(-34.99, -3.96) * mm]});
            skFitSpline(sketch, "E1020", {"points": [v(-34.99, -3.96) * mm, v(-34.88, -3.92) * mm, v(-34.37, -2.21) * mm, v(-33.84, -0.16) * mm]});
            skLineSegment(sketch, "E1021", {"start": v(32.8, 21.33) * mm, "end": v(32.8, 3.75) * mm});
            skLineSegment(sketch, "E1022", {"start": v(32.8, 3.75) * mm, "end": v(33.77, -0.07) * mm});
            skFitSpline(sketch, "E1023", {"points": [v(3.92, 14.55) * mm, v(5.96, 14.86) * mm, v(7.67, 15.14) * mm, v(7.72, 15.2) * mm]});
            skFitSpline(sketch, "E1024", {"points": [v(7.72, 15.2) * mm, v(7.82, 15.3) * mm, v(10.3, 38.08) * mm, v(10.3, 38.93) * mm]});
            skFitSpline(sketch, "E1025", {"points": [v(-10.37, 38.96) * mm, v(-10.36, 37.68) * mm, v(-7.86, 15.42) * mm, v(-7.7, 15.26) * mm]});
            skFitSpline(sketch, "E1026", {"points": [v(-7.7, 15.26) * mm, v(-7.54, 15.1) * mm, v(-1.22, 14.05) * mm, v(-0.2, 14.02) * mm]});
            skFitSpline(sketch, "E1027", {"points": [v(-0.2, 14.02) * mm, v(0.03, 14.01) * mm, v(1.88, 14.25) * mm, v(3.92, 14.55) * mm]});
            skLineSegment(sketch, "E1028", {"start": v(10.3, 38.93) * mm, "end": v(10.3, 39.5) * mm});
            skLineSegment(sketch, "E1029", {"start": v(10.3, 39.5) * mm, "end": v(-0.03, 39.5) * mm});
            skLineSegment(sketch, "E1030", {"start": v(-0.03, 39.5) * mm, "end": v(-10.37, 39.5) * mm});
            skLineSegment(sketch, "E1031", {"start": v(-10.37, 39.5) * mm, "end": v(-10.37, 38.96) * mm});
            skFitSpline(sketch, "E1032", {"points": [v(-10.78, -64.89) * mm, v(-12.24, -64.69) * mm, v(-14.83, -64.11) * mm, v(-15.66, -63.8) * mm]});
            skFitSpline(sketch, "E1033", {"points": [v(-15.66, -63.8) * mm, v(-16.4, -63.52) * mm, v(-16.9, -63.15) * mm, v(-17.96, -62.1) * mm]});
            skFitSpline(sketch, "E1034", {"points": [v(-17.96, -62.1) * mm, v(-19.54, -60.51) * mm, v(-19.61, -60.4) * mm, v(-26.94, -48.87) * mm]});
            skFitSpline(sketch, "E1035", {"points": [v(-33.13, -32.2) * mm, v(-33.87, -21.88) * mm, v(-34.15, -18.55) * mm, v(-34.46, -16.75) * mm]});
            skFitSpline(sketch, "E1036", {"points": [v(-34.46, -16.75) * mm, v(-34.8, -14.8) * mm, v(-35.56, -11.8) * mm, v(-36.2, -9.92) * mm]});
            skFitSpline(sketch, "E1037", {"points": [v(-36.2, -9.92) * mm, v(-36.57, -8.81) * mm, v(-36.7, -8.15) * mm, v(-36.67, -7.42) * mm]});
            skFitSpline(sketch, "E1038", {"points": [v(-36.67, -7.42) * mm, v(-36.65, -6.65) * mm, v(-36.73, -6.28) * mm, v(-37, -5.83) * mm]});
            skFitSpline(sketch, "E1039", {"points": [v(-37, -5.83) * mm, v(-38.34, -3.6) * mm, v(-39.52, 0.76) * mm, v(-40.18, 6) * mm]});
            skFitSpline(sketch, "E1040", {"points": [v(-40.18, 6) * mm, v(-41.25, 14.38) * mm, v(-40.43, 19.8) * mm, v(-37.54, 23.56) * mm]});
            skLineSegment(sketch, "E1041", {"start": v(-26.94, -48.87) * mm, "end": v(-32.57, -39.99) * mm});
            skLineSegment(sketch, "E1042", {"start": v(-32.57, -39.99) * mm, "end": v(-33.13, -32.2) * mm});
            skFitSpline(sketch, "E1043", {"points": [v(-36.43, 34.06) * mm, v(-36.3, 39.2) * mm, v(-36.13, 44.02) * mm, v(-36.03, 44.76) * mm]});
            skFitSpline(sketch, "E1044", {"points": [v(-36.03, 44.76) * mm, v(-35.58, 48.35) * mm, v(-33.7, 51.67) * mm, v(-30.32, 54.93) * mm]});
            skFitSpline(sketch, "E1045", {"points": [v(-30.32, 54.93) * mm, v(-25.67, 59.41) * mm, v(-18.17, 62.75) * mm, v(-9.68, 64.14) * mm]});
            skFitSpline(sketch, "E1046", {"points": [v(-9.68, 64.14) * mm, v(-5.46, 64.82) * mm, v(-4.46, 64.9) * mm, v(-0.03, 64.9) * mm]});
            skFitSpline(sketch, "E1047", {"points": [v(-0.03, 64.9) * mm, v(4.4, 64.9) * mm, v(5.37, 64.83) * mm, v(9.63, 64.14) * mm]});
            skFitSpline(sketch, "E1048", {"points": [v(9.63, 64.14) * mm, v(24.12, 61.8) * mm, v(34.78, 53.96) * mm, v(35.97, 44.76) * mm]});
            skFitSpline(sketch, "E1049", {"points": [v(35.97, 44.76) * mm, v(36.07, 44.02) * mm, v(36.25, 39.2) * mm, v(36.38, 34.06) * mm]});
            skLineSegment(sketch, "E1050", {"start": v(-37.54, 23.56) * mm, "end": v(-36.66, 24.7) * mm});
            skLineSegment(sketch, "E1051", {"start": v(-36.66, 24.7) * mm, "end": v(-36.43, 34.06) * mm});
            skFitSpline(sketch, "E1052", {"points": [v(37.48, 23.56) * mm, v(40.38, 19.73) * mm, v(41.2, 14.37) * mm, v(40.12, 6) * mm]});
            skFitSpline(sketch, "E1053", {"points": [v(40.12, 6) * mm, v(39.49, 1.04) * mm, v(38.46, -2.93) * mm, v(37.17, -5.39) * mm]});
            skFitSpline(sketch, "E1054", {"points": [v(37.17, -5.39) * mm, v(36.67, -6.34) * mm, v(36.58, -6.68) * mm, v(36.61, -7.43) * mm]});
            skFitSpline(sketch, "E1055", {"points": [v(36.61, -7.43) * mm, v(36.64, -8.08) * mm, v(36.49, -8.83) * mm, v(36.07, -10.12) * mm]});
            skFitSpline(sketch, "E1056", {"points": [v(36.07, -10.12) * mm, v(34.38, -15.37) * mm, v(34.15, -17.05) * mm, v(33.14, -31.5) * mm]});
            skFitSpline(sketch, "E1057", {"points": [v(33.14, -31.5) * mm, v(32.86, -35.49) * mm, v(32.57, -39.09) * mm, v(32.5, -39.5) * mm]});
            skFitSpline(sketch, "E1058", {"points": [v(32.5, -39.5) * mm, v(32.4, -40.07) * mm, v(30.93, -42.5) * mm, v(26.22, -49.91) * mm]});
            skFitSpline(sketch, "E1059", {"points": [v(26.22, -49.91) * mm, v(22.84, -55.23) * mm, v(19.76, -60) * mm, v(19.38, -60.5) * mm]});
            skFitSpline(sketch, "E1060", {"points": [v(19.38, -60.5) * mm, v(18.99, -61.01) * mm, v(18.18, -61.88) * mm, v(17.58, -62.45) * mm]});
            skFitSpline(sketch, "E1061", {"points": [v(17.58, -62.45) * mm, v(16.34, -63.6) * mm, v(15.56, -63.95) * mm, v(12.94, -64.53) * mm]});
            skFitSpline(sketch, "E1062", {"points": [v(12.94, -64.53) * mm, v(11.26, -64.9) * mm, v(10.96, -64.9) * mm, v(0.47, -64.93) * mm]});
            skFitSpline(sketch, "E1063", {"points": [v(0.47, -64.93) * mm, v(-5.45, -64.94) * mm, v(-10.5, -64.92) * mm, v(-10.78, -64.89) * mm]});
            skLineSegment(sketch, "E1064", {"start": v(36.38, 34.06) * mm, "end": v(36.6, 24.71) * mm});
            skLineSegment(sketch, "E1065", {"start": v(36.6, 24.71) * mm, "end": v(37.48, 23.56) * mm});
            skFitSpline(sketch, "E1066", {"points": [v(9.93, -62.5) * mm, v(11.87, -62.28) * mm, v(14.02, -61.88) * mm, v(14.74, -61.58) * mm]});
            skFitSpline(sketch, "E1067", {"points": [v(14.74, -61.58) * mm, v(15.43, -61.3) * mm, v(16.5, -60.32) * mm, v(17.38, -59.17) * mm]});
            skFitSpline(sketch, "E1068", {"points": [v(17.38, -59.17) * mm, v(18.75, -57.38) * mm, v(30.01, -39.44) * mm, v(30.14, -38.84) * mm]});
            skFitSpline(sketch, "E1069", {"points": [v(30.14, -38.84) * mm, v(30.2, -38.52) * mm, v(30.35, -36.94) * mm, v(30.46, -35.33) * mm]});
            skFitSpline(sketch, "E1070", {"points": [v(30.46, -35.33) * mm, v(30.57, -33.73) * mm, v(30.84, -30) * mm, v(31.06, -27.04) * mm]});
            skFitSpline(sketch, "E1071", {"points": [v(31.06, -27.04) * mm, v(31.52, -20.97) * mm, v(31.52, -20.83) * mm, v(31.31, -20.83) * mm]});
            skFitSpline(sketch, "E1072", {"points": [v(31.31, -20.83) * mm, v(31.23, -20.83) * mm, v(30.83, -21.41) * mm, v(30.42, -22.12) * mm]});
            skFitSpline(sketch, "E1073", {"points": [v(30.42, -22.12) * mm, v(30, -22.83) * mm, v(29.05, -24.28) * mm, v(28.29, -25.33) * mm]});
            skFitSpline(sketch, "E1074", {"points": [v(28.29, -25.33) * mm, v(26.09, -28.38) * mm, v(25.18, -29.72) * mm, v(24.22, -31.34) * mm]});
            skFitSpline(sketch, "E1075", {"points": [v(24.22, -31.34) * mm, v(23.17, -33.12) * mm, v(21.45, -36.97) * mm, v(20.54, -39.6) * mm]});
            skFitSpline(sketch, "E1076", {"points": [v(20.35, -43.93) * mm, v(20.6, -45.3) * mm, v(20.8, -46.66) * mm, v(20.8, -46.95) * mm]});
            skFitSpline(sketch, "E1077", {"points": [v(20.8, -46.95) * mm, v(20.8, -47.93) * mm, v(18.3, -53.3) * mm, v(17.06, -55.01) * mm]});
            skFitSpline(sketch, "E1078", {"points": [v(17.06, -55.01) * mm, v(16.75, -55.43) * mm, v(16.24, -55.9) * mm, v(15.92, -56.05) * mm]});
            skFitSpline(sketch, "E1079", {"points": [v(15.92, -56.05) * mm, v(15.04, -56.47) * mm, v(13.43, -56.4) * mm, v(11.7, -55.89) * mm]});
            skFitSpline(sketch, "E1080", {"points": [v(11.7, -55.89) * mm, v(9.38, -55.2) * mm, v(9.5, -55.15) * mm, v(8.87, -56.98) * mm]});
            skFitSpline(sketch, "E1081", {"points": [v(8.87, -56.98) * mm, v(8.58, -57.85) * mm, v(8.2, -58.65) * mm, v(8.04, -58.78) * mm]});
            skFitSpline(sketch, "E1082", {"points": [v(8.04, -58.78) * mm, v(7.8, -58.95) * mm, v(6.16, -59) * mm, v(-0.06, -59) * mm]});
            skFitSpline(sketch, "E1083", {"points": [v(-0.06, -59) * mm, v(-9.14, -59) * mm, v(-8.26, -59.2) * mm, v(-8.95, -56.91) * mm]});
            skFitSpline(sketch, "E1084", {"points": [v(-8.95, -56.91) * mm, v(-9.2, -56.12) * mm, v(-9.5, -55.44) * mm, v(-9.62, -55.39) * mm]});
            skFitSpline(sketch, "E1085", {"points": [v(-9.62, -55.39) * mm, v(-9.75, -55.34) * mm, v(-10.48, -55.51) * mm, v(-11.23, -55.77) * mm]});
            skFitSpline(sketch, "E1086", {"points": [v(-11.23, -55.77) * mm, v(-12.37, -56.16) * mm, v(-12.9, -56.24) * mm, v(-14.21, -56.25) * mm]});
            skFitSpline(sketch, "E1087", {"points": [v(-14.21, -56.25) * mm, v(-15.68, -56.25) * mm, v(-15.85, -56.21) * mm, v(-16.38, -55.81) * mm]});
            skFitSpline(sketch, "E1088", {"points": [v(-16.38, -55.81) * mm, v(-16.7, -55.57) * mm, v(-17.32, -54.74) * mm, v(-17.78, -53.98) * mm]});
            skFitSpline(sketch, "E1089", {"points": [v(-17.78, -53.98) * mm, v(-18.92, -52.05) * mm, v(-20.86, -47.64) * mm, v(-20.86, -46.97) * mm]});
            skFitSpline(sketch, "E1090", {"points": [v(-20.86, -46.97) * mm, v(-20.86, -46.67) * mm, v(-20.66, -45.32) * mm, v(-20.42, -43.96) * mm]});
            skFitSpline(sketch, "E1091", {"points": [v(-20.42, -43.96) * mm, v(-19.98, -41.51) * mm, v(-19.98, -41.48) * mm, v(-20.27, -40.54) * mm]});
            skFitSpline(sketch, "E1092", {"points": [v(-20.27, -40.54) * mm, v(-21.33, -37.12) * mm, v(-23.82, -31.78) * mm, v(-25.3, -29.73) * mm]});
            skFitSpline(sketch, "E1093", {"points": [v(-25.3, -29.73) * mm, v(-27.07, -27.3) * mm, v(-29.8, -23.26) * mm, v(-30.5, -22.04) * mm]});
            skFitSpline(sketch, "E1094", {"points": [v(-30.5, -22.04) * mm, v(-31.2, -20.85) * mm, v(-31.53, -20.55) * mm, v(-31.53, -21.12) * mm]});
            skFitSpline(sketch, "E1095", {"points": [v(-31.53, -21.12) * mm, v(-31.53, -22.26) * mm, v(-30.2, -39.2) * mm, v(-30.1, -39.37) * mm]});
            skFitSpline(sketch, "E1096", {"points": [v(-30.1, -39.37) * mm, v(-29.71, -40.02) * mm, v(-18.88, -57.08) * mm, v(-18.32, -57.91) * mm]});
            skFitSpline(sketch, "E1097", {"points": [v(-18.32, -57.91) * mm, v(-17.38, -59.32) * mm, v(-16.25, -60.63) * mm, v(-15.5, -61.17) * mm]});
            skFitSpline(sketch, "E1098", {"points": [v(-15.5, -61.17) * mm, v(-14.75, -61.7) * mm, v(-13.26, -62.1) * mm, v(-10.7, -62.41) * mm]});
            skFitSpline(sketch, "E1099", {"points": [v(-10.7, -62.41) * mm, v(-8.5, -62.68) * mm, v(7.55, -62.75) * mm, v(9.93, -62.5) * mm]});
            skLineSegment(sketch, "E1100", {"start": v(20.54, -39.6) * mm, "end": v(19.9, -41.44) * mm});
            skLineSegment(sketch, "E1101", {"start": v(19.9, -41.44) * mm, "end": v(20.35, -43.93) * mm});
            skFitSpline(sketch, "E1102", {"points": [v(6.6, -56.12) * mm, v(6.72, -55.86) * mm, v(6.84, -55.45) * mm, v(6.85, -55.2) * mm]});
            skFitSpline(sketch, "E1103", {"points": [v(0.06, -54.7) * mm, v(-3.93, -54.68) * mm, v(-6.83, -54.72) * mm, v(-6.92, -54.81) * mm]});
            skFitSpline(sketch, "E1104", {"points": [v(-6.92, -54.81) * mm, v(-7.08, -54.97) * mm, v(-6.8, -56.08) * mm, v(-6.49, -56.46) * mm]});
            skFitSpline(sketch, "E1105", {"points": [v(-6.49, -56.46) * mm, v(-6.36, -56.62) * mm, v(-4.93, -56.66) * mm, v(0.03, -56.62) * mm]});
            skLineSegment(sketch, "E1106", {"start": v(6.85, -55.2) * mm, "end": v(6.88, -54.75) * mm});
            skLineSegment(sketch, "E1107", {"start": v(6.88, -54.75) * mm, "end": v(0.06, -54.7) * mm});
            skFitSpline(sketch, "E1108", {"points": [v(-12.7, -53.68) * mm, v(-10.85, -53.15) * mm, v(-10.2, -52.83) * mm, v(-10.2, -52.46) * mm]});
            skFitSpline(sketch, "E1109", {"points": [v(-10.2, -52.46) * mm, v(-10.2, -51.99) * mm, v(-11.35, -47.78) * mm, v(-11.53, -47.6) * mm]});
            skFitSpline(sketch, "E1110", {"points": [v(-11.53, -47.6) * mm, v(-11.62, -47.5) * mm, v(-12.16, -47.9) * mm, v(-12.86, -48.55) * mm]});
            skFitSpline(sketch, "E1111", {"points": [v(-12.86, -48.55) * mm, v(-14.68, -50.27) * mm, v(-15, -50.15) * mm, v(-16.8, -47.04) * mm]});
            skFitSpline(sketch, "E1112", {"points": [v(-16.8, -47.04) * mm, v(-17.34, -46.1) * mm, v(-17.87, -45.34) * mm, v(-17.99, -45.33) * mm]});
            skFitSpline(sketch, "E1113", {"points": [v(-17.99, -45.33) * mm, v(-18.1, -45.33) * mm, v(-18.24, -45.54) * mm, v(-18.3, -45.79) * mm]});
            skFitSpline(sketch, "E1114", {"points": [v(-18.3, -45.79) * mm, v(-18.35, -46.04) * mm, v(-18.43, -46.37) * mm, v(-18.47, -46.52) * mm]});
            skFitSpline(sketch, "E1115", {"points": [v(-18.47, -46.52) * mm, v(-18.6, -47.04) * mm, v(-16.24, -52.14) * mm, v(-15.25, -53.46) * mm]});
            skFitSpline(sketch, "E1116", {"points": [v(-15.25, -53.46) * mm, v(-14.77, -54.1) * mm, v(-14.3, -54.15) * mm, v(-12.7, -53.68) * mm]});
            skLineSegment(sketch, "E1117", {"start": v(0.03, -56.62) * mm, "end": v(6.38, -56.58) * mm});
            skLineSegment(sketch, "E1118", {"start": v(6.38, -56.58) * mm, "end": v(6.6, -56.12) * mm});
            skFitSpline(sketch, "E1119", {"points": [v(15.09, -53.62) * mm, v(15.55, -53.11) * mm, v(16.77, -50.79) * mm, v(17.7, -48.65) * mm]});
            skFitSpline(sketch, "E1120", {"points": [v(17.7, -48.65) * mm, v(18.37, -47.09) * mm, v(18.44, -46.8) * mm, v(18.33, -46.15) * mm]});
            skFitSpline(sketch, "E1121", {"points": [v(18.33, -46.15) * mm, v(18.13, -44.98) * mm, v(17.82, -45.14) * mm, v(16.8, -46.94) * mm]});
            skFitSpline(sketch, "E1122", {"points": [v(16.8, -46.94) * mm, v(14.99, -50.13) * mm, v(14.62, -50.28) * mm, v(12.8, -48.55) * mm]});
            skFitSpline(sketch, "E1123", {"points": [v(12.8, -48.55) * mm, v(12.12, -47.91) * mm, v(11.56, -47.5) * mm, v(11.48, -47.6) * mm]});
            skFitSpline(sketch, "E1124", {"points": [v(11.48, -47.6) * mm, v(11.3, -47.79) * mm, v(10.13, -52) * mm, v(10.13, -52.46) * mm]});
            skFitSpline(sketch, "E1125", {"points": [v(10.13, -52.46) * mm, v(10.13, -52.84) * mm, v(10.17, -52.86) * mm, v(12.13, -53.51) * mm]});
            skFitSpline(sketch, "E1126", {"points": [v(12.13, -53.51) * mm, v(13.9, -54.1) * mm, v(14.62, -54.13) * mm, v(15.09, -53.62) * mm]});
            skFitSpline(sketch, "E1127", {"points": [v(8.4, -49.41) * mm, v(8.8, -47.95) * mm, v(9.13, -46.62) * mm, v(9.13, -46.46) * mm]});
            skFitSpline(sketch, "E1128", {"points": [v(9.13, -46.46) * mm, v(9.13, -46.18) * mm, v(8.59, -46.16) * mm, v(-0.03, -46.16) * mm]});
            skFitSpline(sketch, "E1129", {"points": [v(-0.03, -46.16) * mm, v(-8, -46.16) * mm, v(-9.2, -46.2) * mm, v(-9.2, -46.4) * mm]});
            skFitSpline(sketch, "E1130", {"points": [v(-9.2, -46.4) * mm, v(-9.2, -46.65) * mm, v(-8.2, -50.52) * mm, v(-7.84, -51.62) * mm]});
            skLineSegment(sketch, "E1131", {"start": v(-7.84, -51.62) * mm, "end": v(-7.67, -52.17) * mm});
            skLineSegment(sketch, "E1132", {"start": v(-7.67, -52.17) * mm, "end": v(0, -52.12) * mm});
            skLineSegment(sketch, "E1133", {"start": v(0, -52.12) * mm, "end": v(7.69, -52.08) * mm});
            skLineSegment(sketch, "E1134", {"start": v(7.69, -52.08) * mm, "end": v(8.4, -49.41) * mm});
            skFitSpline(sketch, "E1135", {"points": [v(-13.03, -43.53) * mm, v(-13.35, -42.92) * mm, v(-14.04, -41.85) * mm, v(-14.56, -41.16) * mm]});
            skFitSpline(sketch, "E1136", {"points": [v(-14.56, -41.16) * mm, v(-15.58, -39.82) * mm, v(-18.8, -36.54) * mm, v(-18.95, -36.69) * mm]});
            skFitSpline(sketch, "E1137", {"points": [v(-18.95, -36.69) * mm, v(-19.16, -36.9) * mm, v(-17.45, -41.2) * mm, v(-16.5, -42.83) * mm]});
            skFitSpline(sketch, "E1138", {"points": [v(-16.5, -42.83) * mm, v(-15.08, -45.26) * mm, v(-14.4, -46.33) * mm, v(-14.24, -46.33) * mm]});
            skFitSpline(sketch, "E1139", {"points": [v(-14.24, -46.33) * mm, v(-14.16, -46.33) * mm, v(-13.73, -45.95) * mm, v(-13.28, -45.5) * mm]});
            skLineSegment(sketch, "E1140", {"start": v(-13.28, -45.5) * mm, "end": v(-12.45, -44.65) * mm});
            skLineSegment(sketch, "E1141", {"start": v(-12.45, -44.65) * mm, "end": v(-13.03, -43.53) * mm});
            skFitSpline(sketch, "E1142", {"points": [v(14.5, -46.04) * mm, v(14.63, -45.88) * mm, v(15.37, -44.67) * mm, v(16.13, -43.35) * mm]});
            skFitSpline(sketch, "E1143", {"points": [v(16.13, -43.35) * mm, v(17.7, -40.65) * mm, v(19.34, -36.5) * mm, v(18.84, -36.5) * mm]});
            skFitSpline(sketch, "E1144", {"points": [v(18.84, -36.5) * mm, v(18.67, -36.5) * mm, v(15.6, -39.75) * mm, v(14.58, -41.02) * mm]});
            skFitSpline(sketch, "E1145", {"points": [v(14.58, -41.02) * mm, v(13.96, -41.8) * mm, v(12.47, -44.28) * mm, v(12.47, -44.54) * mm]});
            skFitSpline(sketch, "E1146", {"points": [v(12.47, -44.54) * mm, v(12.47, -44.71) * mm, v(13.97, -46.33) * mm, v(14.13, -46.33) * mm]});
            skFitSpline(sketch, "E1147", {"points": [v(14.13, -46.33) * mm, v(14.2, -46.33) * mm, v(14.36, -46.2) * mm, v(14.5, -46.04) * mm]});
            skFitSpline(sketch, "E1148", {"points": [v(11.04, -42.12) * mm, v(12.34, -39.88) * mm, v(13.14, -38.9) * mm, v(17.23, -34.58) * mm]});
            skFitSpline(sketch, "E1149", {"points": [v(17.23, -34.58) * mm, v(21.73, -29.83) * mm, v(23.1, -28.3) * mm, v(24.74, -26.11) * mm]});
            skFitSpline(sketch, "E1150", {"points": [v(24.74, -26.11) * mm, v(26.93, -23.2) * mm, v(27.39, -21.87) * mm, v(27.64, -17.67) * mm]});
            skFitSpline(sketch, "E1151", {"points": [v(27.64, -17.67) * mm, v(27.73, -16.15) * mm, v(27.88, -13.98) * mm, v(27.97, -12.83) * mm]});
            skFitSpline(sketch, "E1152", {"points": [v(27.97, -12.83) * mm, v(28.25, -9.24) * mm, v(28.19, -8.82) * mm, v(27.47, -9.82) * mm]});
            skFitSpline(sketch, "E1153", {"points": [v(27.47, -9.82) * mm, v(26.52, -11.16) * mm, v(23.38, -13.1) * mm, v(20.72, -13.98) * mm]});
            skFitSpline(sketch, "E1154", {"points": [v(20.72, -13.98) * mm, v(19.11, -14.51) * mm, v(13.07, -15.78) * mm, v(11.33, -15.95) * mm]});
            skFitSpline(sketch, "E1155", {"points": [v(11.33, -15.95) * mm, v(10.3, -16.05) * mm, v(10.27, -16.04) * mm, v(9.7, -15.48) * mm]});
            skFitSpline(sketch, "E1156", {"points": [v(9.7, -15.48) * mm, v(8.92, -14.75) * mm, v(7.74, -13.09) * mm, v(7.4, -12.27) * mm]});
            skFitSpline(sketch, "E1157", {"points": [v(7.4, -12.27) * mm, v(7.16, -11.7) * mm, v(7.09, -11.64) * mm, v(6.68, -11.73) * mm]});
            skFitSpline(sketch, "E1158", {"points": [v(6.68, -11.73) * mm, v(2.73, -12.6) * mm, v(-2.8, -12.6) * mm, v(-6.74, -11.73) * mm]});
            skFitSpline(sketch, "E1159", {"points": [v(-6.74, -11.73) * mm, v(-7.15, -11.64) * mm, v(-7.23, -11.7) * mm, v(-7.47, -12.27) * mm]});
            skFitSpline(sketch, "E1160", {"points": [v(-7.47, -12.27) * mm, v(-7.8, -13.09) * mm, v(-8.99, -14.75) * mm, v(-9.76, -15.48) * mm]});
            skFitSpline(sketch, "E1161", {"points": [v(-9.76, -15.48) * mm, v(-10.33, -16.04) * mm, v(-10.38, -16.05) * mm, v(-11.4, -15.95) * mm]});
            skFitSpline(sketch, "E1162", {"points": [v(-11.4, -15.95) * mm, v(-13.13, -15.78) * mm, v(-19.18, -14.51) * mm, v(-20.78, -13.98) * mm]});
            skFitSpline(sketch, "E1163", {"points": [v(-20.78, -13.98) * mm, v(-23.45, -13.1) * mm, v(-26.39, -11.3) * mm, v(-27.45, -9.9) * mm]});
            skFitSpline(sketch, "E1164", {"points": [v(-27.45, -9.9) * mm, v(-27.69, -9.59) * mm, v(-27.95, -9.33) * mm, v(-28.04, -9.33) * mm]});
            skFitSpline(sketch, "E1165", {"points": [v(-28.04, -9.33) * mm, v(-28.24, -9.33) * mm, v(-28.24, -10.4) * mm, v(-28.03, -12.73) * mm]});
            skFitSpline(sketch, "E1166", {"points": [v(-28.03, -12.73) * mm, v(-27.94, -13.75) * mm, v(-27.8, -15.86) * mm, v(-27.7, -17.42) * mm]});
            skFitSpline(sketch, "E1167", {"points": [v(-27.7, -17.42) * mm, v(-27.44, -21.9) * mm, v(-27.08, -22.94) * mm, v(-24.5, -26.61) * mm]});
            skFitSpline(sketch, "E1168", {"points": [v(-24.5, -26.61) * mm, v(-23.03, -28.7) * mm, v(-22.11, -29.74) * mm, v(-18.16, -33.8) * mm]});
            skFitSpline(sketch, "E1169", {"points": [v(-18.16, -33.8) * mm, v(-13.5, -38.58) * mm, v(-12.2, -40.09) * mm, v(-11.2, -41.91) * mm]});
            skFitSpline(sketch, "E1170", {"points": [v(-11.2, -41.91) * mm, v(-10.9, -42.46) * mm, v(-10.55, -43.08) * mm, v(-10.42, -43.3) * mm]});
            skFitSpline(sketch, "E1171", {"points": [v(-30.27, -14.72) * mm, v(-30.33, -13.65) * mm, v(-30.46, -12.16) * mm, v(-30.55, -11.43) * mm]});
            skFitSpline(sketch, "E1172", {"points": [v(-30.55, -11.43) * mm, v(-30.9, -8.7) * mm, v(-30.06, -3.15) * mm, v(-28.54, 2) * mm]});
            skFitSpline(sketch, "E1173", {"points": [v(-28.54, 2) * mm, v(-28.3, 2.77) * mm, v(-28.3, 16.63) * mm, v(-28.54, 19.16) * mm]});
            skFitSpline(sketch, "E1174", {"points": [v(-28.54, 19.16) * mm, v(-28.9, 23.06) * mm, v(-29.9, 28.76) * mm, v(-30.21, 28.57) * mm]});
            skFitSpline(sketch, "E1175", {"points": [v(-30.21, 28.57) * mm, v(-30.3, 28.52) * mm, v(-30.36, 23.42) * mm, v(-30.36, 16.07) * mm]});
            skLineSegment(sketch, "E1176", {"start": v(-10.42, -43.3) * mm, "end": v(-10.19, -43.67) * mm});
            skLineSegment(sketch, "E1177", {"start": v(-10.19, -43.67) * mm, "end": v(0, -43.62) * mm});
            skLineSegment(sketch, "E1178", {"start": v(0, -43.62) * mm, "end": v(10.19, -43.58) * mm});
            skLineSegment(sketch, "E1179", {"start": v(10.19, -43.58) * mm, "end": v(11.04, -42.12) * mm});
            skFitSpline(sketch, "E1180", {"points": [v(-33.01, -11.3) * mm, v(-31.76, -14.24) * mm, v(-30.56, -16.67) * mm, v(-30.35, -16.67) * mm]});
            skFitSpline(sketch, "E1181", {"points": [v(-30.35, -16.67) * mm, v(-30.2, -16.67) * mm, v(-30.18, -16.2) * mm, v(-30.27, -14.72) * mm]});
            skLineSegment(sketch, "E1182", {"start": v(-30.36, 16.07) * mm, "end": v(-30.36, 3.66) * mm});
            skLineSegment(sketch, "E1183", {"start": v(-30.36, 3.66) * mm, "end": v(-32.03, -3) * mm});
            skLineSegment(sketch, "E1184", {"start": v(-32.03, -3) * mm, "end": v(-33.7, -9.68) * mm});
            skLineSegment(sketch, "E1185", {"start": v(-33.7, -9.68) * mm, "end": v(-33.01, -11.3) * mm});
            skFitSpline(sketch, "E1186", {"points": [v(31, -15.66) * mm, v(31.24, -15.16) * mm, v(31.94, -13.6) * mm, v(32.56, -12.2) * mm]});
            skFitSpline(sketch, "E1187", {"points": [v(30.3, 16.06) * mm, v(30.3, 23.9) * mm, v(30.24, 28.5) * mm, v(30.14, 28.5) * mm]});
            skFitSpline(sketch, "E1188", {"points": [v(30.14, 28.5) * mm, v(29.85, 28.5) * mm, v(29.36, 26.13) * mm, v(28.77, 21.91) * mm]});
            skFitSpline(sketch, "E1189", {"points": [v(28.77, 21.91) * mm, v(28.46, 19.73) * mm, v(28.41, 18.38) * mm, v(28.34, 11.12) * mm]});
            skLineSegment(sketch, "E1190", {"start": v(32.56, -12.2) * mm, "end": v(33.68, -9.67) * mm});
            skLineSegment(sketch, "E1191", {"start": v(33.68, -9.67) * mm, "end": v(31.99, -3.03) * mm});
            skLineSegment(sketch, "E1192", {"start": v(31.99, -3.03) * mm, "end": v(30.3, 3.61) * mm});
            skLineSegment(sketch, "E1193", {"start": v(30.3, 3.61) * mm, "end": v(30.3, 16.06) * mm});
            skFitSpline(sketch, "E1194", {"points": [v(28.87, 0.61) * mm, v(30.2, -4.3) * mm, v(30.8, -8.8) * mm, v(30.49, -11.6) * mm]});
            skFitSpline(sketch, "E1195", {"points": [v(30.49, -11.6) * mm, v(30.39, -12.51) * mm, v(30.25, -14.03) * mm, v(30.2, -14.98) * mm]});
            skFitSpline(sketch, "E1196", {"points": [v(30.2, -14.98) * mm, v(30.06, -17) * mm, v(30.25, -17.17) * mm, v(31, -15.66) * mm]});
            skLineSegment(sketch, "E1197", {"start": v(28.34, 11.12) * mm, "end": v(28.27, 2.83) * mm});
            skLineSegment(sketch, "E1198", {"start": v(28.27, 2.83) * mm, "end": v(28.87, 0.61) * mm});
            skFitSpline(sketch, "E1199", {"points": [v(-10.4, -12.53) * mm, v(-9.46, -11.19) * mm, v(-9.38, -10.8) * mm, v(-9.98, -10.38) * mm]});
            skFitSpline(sketch, "E1200", {"points": [v(-9.98, -10.38) * mm, v(-10.6, -9.94) * mm, v(-16.4, -6.81) * mm, v(-19.12, -5.46) * mm]});
            skFitSpline(sketch, "E1201", {"points": [v(-19.12, -5.46) * mm, v(-23.74, -3.14) * mm, v(-26.4, -1.97) * mm, v(-26.6, -2.17) * mm]});
            skFitSpline(sketch, "E1202", {"points": [v(-26.6, -2.17) * mm, v(-26.71, -2.28) * mm, v(-26.78, -3.11) * mm, v(-26.78, -4.38) * mm]});
            skFitSpline(sketch, "E1203", {"points": [v(-26.78, -4.38) * mm, v(-26.78, -6.17) * mm, v(-26.73, -6.51) * mm, v(-26.4, -7.2) * mm]});
            skFitSpline(sketch, "E1204", {"points": [v(-26.4, -7.2) * mm, v(-25.6, -8.82) * mm, v(-22.94, -10.74) * mm, v(-20.2, -11.68) * mm]});
            skFitSpline(sketch, "E1205", {"points": [v(-20.2, -11.68) * mm, v(-19, -12.09) * mm, v(-12.4, -13.48) * mm, v(-11.6, -13.5) * mm]});
            skFitSpline(sketch, "E1206", {"points": [v(-11.6, -13.5) * mm, v(-11.15, -13.5) * mm, v(-10.99, -13.37) * mm, v(-10.4, -12.53) * mm]});
            skFitSpline(sketch, "E1207", {"points": [v(15.57, -12.76) * mm, v(20.9, -11.68) * mm, v(22.98, -10.8) * mm, v(25.08, -8.75) * mm]});
            skFitSpline(sketch, "E1208", {"points": [v(25.08, -8.75) * mm, v(26.53, -7.33) * mm, v(26.8, -6.6) * mm, v(26.8, -4.17) * mm]});
            skFitSpline(sketch, "E1209", {"points": [v(26.8, -4.17) * mm, v(26.8, -1.7) * mm, v(26.88, -1.73) * mm, v(23.79, -3.17) * mm]});
            skFitSpline(sketch, "E1210", {"points": [v(23.79, -3.17) * mm, v(19.07, -5.38) * mm, v(10.67, -9.76) * mm, v(9.75, -10.5) * mm]});
            skFitSpline(sketch, "E1211", {"points": [v(9.75, -11.55) * mm, v(10.25, -12.57) * mm, v(11.1, -13.5) * mm, v(11.53, -13.5) * mm]});
            skFitSpline(sketch, "E1212", {"points": [v(11.53, -13.5) * mm, v(11.72, -13.5) * mm, v(13.54, -13.16) * mm, v(15.57, -12.76) * mm]});
            skLineSegment(sketch, "E1213", {"start": v(9.75, -10.5) * mm, "end": v(9.39, -10.8) * mm});
            skLineSegment(sketch, "E1214", {"start": v(9.39, -10.8) * mm, "end": v(9.75, -11.55) * mm});
            skFitSpline(sketch, "E1215", {"points": [v(5.43, -9.52) * mm, v(6.78, -9.23) * mm, v(7.4, -8.96) * mm, v(10.1, -7.48) * mm]});
            skFitSpline(sketch, "E1216", {"points": [v(10.1, -7.48) * mm, v(14.6, -5.03) * mm, v(19.08, -2.74) * mm, v(22.8, -1) * mm]});
            skFitSpline(sketch, "E1217", {"points": [v(22.8, -1) * mm, v(24.59, -0.16) * mm, v(26.1, 0.58) * mm, v(26.18, 0.65) * mm]});
            skFitSpline(sketch, "E1218", {"points": [v(26.18, 0.65) * mm, v(26.26, 0.73) * mm, v(26.2, 1.27) * mm, v(26.04, 1.85) * mm]});
            skFitSpline(sketch, "E1219", {"points": [v(26.04, 1.85) * mm, v(25.8, 2.8) * mm, v(25.77, 3.75) * mm, v(25.85, 10.5) * mm]});
            skFitSpline(sketch, "E1220", {"points": [v(25.85, 10.5) * mm, v(25.94, 18.3) * mm, v(26.08, 20.3) * mm, v(26.82, 24.91) * mm]});
            skFitSpline(sketch, "E1221", {"points": [v(26.82, 24.91) * mm, v(27.3, 27.92) * mm, v(28.32, 32.46) * mm, v(29.21, 35.51) * mm]});
            skFitSpline(sketch, "E1222", {"points": [v(29.21, 35.51) * mm, v(29.63, 36.92) * mm, v(29.96, 38.18) * mm, v(29.96, 38.3) * mm]});
            skFitSpline(sketch, "E1223", {"points": [v(29.96, 38.3) * mm, v(29.97, 38.56) * mm, v(22.78, 42.1) * mm, v(20.59, 42.9) * mm]});
            skFitSpline(sketch, "E1224", {"points": [v(20.59, 42.9) * mm, v(18.84, 43.55) * mm, v(15.3, 44.45) * mm, v(14.22, 44.53) * mm]});
            skFitSpline(sketch, "E1225", {"points": [v(14.22, 44.53) * mm, v(13.58, 44.58) * mm, v(13.55, 44.56) * mm, v(13.42, 44) * mm]});
            skFitSpline(sketch, "E1226", {"points": [v(13.42, 44) * mm, v(13.35, 43.68) * mm, v(12.58, 36.78) * mm, v(11.7, 28.66) * mm]});
            skFitSpline(sketch, "E1227", {"points": [v(11.7, 28.66) * mm, v(10.84, 20.55) * mm, v(10.09, 13.78) * mm, v(10.03, 13.62) * mm]});
            skFitSpline(sketch, "E1228", {"points": [v(10.03, 13.62) * mm, v(9.98, 13.46) * mm, v(9.78, 13.22) * mm, v(9.58, 13.09) * mm]});
            skFitSpline(sketch, "E1229", {"points": [v(9.58, 13.09) * mm, v(9.38, 12.96) * mm, v(7.14, 12.55) * mm, v(4.6, 12.17) * mm]});
            skFitSpline(sketch, "E1230", {"points": [v(-4.65, 12.17) * mm, v(-7.2, 12.55) * mm, v(-9.4, 12.93) * mm, v(-9.56, 13.02) * mm]});
            skFitSpline(sketch, "E1231", {"points": [v(-9.56, 13.02) * mm, v(-9.73, 13.1) * mm, v(-9.93, 13.3) * mm, v(-10.01, 13.46) * mm]});
            skFitSpline(sketch, "E1232", {"points": [v(-10.01, 13.46) * mm, v(-10.1, 13.62) * mm, v(-10.89, 20.5) * mm, v(-11.77, 28.75) * mm]});
            skFitSpline(sketch, "E1233", {"points": [v(-11.77, 28.75) * mm, v(-12.65, 37) * mm, v(-13.43, 43.93) * mm, v(-13.5, 44.16) * mm]});
            skFitSpline(sketch, "E1234", {"points": [v(-13.5, 44.16) * mm, v(-13.62, 44.54) * mm, v(-13.7, 44.57) * mm, v(-14.37, 44.52) * mm]});
            skFitSpline(sketch, "E1235", {"points": [v(-14.37, 44.52) * mm, v(-15.54, 44.43) * mm, v(-19.3, 43.43) * mm, v(-21.03, 42.75) * mm]});
            skFitSpline(sketch, "E1236", {"points": [v(-21.03, 42.75) * mm, v(-23.05, 41.95) * mm, v(-29.15, 38.99) * mm, v(-29.68, 38.55) * mm]});
            skLineSegment(sketch, "E1237", {"start": v(4.6, 12.17) * mm, "end": v(-0.03, 11.49) * mm});
            skLineSegment(sketch, "E1238", {"start": v(-0.03, 11.49) * mm, "end": v(-4.65, 12.17) * mm});
            skFitSpline(sketch, "E1239", {"points": [v(-29.48, 36.23) * mm, v(-28.35, 32.5) * mm, v(-27.34, 28.05) * mm, v(-26.78, 24.33) * mm]});
            skFitSpline(sketch, "E1240", {"points": [v(-26.78, 24.33) * mm, v(-26.11, 19.97) * mm, v(-26.01, 18.4) * mm, v(-25.92, 10.67) * mm]});
            skFitSpline(sketch, "E1241", {"points": [v(-25.92, 10.67) * mm, v(-25.84, 3.77) * mm, v(-25.86, 2.8) * mm, v(-26.1, 1.85) * mm]});
            skFitSpline(sketch, "E1242", {"points": [v(-26.1, 1.85) * mm, v(-26.26, 1.27) * mm, v(-26.32, 0.73) * mm, v(-26.25, 0.66) * mm]});
            skFitSpline(sketch, "E1243", {"points": [v(-26.25, 0.66) * mm, v(-26.18, 0.58) * mm, v(-24.88, -0.05) * mm, v(-23.36, -0.76) * mm]});
            skFitSpline(sketch, "E1244", {"points": [v(-23.36, -0.76) * mm, v(-19.24, -2.68) * mm, v(-16.08, -4.29) * mm, v(-11.36, -6.85) * mm]});
            skFitSpline(sketch, "E1245", {"points": [v(-11.36, -6.85) * mm, v(-5.87, -9.82) * mm, v(-5.07, -10.03) * mm, v(0.63, -9.92) * mm]});
            skFitSpline(sketch, "E1246", {"points": [v(0.63, -9.92) * mm, v(3.07, -9.87) * mm, v(4.27, -9.77) * mm, v(5.43, -9.52) * mm]});
            skLineSegment(sketch, "E1247", {"start": v(-29.68, 38.55) * mm, "end": v(-30.08, 38.22) * mm});
            skLineSegment(sketch, "E1248", {"start": v(-30.08, 38.22) * mm, "end": v(-29.48, 36.23) * mm});
            skFitSpline(sketch, "E1249", {"points": [v(-32.03, 39.98) * mm, v(-31.26, 40.54) * mm, v(-26.57, 42.95) * mm, v(-24.07, 44.06) * mm]});
            skFitSpline(sketch, "E1250", {"points": [v(-24.07, 44.06) * mm, v(-20.65, 45.6) * mm, v(-17.11, 46.64) * mm, v(-14.06, 47) * mm]});
            skFitSpline(sketch, "E1251", {"points": [v(-14.06, 47) * mm, v(-12.4, 47.2) * mm, v(-11.68, 47.07) * mm, v(-11.44, 46.52) * mm]});
            skFitSpline(sketch, "E1252", {"points": [v(-11.44, 46.52) * mm, v(-11.37, 46.37) * mm, v(-11.2, 45.3) * mm, v(-11.05, 44.16) * mm]});
            skLineSegment(sketch, "E1253", {"start": v(-33.75, 0.01) * mm, "end": v(-32.71, 4.08) * mm});
            skLineSegment(sketch, "E1254", {"start": v(-32.71, 4.08) * mm, "end": v(-32.7, 21.79) * mm});
            skLineSegment(sketch, "E1255", {"start": v(-32.7, 21.79) * mm, "end": v(-32.7, 39.5) * mm});
            skLineSegment(sketch, "E1256", {"start": v(-32.7, 39.5) * mm, "end": v(-32.03, 39.98) * mm});
            skFitSpline(sketch, "E1257", {"points": [v(-0.13, 42.04) * mm, v(5.74, 42.01) * mm, v(10.59, 42.05) * mm, v(10.65, 42.12) * mm]});
            skFitSpline(sketch, "E1258", {"points": [v(10.65, 42.12) * mm, v(10.72, 42.2) * mm, v(10.86, 43.07) * mm, v(10.97, 44.08) * mm]});
            skFitSpline(sketch, "E1259", {"points": [v(10.97, 44.08) * mm, v(11.07, 45.09) * mm, v(11.24, 46.11) * mm, v(11.33, 46.36) * mm]});
            skFitSpline(sketch, "E1260", {"points": [v(11.33, 46.36) * mm, v(11.6, 47.07) * mm, v(12.2, 47.22) * mm, v(14, 47) * mm]});
            skFitSpline(sketch, "E1261", {"points": [v(14, 47) * mm, v(16.88, 46.66) * mm, v(19.97, 45.78) * mm, v(23.3, 44.37) * mm]});
            skFitSpline(sketch, "E1262", {"points": [v(23.3, 44.37) * mm, v(25.66, 43.37) * mm, v(31.54, 40.38) * mm, v(32.14, 39.88) * mm]});
            skLineSegment(sketch, "E1263", {"start": v(-11.05, 44.16) * mm, "end": v(-10.78, 42.08) * mm});
            skLineSegment(sketch, "E1264", {"start": v(-10.78, 42.08) * mm, "end": v(-0.13, 42.04) * mm});
            skFitSpline(sketch, "E1265", {"points": [v(33.74, -0.32) * mm, v(34.3, -2.38) * mm, v(34.83, -4.1) * mm, v(34.94, -4.13) * mm]});
            skFitSpline(sketch, "E1266", {"points": [v(34.94, -4.13) * mm, v(35.63, -4.36) * mm, v(37.31, 2.23) * mm, v(37.9, 7.4) * mm]});
            skFitSpline(sketch, "E1267", {"points": [v(37.9, 7.4) * mm, v(38.27, 10.78) * mm, v(38.15, 15.62) * mm, v(37.65, 17.63) * mm]});
            skFitSpline(sketch, "E1268", {"points": [v(37.65, 17.63) * mm, v(37.12, 19.72) * mm, v(36.3, 21.34) * mm, v(35.2, 22.5) * mm]});
            skLineSegment(sketch, "E1269", {"start": v(32.14, 39.88) * mm, "end": v(32.62, 39.47) * mm});
            skLineSegment(sketch, "E1270", {"start": v(32.62, 39.47) * mm, "end": v(32.68, 21.45) * mm});
            skLineSegment(sketch, "E1271", {"start": v(32.68, 21.45) * mm, "end": v(32.73, 3.42) * mm});
            skLineSegment(sketch, "E1272", {"start": v(32.73, 3.42) * mm, "end": v(33.74, -0.32) * mm});
            skFitSpline(sketch, "E1273", {"points": [v(33.96, 34.2) * mm, v(33.68, 44.31) * mm, v(33.65, 44.98) * mm, v(33.3, 46.08) * mm]});
            skFitSpline(sketch, "E1274", {"points": [v(33.3, 46.08) * mm, v(31.84, 50.76) * mm, v(27.9, 54.8) * mm, v(21.88, 57.8) * mm]});
            skFitSpline(sketch, "E1275", {"points": [v(21.88, 57.8) * mm, v(17.6, 59.94) * mm, v(12.81, 61.32) * mm, v(6.97, 62.1) * mm]});
            skFitSpline(sketch, "E1276", {"points": [v(6.97, 62.1) * mm, v(3.78, 62.54) * mm, v(-3.84, 62.54) * mm, v(-7.03, 62.1) * mm]});
            skFitSpline(sketch, "E1277", {"points": [v(-7.03, 62.1) * mm, v(-19.59, 60.41) * mm, v(-28.94, 55.32) * mm, v(-32.5, 48.22) * mm]});
            skFitSpline(sketch, "E1278", {"points": [v(-32.5, 48.22) * mm, v(-33.7, 45.85) * mm, v(-33.7, 45.85) * mm, v(-34, 34.14) * mm]});
            skLineSegment(sketch, "E1279", {"start": v(35.2, 22.5) * mm, "end": v(34.24, 23.5) * mm});
            skLineSegment(sketch, "E1280", {"start": v(34.24, 23.5) * mm, "end": v(33.96, 34.2) * mm});
            skFitSpline(sketch, "E1281", {"points": [v(-35.24, 22.51) * mm, v(-36.36, 21.3) * mm, v(-37.2, 19.64) * mm, v(-37.7, 17.66) * mm]});
            skFitSpline(sketch, "E1282", {"points": [v(-37.7, 17.66) * mm, v(-37.99, 16.54) * mm, v(-38.08, 15.56) * mm, v(-38.15, 12.92) * mm]});
            skFitSpline(sketch, "E1283", {"points": [v(-38.15, 12.92) * mm, v(-38.24, 9.2) * mm, v(-37.92, 5.83) * mm, v(-37.1, 1.96) * mm]});
            skFitSpline(sketch, "E1284", {"points": [v(-37.1, 1.96) * mm, v(-36.41, -1.3) * mm, v(-35.38, -4.25) * mm, v(-34.98, -4.12) * mm]});
            skFitSpline(sketch, "E1285", {"points": [v(-34.98, -4.12) * mm, v(-34.87, -4.1) * mm, v(-34.32, -2.23) * mm, v(-33.75, 0.01) * mm]});
            skLineSegment(sketch, "E1286", {"start": v(-34, 34.14) * mm, "end": v(-34.3, 23.54) * mm});
            skLineSegment(sketch, "E1287", {"start": v(-34.3, 23.54) * mm, "end": v(-35.24, 22.51) * mm});
            skFitSpline(sketch, "E1288", {"points": [v(4.1, 14.5) * mm, v(7.65, 15.03) * mm, v(7.97, 15.14) * mm, v(7.97, 15.85) * mm]});
            skFitSpline(sketch, "E1289", {"points": [v(7.97, 15.85) * mm, v(7.97, 16.01) * mm, v(8.53, 21.37) * mm, v(9.22, 27.76) * mm]});
            skFitSpline(sketch, "E1290", {"points": [v(9.22, 27.76) * mm, v(10.23, 37.08) * mm, v(10.44, 39.41) * mm, v(10.27, 39.52) * mm]});
            skFitSpline(sketch, "E1291", {"points": [v(10.27, 39.52) * mm, v(10.15, 39.6) * mm, v(5.52, 39.66) * mm, v(-0.03, 39.66) * mm]});
            skFitSpline(sketch, "E1292", {"points": [v(-0.03, 39.66) * mm, v(-7.88, 39.66) * mm, v(-10.15, 39.62) * mm, v(-10.31, 39.45) * mm]});
            skFitSpline(sketch, "E1293", {"points": [v(-10.31, 39.45) * mm, v(-10.48, 39.29) * mm, v(-10.26, 36.87) * mm, v(-9.23, 27.3) * mm]});
            skFitSpline(sketch, "E1294", {"points": [v(-9.23, 27.3) * mm, v(-8.52, 20.72) * mm, v(-7.86, 15.27) * mm, v(-7.78, 15.18) * mm]});
            skFitSpline(sketch, "E1295", {"points": [v(-7.78, 15.18) * mm, v(-7.58, 14.99) * mm, v(-1.45, 14.04) * mm, v(-0.24, 14.02) * mm]});
            skFitSpline(sketch, "E1296", {"points": [v(-0.24, 14.02) * mm, v(0.24, 14) * mm, v(2.19, 14.23) * mm, v(4.1, 14.5) * mm]});
            skFitSpline(sketch, "E1297", {"points": [v(-10.78, -64.83) * mm, v(-12.68, -64.57) * mm, v(-15.17, -63.96) * mm, v(-16.03, -63.54) * mm]});
            skFitSpline(sketch, "E1298", {"points": [v(-16.03, -63.54) * mm, v(-17.15, -63) * mm, v(-18.6, -61.56) * mm, v(-19.93, -59.66) * mm]});
            skFitSpline(sketch, "E1299", {"points": [v(-19.93, -59.66) * mm, v(-21.73, -57.07) * mm, v(-32.53, -39.92) * mm, v(-32.53, -39.65) * mm]});
            skFitSpline(sketch, "E1300", {"points": [v(-32.53, -39.65) * mm, v(-32.53, -39.27) * mm, v(-33.66, -23.66) * mm, v(-33.87, -21.17) * mm]});
            skFitSpline(sketch, "E1301", {"points": [v(-33.87, -21.17) * mm, v(-34.22, -16.95) * mm, v(-35.1, -12.66) * mm, v(-36.22, -9.6) * mm]});
            skFitSpline(sketch, "E1302", {"points": [v(-36.22, -9.6) * mm, v(-36.63, -8.5) * mm, v(-36.7, -8.12) * mm, v(-36.6, -7.42) * mm]});
            skFitSpline(sketch, "E1303", {"points": [v(-36.6, -7.42) * mm, v(-36.51, -6.65) * mm, v(-36.56, -6.46) * mm, v(-37.1, -5.48) * mm]});
            skFitSpline(sketch, "E1304", {"points": [v(-37.1, -5.48) * mm, v(-38.32, -3.25) * mm, v(-39.42, 0.9) * mm, v(-40.14, 6) * mm]});
            skFitSpline(sketch, "E1305", {"points": [v(-40.14, 6) * mm, v(-40.56, 9.02) * mm, v(-40.56, 15.38) * mm, v(-40.14, 17.3) * mm]});
            skFitSpline(sketch, "E1306", {"points": [v(-40.14, 17.3) * mm, v(-39.51, 20.17) * mm, v(-38.72, 22) * mm, v(-37.37, 23.67) * mm]});
            skFitSpline(sketch, "E1307", {"points": [v(-36.53, 25.98) * mm, v(-36.52, 29.77) * mm, v(-36.02, 44.7) * mm, v(-35.88, 45.44) * mm]});
            skFitSpline(sketch, "E1308", {"points": [v(-35.88, 45.44) * mm, v(-34.87, 50.66) * mm, v(-30.78, 55.57) * mm, v(-24.5, 59.1) * mm]});
            skFitSpline(sketch, "E1309", {"points": [v(-24.5, 59.1) * mm, v(-20.14, 61.54) * mm, v(-14.02, 63.5) * mm, v(-8.45, 64.24) * mm]});
            skFitSpline(sketch, "E1310", {"points": [v(-8.45, 64.24) * mm, v(-7.35, 64.39) * mm, v(-6.07, 64.58) * mm, v(-5.62, 64.67) * mm]});
            skFitSpline(sketch, "E1311", {"points": [v(-5.62, 64.67) * mm, v(-4.3, 64.92) * mm, v(1.19, 65.04) * mm, v(3.38, 64.85) * mm]});
            skFitSpline(sketch, "E1312", {"points": [v(3.38, 64.85) * mm, v(15.59, 63.84) * mm, v(25.01, 60.2) * mm, v(30.88, 54.26) * mm]});
            skFitSpline(sketch, "E1313", {"points": [v(30.88, 54.26) * mm, v(32.58, 52.53) * mm, v(33.7, 50.96) * mm, v(34.65, 48.92) * mm]});
            skFitSpline(sketch, "E1314", {"points": [v(34.65, 48.92) * mm, v(35.91, 46.22) * mm, v(35.95, 45.93) * mm, v(36.22, 36.33) * mm]});
            skFitSpline(sketch, "E1315", {"points": [v(36.22, 36.33) * mm, v(36.35, 31.61) * mm, v(36.46, 27.07) * mm, v(36.46, 26.23) * mm]});
            skLineSegment(sketch, "E1316", {"start": v(-37.37, 23.67) * mm, "end": v(-36.53, 24.72) * mm});
            skLineSegment(sketch, "E1317", {"start": v(-36.53, 24.72) * mm, "end": v(-36.53, 25.98) * mm});
            skFitSpline(sketch, "E1318", {"points": [v(37.33, 23.65) * mm, v(39.66, 20.76) * mm, v(40.58, 17) * mm, v(40.41, 11.1) * mm]});
            skFitSpline(sketch, "E1319", {"points": [v(40.41, 11.1) * mm, v(40.23, 4.58) * mm, v(38.85, -2.17) * mm, v(37.03, -5.48) * mm]});
            skFitSpline(sketch, "E1320", {"points": [v(37.03, -5.48) * mm, v(36.5, -6.45) * mm, v(36.44, -6.66) * mm, v(36.54, -7.38) * mm]});
            skFitSpline(sketch, "E1321", {"points": [v(36.54, -7.38) * mm, v(36.63, -8.05) * mm, v(36.53, -8.53) * mm, v(35.96, -10.27) * mm]});
            skFitSpline(sketch, "E1322", {"points": [v(35.96, -10.27) * mm, v(34.25, -15.55) * mm, v(34.1, -16.67) * mm, v(32.88, -33.75) * mm]});
            skFitSpline(sketch, "E1323", {"points": [v(32.88, -33.75) * mm, v(32.65, -37.05) * mm, v(32.42, -39.84) * mm, v(32.39, -39.95) * mm]});
            skFitSpline(sketch, "E1324", {"points": [v(32.39, -39.95) * mm, v(32.28, -40.26) * mm, v(20.52, -58.78) * mm, v(19.67, -59.98) * mm]});
            skFitSpline(sketch, "E1325", {"points": [v(19.67, -59.98) * mm, v(18.51, -61.62) * mm, v(16.96, -63.1) * mm, v(15.94, -63.57) * mm]});
            skFitSpline(sketch, "E1326", {"points": [v(15.94, -63.57) * mm, v(15.12, -63.95) * mm, v(12.75, -64.52) * mm, v(10.72, -64.84) * mm]});
            skFitSpline(sketch, "E1327", {"points": [v(10.72, -64.84) * mm, v(9.7, -65) * mm, v(-9.63, -65) * mm, v(-10.78, -64.83) * mm]});
            skLineSegment(sketch, "E1328", {"start": v(36.46, 26.23) * mm, "end": v(36.46, 24.72) * mm});
            skLineSegment(sketch, "E1329", {"start": v(36.46, 24.72) * mm, "end": v(37.33, 23.65) * mm});
            skFitSpline(sketch, "E1330", {"points": [v(8.97, -62.65) * mm, v(11.73, -62.44) * mm, v(14.1, -61.97) * mm, v(15.12, -61.45) * mm]});
            skFitSpline(sketch, "E1331", {"points": [v(15.12, -61.45) * mm, v(15.6, -61.21) * mm, v(16.27, -60.6) * mm, v(16.9, -59.85) * mm]});
            skFitSpline(sketch, "E1332", {"points": [v(16.9, -59.85) * mm, v(17.72, -58.87) * mm, v(27.22, -44.17) * mm, v(29.66, -40.1) * mm]});
            skFitSpline(sketch, "E1333", {"points": [v(30.88, -30.58) * mm, v(31.62, -20.23) * mm, v(31.59, -20.8) * mm, v(31.36, -20.72) * mm]});
            skFitSpline(sketch, "E1334", {"points": [v(31.36, -20.72) * mm, v(31.26, -20.68) * mm, v(30.79, -21.31) * mm, v(30.31, -22.12) * mm]});
            skFitSpline(sketch, "E1335", {"points": [v(30.31, -22.12) * mm, v(29.84, -22.92) * mm, v(28.44, -25) * mm, v(27.2, -26.74) * mm]});
            skFitSpline(sketch, "E1336", {"points": [v(27.2, -26.74) * mm, v(25.96, -28.47) * mm, v(24.5, -30.68) * mm, v(23.96, -31.65) * mm]});
            skFitSpline(sketch, "E1337", {"points": [v(23.96, -31.65) * mm, v(22.86, -33.6) * mm, v(21.27, -37.22) * mm, v(20.4, -39.78) * mm]});
            skLineSegment(sketch, "E1338", {"start": v(29.66, -40.1) * mm, "end": v(30.27, -39.08) * mm});
            skLineSegment(sketch, "E1339", {"start": v(30.27, -39.08) * mm, "end": v(30.88, -30.58) * mm});
            skFitSpline(sketch, "E1340", {"points": [v(20.39, -48.25) * mm, v(19.52, -50.46) * mm, v(17.46, -54.46) * mm, v(16.78, -55.23) * mm]});
            skFitSpline(sketch, "E1341", {"points": [v(16.78, -55.23) * mm, v(15.64, -56.52) * mm, v(14.07, -56.64) * mm, v(11.12, -55.65) * mm]});
            skFitSpline(sketch, "E1342", {"points": [v(11.12, -55.65) * mm, v(10.3, -55.38) * mm, v(9.55, -55.2) * mm, v(9.47, -55.25) * mm]});
            skFitSpline(sketch, "E1343", {"points": [v(9.47, -55.25) * mm, v(9.38, -55.3) * mm, v(9.1, -56) * mm, v(8.85, -56.8) * mm]});
            skFitSpline(sketch, "E1344", {"points": [v(8.85, -56.8) * mm, v(8.6, -57.6) * mm, v(8.23, -58.41) * mm, v(8.03, -58.62) * mm]});
            skLineSegment(sketch, "E1345", {"start": v(20.4, -39.78) * mm, "end": v(19.83, -41.42) * mm});
            skLineSegment(sketch, "E1346", {"start": v(19.83, -41.42) * mm, "end": v(20.33, -44.26) * mm});
            skLineSegment(sketch, "E1347", {"start": v(20.33, -44.26) * mm, "end": v(20.84, -47.1) * mm});
            skLineSegment(sketch, "E1348", {"start": v(20.84, -47.1) * mm, "end": v(20.39, -48.25) * mm});
            skFitSpline(sketch, "E1349", {"points": [v(0.01, -59) * mm, v(-6.5, -59) * mm, v(-7.68, -58.96) * mm, v(-7.98, -58.75) * mm]});
            skFitSpline(sketch, "E1350", {"points": [v(-7.98, -58.75) * mm, v(-8.2, -58.59) * mm, v(-8.53, -57.92) * mm, v(-8.87, -56.92) * mm]});
            skFitSpline(sketch, "E1351", {"points": [v(-8.87, -56.92) * mm, v(-9.15, -56.05) * mm, v(-9.46, -55.3) * mm, v(-9.54, -55.24) * mm]});
            skFitSpline(sketch, "E1352", {"points": [v(-9.54, -55.24) * mm, v(-9.63, -55.19) * mm, v(-10.39, -55.39) * mm, v(-11.24, -55.68) * mm]});
            skFitSpline(sketch, "E1353", {"points": [v(-11.24, -55.68) * mm, v(-12.48, -56.11) * mm, v(-13.06, -56.22) * mm, v(-14.2, -56.23) * mm]});
            skFitSpline(sketch, "E1354", {"points": [v(-14.2, -56.23) * mm, v(-15.86, -56.25) * mm, v(-16.22, -56.08) * mm, v(-17.12, -54.87) * mm]});
            skFitSpline(sketch, "E1355", {"points": [v(-17.12, -54.87) * mm, v(-17.77, -54) * mm, v(-19.74, -50.06) * mm, v(-20.44, -48.23) * mm]});
            skLineSegment(sketch, "E1356", {"start": v(8.03, -58.62) * mm, "end": v(7.65, -59) * mm});
            skLineSegment(sketch, "E1357", {"start": v(7.65, -59) * mm, "end": v(0.01, -59) * mm});
            skFitSpline(sketch, "E1358", {"points": [v(-20.3, -40.17) * mm, v(-21.86, -35.61) * mm, v(-24.14, -30.93) * mm, v(-25.8, -28.88) * mm]});
            skFitSpline(sketch, "E1359", {"points": [v(-25.8, -28.88) * mm, v(-26.57, -27.94) * mm, v(-29.63, -23.38) * mm, v(-30.51, -21.86) * mm]});
            skFitSpline(sketch, "E1360", {"points": [v(-30.51, -21.86) * mm, v(-30.9, -21.2) * mm, v(-31.31, -20.68) * mm, v(-31.42, -20.71) * mm]});
            skFitSpline(sketch, "E1361", {"points": [v(-31.42, -20.71) * mm, v(-31.65, -20.8) * mm, v(-31.67, -20.27) * mm, v(-31.04, -29.08) * mm]});
            skFitSpline(sketch, "E1362", {"points": [v(-31.04, -29.08) * mm, v(-30.77, -32.84) * mm, v(-30.5, -36.65) * mm, v(-30.43, -37.55) * mm]});
            skLineSegment(sketch, "E1363", {"start": v(-20.44, -48.23) * mm, "end": v(-20.9, -47.06) * mm});
            skLineSegment(sketch, "E1364", {"start": v(-20.9, -47.06) * mm, "end": v(-20.39, -44.24) * mm});
            skLineSegment(sketch, "E1365", {"start": v(-20.39, -44.24) * mm, "end": v(-19.88, -41.42) * mm});
            skLineSegment(sketch, "E1366", {"start": v(-19.88, -41.42) * mm, "end": v(-20.3, -40.17) * mm});
            skFitSpline(sketch, "E1367", {"points": [v(-24.33, -48.63) * mm, v(-21.03, -53.83) * mm, v(-17.92, -58.62) * mm, v(-17.42, -59.29) * mm]});
            skFitSpline(sketch, "E1368", {"points": [v(-17.42, -59.29) * mm, v(-16.26, -60.81) * mm, v(-15.45, -61.45) * mm, v(-14.2, -61.84) * mm]});
            skFitSpline(sketch, "E1369", {"points": [v(-14.2, -61.84) * mm, v(-13.2, -62.15) * mm, v(-10.23, -62.6) * mm, v(-8.53, -62.71) * mm]});
            skFitSpline(sketch, "E1370", {"points": [v(-8.53, -62.71) * mm, v(-6.2, -62.85) * mm, v(6.98, -62.81) * mm, v(8.97, -62.65) * mm]});
            skLineSegment(sketch, "E1371", {"start": v(-30.43, -37.55) * mm, "end": v(-30.32, -39.18) * mm});
            skLineSegment(sketch, "E1372", {"start": v(-30.32, -39.18) * mm, "end": v(-24.33, -48.63) * mm});
            skFitSpline(sketch, "E1373", {"points": [v(6.46, -56.5) * mm, v(6.8, -56.16) * mm, v(7.06, -55.16) * mm, v(6.9, -54.75) * mm]});
            skFitSpline(sketch, "E1374", {"points": [v(6.9, -54.75) * mm, v(6.82, -54.53) * mm, v(5.91, -54.5) * mm, v(-0.02, -54.5) * mm]});
            skFitSpline(sketch, "E1375", {"points": [v(-0.02, -54.5) * mm, v(-4.55, -54.5) * mm, v(-6.88, -54.56) * mm, v(-6.95, -54.67) * mm]});
            skFitSpline(sketch, "E1376", {"points": [v(-6.95, -54.67) * mm, v(-7.14, -54.97) * mm, v(-6.85, -56.18) * mm, v(-6.51, -56.51) * mm]});
            skFitSpline(sketch, "E1377", {"points": [v(-6.51, -56.51) * mm, v(-6.22, -56.81) * mm, v(-5.86, -56.83) * mm, v(-0.03, -56.83) * mm]});
            skFitSpline(sketch, "E1378", {"points": [v(-0.03, -56.83) * mm, v(5.85, -56.83) * mm, v(6.15, -56.82) * mm, v(6.46, -56.5) * mm]});
            skFitSpline(sketch, "E1379", {"points": [v(-12, -53.55) * mm, v(-9.82, -52.83) * mm, v(-9.88, -53) * mm, v(-10.67, -50.1) * mm]});
            skFitSpline(sketch, "E1380", {"points": [v(-10.67, -50.1) * mm, v(-11.04, -48.73) * mm, v(-11.42, -47.54) * mm, v(-11.52, -47.44) * mm]});
            skFitSpline(sketch, "E1381", {"points": [v(-11.52, -47.44) * mm, v(-11.65, -47.31) * mm, v(-12.02, -47.57) * mm, v(-12.83, -48.36) * mm]});
            skFitSpline(sketch, "E1382", {"points": [v(-12.83, -48.36) * mm, v(-14.08, -49.6) * mm, v(-14.53, -49.81) * mm, v(-15.08, -49.45) * mm]});
            skFitSpline(sketch, "E1383", {"points": [v(-15.08, -49.45) * mm, v(-15.28, -49.32) * mm, v(-15.97, -48.3) * mm, v(-16.62, -47.18) * mm]});
            skFitSpline(sketch, "E1384", {"points": [v(-16.62, -47.18) * mm, v(-17.91, -44.93) * mm, v(-18.19, -44.76) * mm, v(-18.44, -46.05) * mm]});
            skFitSpline(sketch, "E1385", {"points": [v(-18.44, -46.05) * mm, v(-18.57, -46.72) * mm, v(-18.53, -46.98) * mm, v(-18.2, -47.8) * mm]});
            skFitSpline(sketch, "E1386", {"points": [v(-18.2, -47.8) * mm, v(-17.38, -49.82) * mm, v(-15.68, -53.15) * mm, v(-15.2, -53.67) * mm]});
            skFitSpline(sketch, "E1387", {"points": [v(-15.2, -53.67) * mm, v(-14.74, -54.16) * mm, v(-14.63, -54.2) * mm, v(-14, -54.1) * mm]});
            skFitSpline(sketch, "E1388", {"points": [v(-14, -54.1) * mm, v(-13.63, -54.04) * mm, v(-12.72, -53.79) * mm, v(-12, -53.55) * mm]});
            skFitSpline(sketch, "E1389", {"points": [v(15.15, -53.65) * mm, v(15.62, -53.14) * mm, v(17.35, -49.75) * mm, v(18.14, -47.8) * mm]});
            skFitSpline(sketch, "E1390", {"points": [v(18.14, -47.8) * mm, v(18.46, -46.99) * mm, v(18.5, -46.72) * mm, v(18.37, -46.04) * mm]});
            skFitSpline(sketch, "E1391", {"points": [v(18.37, -46.04) * mm, v(18.27, -45.52) * mm, v(18.13, -45.25) * mm, v(17.97, -45.25) * mm]});
            skFitSpline(sketch, "E1392", {"points": [v(17.97, -45.25) * mm, v(17.83, -45.25) * mm, v(17.2, -46.12) * mm, v(16.54, -47.23) * mm]});
            skFitSpline(sketch, "E1393", {"points": [v(16.54, -47.23) * mm, v(15.88, -48.32) * mm, v(15.2, -49.32) * mm, v(15.03, -49.45) * mm]});
            skFitSpline(sketch, "E1394", {"points": [v(15.03, -49.45) * mm, v(14.52, -49.82) * mm, v(13.96, -49.56) * mm, v(12.76, -48.37) * mm]});
            skFitSpline(sketch, "E1395", {"points": [v(12.76, -48.37) * mm, v(12.01, -47.63) * mm, v(11.58, -47.32) * mm, v(11.47, -47.43) * mm]});
            skFitSpline(sketch, "E1396", {"points": [v(11.47, -47.43) * mm, v(11.22, -47.67) * mm, v(9.94, -52.48) * mm, v(10.06, -52.68) * mm]});
            skFitSpline(sketch, "E1397", {"points": [v(10.06, -52.68) * mm, v(10.3, -53.06) * mm, v(13.42, -54.13) * mm, v(14.36, -54.15) * mm]});
            skFitSpline(sketch, "E1398", {"points": [v(14.36, -54.15) * mm, v(14.53, -54.16) * mm, v(14.88, -53.93) * mm, v(15.15, -53.65) * mm]});
            skFitSpline(sketch, "E1399", {"points": [v(7.57, -52.2) * mm, v(7.9, -52) * mm, v(9.3, -46.46) * mm, v(9.1, -46.21) * mm]});
            skFitSpline(sketch, "E1400", {"points": [v(9.1, -46.21) * mm, v(8.85, -45.9) * mm, v(-8.9, -45.9) * mm, v(-9.16, -46.2) * mm]});
            skFitSpline(sketch, "E1401", {"points": [v(-9.16, -46.2) * mm, v(-9.33, -46.4) * mm, v(-9.24, -46.8) * mm, v(-8.11, -50.98) * mm]});
            skFitSpline(sketch, "E1402", {"points": [v(-8.11, -50.98) * mm, v(-7.98, -51.47) * mm, v(-7.79, -51.97) * mm, v(-7.68, -52.1) * mm]});
            skFitSpline(sketch, "E1403", {"points": [v(-7.68, -52.1) * mm, v(-7.53, -52.3) * mm, v(-6.18, -52.33) * mm, v(-0.05, -52.33) * mm]});
            skFitSpline(sketch, "E1404", {"points": [v(-0.05, -52.33) * mm, v(4.04, -52.33) * mm, v(7.47, -52.27) * mm, v(7.57, -52.2) * mm]});
            skFitSpline(sketch, "E1405", {"points": [v(-13.23, -45.62) * mm, v(-12.85, -45.22) * mm, v(-12.53, -44.77) * mm, v(-12.53, -44.61) * mm]});
            skFitSpline(sketch, "E1406", {"points": [v(-12.53, -44.61) * mm, v(-12.53, -44.18) * mm, v(-13.22, -42.92) * mm, v(-14.2, -41.52) * mm]});
            skFitSpline(sketch, "E1407", {"points": [v(-14.2, -41.52) * mm, v(-15.06, -40.3) * mm, v(-18.61, -36.5) * mm, v(-18.89, -36.5) * mm]});
            skFitSpline(sketch, "E1408", {"points": [v(-18.89, -36.5) * mm, v(-18.97, -36.5) * mm, v(-19.03, -36.63) * mm, v(-19.03, -36.8) * mm]});
            skFitSpline(sketch, "E1409", {"points": [v(-19.03, -36.8) * mm, v(-19.03, -37.26) * mm, v(-17.72, -40.85) * mm, v(-17.25, -41.66) * mm]});
            skFitSpline(sketch, "E1410", {"points": [v(-17.25, -41.66) * mm, v(-15.16, -45.28) * mm, v(-14.48, -46.33) * mm, v(-14.22, -46.33) * mm]});
            skFitSpline(sketch, "E1411", {"points": [v(-14.22, -46.33) * mm, v(-14.06, -46.33) * mm, v(-13.62, -46) * mm, v(-13.23, -45.62) * mm]});
            skFitSpline(sketch, "E1412", {"points": [v(16.04, -43.64) * mm, v(17.21, -41.65) * mm, v(17.76, -40.5) * mm, v(18.37, -38.75) * mm]});
            skFitSpline(sketch, "E1413", {"points": [v(18.37, -38.75) * mm, v(18.8, -37.5) * mm, v(19.12, -36.43) * mm, v(19.06, -36.37) * mm]});
            skFitSpline(sketch, "E1414", {"points": [v(19.06, -36.37) * mm, v(18.93, -36.24) * mm, v(17.5, -37.64) * mm, v(15.65, -39.7) * mm]});
            skFitSpline(sketch, "E1415", {"points": [v(15.65, -39.7) * mm, v(14.2, -41.31) * mm, v(12.47, -43.95) * mm, v(12.47, -44.53) * mm]});
            skFitSpline(sketch, "E1416", {"points": [v(12.47, -44.53) * mm, v(12.47, -45) * mm, v(13.8, -46.36) * mm, v(14.19, -46.3) * mm]});
            skFitSpline(sketch, "E1417", {"points": [v(14.19, -46.3) * mm, v(14.41, -46.26) * mm, v(14.99, -45.44) * mm, v(16.04, -43.64) * mm]});
            skFitSpline(sketch, "E1418", {"points": [v(10.94, -42.41) * mm, v(12.02, -40.44) * mm, v(13.13, -39.04) * mm, v(16.16, -35.84) * mm]});
            skFitSpline(sketch, "E1419", {"points": [v(16.16, -35.84) * mm, v(22.3, -29.36) * mm, v(24.12, -27.27) * mm, v(25.7, -24.93) * mm]});
            skFitSpline(sketch, "E1420", {"points": [v(25.7, -24.93) * mm, v(27.14, -22.76) * mm, v(27.56, -21.12) * mm, v(27.8, -16.58) * mm]});
            skFitSpline(sketch, "E1421", {"points": [v(27.8, -16.58) * mm, v(27.89, -14.84) * mm, v(28.05, -12.53) * mm, v(28.16, -11.46) * mm]});
            skFitSpline(sketch, "E1422", {"points": [v(28.16, -11.46) * mm, v(28.42, -8.96) * mm, v(28.32, -8.83) * mm, v(27.11, -10.09) * mm]});
            skFitSpline(sketch, "E1423", {"points": [v(27.11, -10.09) * mm, v(25.52, -11.76) * mm, v(22.64, -13.4) * mm, v(19.96, -14.14) * mm]});
            skFitSpline(sketch, "E1424", {"points": [v(19.96, -14.14) * mm, v(17.33, -14.88) * mm, v(10.94, -16.07) * mm, v(10.37, -15.93) * mm]});
            skFitSpline(sketch, "E1425", {"points": [v(10.37, -15.93) * mm, v(9.9, -15.8) * mm, v(8.1, -13.6) * mm, v(7.6, -12.5) * mm]});
            skFitSpline(sketch, "E1426", {"points": [v(7.6, -12.5) * mm, v(7.16, -11.54) * mm, v(7.16, -11.54) * mm, v(5.22, -11.94) * mm]});
            skFitSpline(sketch, "E1427", {"points": [v(5.22, -11.94) * mm, v(3.22, -12.36) * mm, v(-3.03, -12.36) * mm, v(-5.25, -11.94) * mm]});
            skFitSpline(sketch, "E1428", {"points": [v(-5.25, -11.94) * mm, v(-6.14, -11.77) * mm, v(-6.98, -11.67) * mm, v(-7.1, -11.72) * mm]});
            skFitSpline(sketch, "E1429", {"points": [v(-7.1, -11.72) * mm, v(-7.22, -11.77) * mm, v(-7.5, -12.16) * mm, v(-7.7, -12.6) * mm]});
            skFitSpline(sketch, "E1430", {"points": [v(-7.7, -12.6) * mm, v(-8.25, -13.73) * mm, v(-9.98, -15.81) * mm, v(-10.48, -15.94) * mm]});
            skFitSpline(sketch, "E1431", {"points": [v(-10.48, -15.94) * mm, v(-11, -16.07) * mm, v(-18.36, -14.65) * mm, v(-20.24, -14.06) * mm]});
            skFitSpline(sketch, "E1432", {"points": [v(-20.24, -14.06) * mm, v(-23.2, -13.13) * mm, v(-25.75, -11.66) * mm, v(-27.2, -10.04) * mm]});
            skFitSpline(sketch, "E1433", {"points": [v(-27.2, -10.04) * mm, v(-28.36, -8.74) * mm, v(-28.5, -8.91) * mm, v(-28.23, -11.37) * mm]});
            skFitSpline(sketch, "E1434", {"points": [v(-28.23, -11.37) * mm, v(-28.12, -12.4) * mm, v(-27.95, -14.68) * mm, v(-27.86, -16.44) * mm]});
            skFitSpline(sketch, "E1435", {"points": [v(-27.86, -16.44) * mm, v(-27.67, -20.34) * mm, v(-27.32, -22.15) * mm, v(-26.44, -23.86) * mm]});
            skFitSpline(sketch, "E1436", {"points": [v(-26.44, -23.86) * mm, v(-25.95, -24.8) * mm, v(-23.07, -28.77) * mm, v(-22.07, -29.87) * mm]});
            skFitSpline(sketch, "E1437", {"points": [v(-22.07, -29.87) * mm, v(-21.55, -30.45) * mm, v(-19.4, -32.68) * mm, v(-17.28, -34.83) * mm]});
            skFitSpline(sketch, "E1438", {"points": [v(-17.28, -34.83) * mm, v(-13.3, -38.88) * mm, v(-12.28, -40.1) * mm, v(-11.25, -41.98) * mm]});
            skFitSpline(sketch, "E1439", {"points": [v(-11.25, -41.98) * mm, v(-10.92, -42.59) * mm, v(-10.55, -43.25) * mm, v(-10.42, -43.46) * mm]});
            skFitSpline(sketch, "E1440", {"points": [v(-30.26, -14.62) * mm, v(-30.31, -13.41) * mm, v(-30.4, -11.54) * mm, v(-30.46, -10.46) * mm]});
            skFitSpline(sketch, "E1441", {"points": [v(-30.46, -10.46) * mm, v(-30.63, -7.54) * mm, v(-30, -3.44) * mm, v(-28.68, 1.23) * mm]});
            skLineSegment(sketch, "E1442", {"start": v(-10.42, -43.46) * mm, "end": v(-10.19, -43.83) * mm});
            skLineSegment(sketch, "E1443", {"start": v(-10.19, -43.83) * mm, "end": v(0, -43.8) * mm});
            skLineSegment(sketch, "E1444", {"start": v(0, -43.8) * mm, "end": v(10.2, -43.75) * mm});
            skLineSegment(sketch, "E1445", {"start": v(10.2, -43.75) * mm, "end": v(10.94, -42.41) * mm});
            skFitSpline(sketch, "E1446", {"points": [v(-28.24, 10.73) * mm, v(-28.33, 18.88) * mm, v(-28.45, 20.52) * mm, v(-29.3, 25.33) * mm]});
            skFitSpline(sketch, "E1447", {"points": [v(-29.3, 25.33) * mm, v(-29.92, 28.89) * mm, v(-30.2, 29.65) * mm, v(-30.43, 28.48) * mm]});
            skFitSpline(sketch, "E1448", {"points": [v(-30.43, 28.48) * mm, v(-30.48, 28.2) * mm, v(-30.53, 22.41) * mm, v(-30.53, 15.64) * mm]});
            skLineSegment(sketch, "E1449", {"start": v(-28.68, 1.23) * mm, "end": v(-28.16, 3.05) * mm});
            skLineSegment(sketch, "E1450", {"start": v(-28.16, 3.05) * mm, "end": v(-28.24, 10.73) * mm});
            skFitSpline(sketch, "E1451", {"points": [v(-32.11, -3) * mm, v(-32.99, -6.48) * mm, v(-33.7, -9.47) * mm, v(-33.7, -9.64) * mm]});
            skFitSpline(sketch, "E1452", {"points": [v(-33.7, -9.64) * mm, v(-33.7, -9.96) * mm, v(-31.95, -14.01) * mm, v(-31.02, -15.85) * mm]});
            skFitSpline(sketch, "E1453", {"points": [v(-31.02, -15.85) * mm, v(-30.26, -17.35) * mm, v(-30.14, -17.16) * mm, v(-30.26, -14.62) * mm]});
            skLineSegment(sketch, "E1454", {"start": v(-30.53, 15.64) * mm, "end": v(-30.53, 3.33) * mm});
            skLineSegment(sketch, "E1455", {"start": v(-30.53, 3.33) * mm, "end": v(-32.11, -3) * mm});
            skFitSpline(sketch, "E1456", {"points": [v(30.92, -16) * mm, v(31.91, -13.98) * mm, v(33.63, -9.92) * mm, v(33.63, -9.58) * mm]});
            skFitSpline(sketch, "E1457", {"points": [v(33.63, -9.58) * mm, v(33.63, -9.36) * mm, v(32.92, -6.38) * mm, v(32.05, -2.96) * mm]});
            skFitSpline(sketch, "E1458", {"points": [v(30.45, 15.84) * mm, v(30.45, 22.76) * mm, v(30.38, 28.56) * mm, v(30.31, 28.74) * mm]});
            skFitSpline(sketch, "E1459", {"points": [v(30.31, 28.74) * mm, v(30.19, 29.07) * mm, v(30.18, 29.07) * mm, v(30, 28.73) * mm]});
            skFitSpline(sketch, "E1460", {"points": [v(30, 28.73) * mm, v(29.78, 28.31) * mm, v(29.07, 24.57) * mm, v(28.72, 22) * mm]});
            skFitSpline(sketch, "E1461", {"points": [v(28.72, 22) * mm, v(28.28, 18.75) * mm, v(28.14, 15.5) * mm, v(28.14, 9.08) * mm]});
            skLineSegment(sketch, "E1462", {"start": v(32.05, -2.96) * mm, "end": v(30.47, 3.27) * mm});
            skLineSegment(sketch, "E1463", {"start": v(30.47, 3.27) * mm, "end": v(30.45, 15.84) * mm});
            skFitSpline(sketch, "E1464", {"points": [v(28.71, 0.86) * mm, v(30, -3.74) * mm, v(30.56, -7.44) * mm, v(30.4, -10.45) * mm]});
            skFitSpline(sketch, "E1465", {"points": [v(30.4, -10.45) * mm, v(30.08, -16.88) * mm, v(30.08, -16.88) * mm, v(30.32, -16.8) * mm]});
            skFitSpline(sketch, "E1466", {"points": [v(30.32, -16.8) * mm, v(30.44, -16.76) * mm, v(30.71, -16.4) * mm, v(30.92, -16) * mm]});
            skLineSegment(sketch, "E1467", {"start": v(28.14, 9.08) * mm, "end": v(28.14, 2.92) * mm});
            skLineSegment(sketch, "E1468", {"start": v(28.14, 2.92) * mm, "end": v(28.71, 0.86) * mm});
            skFitSpline(sketch, "E1469", {"points": [v(-10.4, -12.63) * mm, v(-9.85, -11.93) * mm, v(-9.65, -11.52) * mm, v(-9.64, -11.07) * mm]});
            skFitSpline(sketch, "E1470", {"points": [v(-11.87, -9.2) * mm, v(-17.6, -6.03) * mm, v(-25.97, -1.93) * mm, v(-26.5, -2.04) * mm]});
            skFitSpline(sketch, "E1471", {"points": [v(-26.5, -2.04) * mm, v(-27.07, -2.14) * mm, v(-27.13, -5.19) * mm, v(-26.6, -6.85) * mm]});
            skFitSpline(sketch, "E1472", {"points": [v(-26.6, -6.85) * mm, v(-26.02, -8.66) * mm, v(-23.55, -10.55) * mm, v(-20.19, -11.74) * mm]});
            skFitSpline(sketch, "E1473", {"points": [v(-20.19, -11.74) * mm, v(-18.9, -12.2) * mm, v(-12.05, -13.67) * mm, v(-11.46, -13.61) * mm]});
            skFitSpline(sketch, "E1474", {"points": [v(-11.46, -13.61) * mm, v(-11.28, -13.6) * mm, v(-10.8, -13.15) * mm, v(-10.4, -12.63) * mm]});
            skLineSegment(sketch, "E1475", {"start": v(-9.64, -11.07) * mm, "end": v(-9.62, -10.45) * mm});
            skLineSegment(sketch, "E1476", {"start": v(-9.62, -10.45) * mm, "end": v(-11.87, -9.2) * mm});
            skFitSpline(sketch, "E1477", {"points": [v(15.23, -12.91) * mm, v(20.47, -11.87) * mm, v(22.98, -10.86) * mm, v(25.03, -9) * mm]});
            skFitSpline(sketch, "E1478", {"points": [v(25.03, -9) * mm, v(26.1, -8.02) * mm, v(26.58, -7.11) * mm, v(26.82, -5.64) * mm]});
            skFitSpline(sketch, "E1479", {"points": [v(26.82, -5.64) * mm, v(27.04, -4.3) * mm, v(26.86, -2.18) * mm, v(26.52, -2.05) * mm]});
            skFitSpline(sketch, "E1480", {"points": [v(26.52, -2.05) * mm, v(26.4, -2) * mm, v(25.97, -2.1) * mm, v(25.58, -2.26) * mm]});
            skFitSpline(sketch, "E1481", {"points": [v(25.58, -2.26) * mm, v(23.76, -3.04) * mm, v(15.54, -7.16) * mm, v(12.72, -8.7) * mm]});
            skFitSpline(sketch, "E1482", {"points": [v(12.72, -8.7) * mm, v(9.28, -10.58) * mm, v(9.2, -10.66) * mm, v(9.73, -11.7) * mm]});
            skFitSpline(sketch, "E1483", {"points": [v(9.73, -11.7) * mm, v(10.07, -12.38) * mm, v(11.1, -13.67) * mm, v(11.3, -13.67) * mm]});
            skFitSpline(sketch, "E1484", {"points": [v(11.3, -13.67) * mm, v(11.38, -13.67) * mm, v(13.15, -13.33) * mm, v(15.23, -12.91) * mm]});
            skFitSpline(sketch, "E1485", {"points": [v(4.56, -9.75) * mm, v(6.66, -9.41) * mm, v(6.98, -9.28) * mm, v(11.42, -6.86) * mm]});
            skFitSpline(sketch, "E1486", {"points": [v(11.42, -6.86) * mm, v(15.75, -4.5) * mm, v(20.02, -2.35) * mm, v(23.86, -0.58) * mm]});
            skFitSpline(sketch, "E1487", {"points": [v(26.2, 1.15) * mm, v(26, 2.22) * mm, v(25.93, 16.09) * mm, v(26.13, 18.58) * mm]});
            skFitSpline(sketch, "E1488", {"points": [v(26.13, 18.58) * mm, v(26.58, 24.21) * mm, v(27.82, 30.71) * mm, v(29.52, 36.27) * mm]});
            skFitSpline(sketch, "E1489", {"points": [v(29.52, 36.27) * mm, v(29.92, 37.61) * mm, v(30.04, 38.21) * mm, v(29.92, 38.42) * mm]});
            skFitSpline(sketch, "E1490", {"points": [v(29.92, 38.42) * mm, v(29.72, 38.78) * mm, v(22.95, 42.08) * mm, v(20.73, 42.91) * mm]});
            skFitSpline(sketch, "E1491", {"points": [v(20.73, 42.91) * mm, v(18.74, 43.65) * mm, v(15.76, 44.45) * mm, v(14.44, 44.6) * mm]});
            skFitSpline(sketch, "E1492", {"points": [v(14.44, 44.6) * mm, v(13.53, 44.7) * mm, v(13.48, 44.68) * mm, v(13.38, 44.3) * mm]});
            skFitSpline(sketch, "E1493", {"points": [v(13.38, 44.3) * mm, v(13.33, 44.1) * mm, v(12.55, 37.1) * mm, v(11.65, 28.78) * mm]});
            skFitSpline(sketch, "E1494", {"points": [v(11.65, 28.78) * mm, v(10.16, 15) * mm, v(9.99, 13.61) * mm, v(9.68, 13.3) * mm]});
            skFitSpline(sketch, "E1495", {"points": [v(9.68, 13.3) * mm, v(9.4, 13.02) * mm, v(8.6, 12.85) * mm, v(5.03, 12.32) * mm]});
            skFitSpline(sketch, "E1496", {"points": [v(5.03, 12.32) * mm, v(2.66, 11.96) * mm, v(0.38, 11.67) * mm, v(-0.03, 11.67) * mm]});
            skFitSpline(sketch, "E1497", {"points": [v(-0.03, 11.67) * mm, v(-0.45, 11.67) * mm, v(-2.72, 11.96) * mm, v(-5.1, 12.32) * mm]});
            skFitSpline(sketch, "E1498", {"points": [v(-5.1, 12.32) * mm, v(-8.64, 12.85) * mm, v(-9.46, 13.02) * mm, v(-9.74, 13.3) * mm]});
            skFitSpline(sketch, "E1499", {"points": [v(-9.74, 13.3) * mm, v(-10.04, 13.6) * mm, v(-10.23, 15.1) * mm, v(-11.72, 28.94) * mm]});
            skFitSpline(sketch, "E1500", {"points": [v(-11.72, 28.94) * mm, v(-12.63, 37.36) * mm, v(-13.41, 44.35) * mm, v(-13.46, 44.48) * mm]});
            skFitSpline(sketch, "E1501", {"points": [v(-13.46, 44.48) * mm, v(-13.57, 44.8) * mm, v(-14.95, 44.62) * mm, v(-17.3, 44) * mm]});
            skFitSpline(sketch, "E1502", {"points": [v(-17.3, 44) * mm, v(-20.13, 43.26) * mm, v(-22.29, 42.4) * mm, v(-26.27, 40.41) * mm]});
            skFitSpline(sketch, "E1503", {"points": [v(-26.27, 40.41) * mm, v(-29.16, 38.97) * mm, v(-29.96, 38.5) * mm, v(-30, 38.23) * mm]});
            skFitSpline(sketch, "E1504", {"points": [v(-30, 38.23) * mm, v(-30.03, 38.04) * mm, v(-29.79, 36.99) * mm, v(-29.47, 35.9) * mm]});
            skFitSpline(sketch, "E1505", {"points": [v(-29.47, 35.9) * mm, v(-27.76, 30.1) * mm, v(-26.68, 24.41) * mm, v(-26.2, 18.66) * mm]});
            skFitSpline(sketch, "E1506", {"points": [v(-26.2, 18.66) * mm, v(-26, 16.27) * mm, v(-26.05, 2.23) * mm, v(-26.27, 1.16) * mm]});
            skLineSegment(sketch, "E1507", {"start": v(23.86, -0.58) * mm, "end": v(26.33, 0.56) * mm});
            skLineSegment(sketch, "E1508", {"start": v(26.33, 0.56) * mm, "end": v(26.2, 1.15) * mm});
            skFitSpline(sketch, "E1509", {"points": [v(-23.92, -0.57) * mm, v(-20.3, -2.25) * mm, v(-14.76, -5.06) * mm, v(-10.87, -7.19) * mm]});
            skFitSpline(sketch, "E1510", {"points": [v(-10.87, -7.19) * mm, v(-8.99, -8.21) * mm, v(-7.04, -9.18) * mm, v(-6.53, -9.34) * mm]});
            skFitSpline(sketch, "E1511", {"points": [v(-6.53, -9.34) * mm, v(-5.74, -9.59) * mm, v(-4.52, -9.79) * mm, v(-2.03, -10.07) * mm]});
            skFitSpline(sketch, "E1512", {"points": [v(-2.03, -10.07) * mm, v(-0.96, -10.2) * mm, v(3.03, -10) * mm, v(4.56, -9.75) * mm]});
            skLineSegment(sketch, "E1513", {"start": v(-26.27, 1.16) * mm, "end": v(-26.4, 0.58) * mm});
            skLineSegment(sketch, "E1514", {"start": v(-26.4, 0.58) * mm, "end": v(-23.92, -0.57) * mm});
            skFitSpline(sketch, "E1515", {"points": [v(-34.7, -3.96) * mm, v(-34.61, -3.75) * mm, v(-34.13, -1.92) * mm, v(-33.62, 0.1) * mm]});
            skFitSpline(sketch, "E1516", {"points": [v(-32.27, 39.65) * mm, v(-31.76, 40.25) * mm, v(-24.9, 43.74) * mm, v(-22.1, 44.82) * mm]});
            skFitSpline(sketch, "E1517", {"points": [v(-22.1, 44.82) * mm, v(-18.83, 46.08) * mm, v(-14.95, 47) * mm, v(-12.85, 47) * mm]});
            skFitSpline(sketch, "E1518", {"points": [v(-12.85, 47) * mm, v(-11.58, 47) * mm, v(-11.43, 46.77) * mm, v(-11.2, 44.49) * mm]});
            skFitSpline(sketch, "E1519", {"points": [v(-11.2, 44.49) * mm, v(-11.1, 43.53) * mm, v(-10.94, 42.58) * mm, v(-10.86, 42.37) * mm]});
            skLineSegment(sketch, "E1520", {"start": v(-33.62, 0.1) * mm, "end": v(-32.7, 3.8) * mm});
            skLineSegment(sketch, "E1521", {"start": v(-32.7, 3.8) * mm, "end": v(-32.7, 21.47) * mm});
            skLineSegment(sketch, "E1522", {"start": v(-32.7, 21.47) * mm, "end": v(-32.7, 39.14) * mm});
            skLineSegment(sketch, "E1523", {"start": v(-32.7, 39.14) * mm, "end": v(-32.27, 39.65) * mm});
            skFitSpline(sketch, "E1524", {"points": [v(-0.04, 42) * mm, v(9.94, 42) * mm, v(10.63, 42.02) * mm, v(10.77, 42.29) * mm]});
            skFitSpline(sketch, "E1525", {"points": [v(10.77, 42.29) * mm, v(10.86, 42.45) * mm, v(10.98, 43.18) * mm, v(11.04, 43.91) * mm]});
            skFitSpline(sketch, "E1526", {"points": [v(11.04, 43.91) * mm, v(11.2, 45.74) * mm, v(11.4, 46.53) * mm, v(11.74, 46.78) * mm]});
            skFitSpline(sketch, "E1527", {"points": [v(11.74, 46.78) * mm, v(12.64, 47.45) * mm, v(17.76, 46.47) * mm, v(22.03, 44.82) * mm]});
            skFitSpline(sketch, "E1528", {"points": [v(22.03, 44.82) * mm, v(24.84, 43.74) * mm, v(31.7, 40.25) * mm, v(32.2, 39.65) * mm]});
            skLineSegment(sketch, "E1529", {"start": v(-10.86, 42.37) * mm, "end": v(-10.7, 42) * mm});
            skLineSegment(sketch, "E1530", {"start": v(-10.7, 42) * mm, "end": v(-0.04, 42) * mm});
            skFitSpline(sketch, "E1531", {"points": [v(33.65, -0.09) * mm, v(34.72, -4.32) * mm, v(34.73, -4.33) * mm, v(34.98, -4.33) * mm]});
            skFitSpline(sketch, "E1532", {"points": [v(34.98, -4.33) * mm, v(35.43, -4.33) * mm, v(36.68, -0.45) * mm, v(37.3, 2.81) * mm]});
            skFitSpline(sketch, "E1533", {"points": [v(37.3, 2.81) * mm, v(39.06, 12.24) * mm, v(38.35, 19.35) * mm, v(35.35, 22.47) * mm]});
            skFitSpline(sketch, "E1534", {"points": [v(35.35, 22.47) * mm, v(34.94, 22.9) * mm, v(34.54, 23.36) * mm, v(34.46, 23.5) * mm]});
            skFitSpline(sketch, "E1535", {"points": [v(34.46, 23.5) * mm, v(34.39, 23.64) * mm, v(34.2, 28.4) * mm, v(34.05, 34.09) * mm]});
            skFitSpline(sketch, "E1536", {"points": [v(34.05, 34.09) * mm, v(33.75, 45.69) * mm, v(33.76, 45.57) * mm, v(32.46, 48.25) * mm]});
            skFitSpline(sketch, "E1537", {"points": [v(32.46, 48.25) * mm, v(28.9, 55.62) * mm, v(18.9, 60.87) * mm, v(5.55, 62.36) * mm]});
            skFitSpline(sketch, "E1538", {"points": [v(5.55, 62.36) * mm, v(3.19, 62.62) * mm, v(-3.26, 62.62) * mm, v(-5.62, 62.36) * mm]});
            skFitSpline(sketch, "E1539", {"points": [v(-5.62, 62.36) * mm, v(-12.08, 61.63) * mm, v(-17.4, 60.17) * mm, v(-22.1, 57.8) * mm]});
            skFitSpline(sketch, "E1540", {"points": [v(-22.1, 57.8) * mm, v(-27.11, 55.29) * mm, v(-30.65, 52.09) * mm, v(-32.46, 48.41) * mm]});
            skFitSpline(sketch, "E1541", {"points": [v(-32.46, 48.41) * mm, v(-33.8, 45.71) * mm, v(-33.81, 45.55) * mm, v(-34.1, 34.25) * mm]});
            skFitSpline(sketch, "E1542", {"points": [v(-34.1, 34.25) * mm, v(-34.25, 28.75) * mm, v(-34.37, 24.09) * mm, v(-34.37, 23.9) * mm]});
            skFitSpline(sketch, "E1543", {"points": [v(-34.37, 23.9) * mm, v(-34.36, 23.68) * mm, v(-34.73, 23.16) * mm, v(-35.26, 22.63) * mm]});
            skFitSpline(sketch, "E1544", {"points": [v(-35.26, 22.63) * mm, v(-37.98, 19.87) * mm, v(-38.9, 14.41) * mm, v(-37.96, 6.83) * mm]});
            skFitSpline(sketch, "E1545", {"points": [v(-37.96, 6.83) * mm, v(-37.38, 2.2) * mm, v(-36.64, -0.98) * mm, v(-35.51, -3.63) * mm]});
            skFitSpline(sketch, "E1546", {"points": [v(-35.51, -3.63) * mm, v(-35.17, -4.42) * mm, v(-34.93, -4.52) * mm, v(-34.7, -3.96) * mm]});
            skLineSegment(sketch, "E1547", {"start": v(32.2, 39.65) * mm, "end": v(32.63, 39.14) * mm});
            skLineSegment(sketch, "E1548", {"start": v(32.63, 39.14) * mm, "end": v(32.63, 21.52) * mm});
            skLineSegment(sketch, "E1549", {"start": v(32.63, 21.52) * mm, "end": v(32.63, 3.9) * mm});
            skLineSegment(sketch, "E1550", {"start": v(32.63, 3.9) * mm, "end": v(33.65, -0.09) * mm});
            skFitSpline(sketch, "E1551", {"points": [v(3.85, 14.4) * mm, v(5.94, 14.7) * mm, v(7.72, 15.02) * mm, v(7.8, 15.1) * mm]});
            skFitSpline(sketch, "E1552", {"points": [v(7.8, 15.1) * mm, v(8, 15.3) * mm, v(10.56, 39.02) * mm, v(10.42, 39.38) * mm]});
            skFitSpline(sketch, "E1553", {"points": [v(10.42, 39.38) * mm, v(10.32, 39.64) * mm, v(9.49, 39.66) * mm, v(-0.03, 39.66) * mm]});
            skFitSpline(sketch, "E1554", {"points": [v(-0.03, 39.66) * mm, v(-9.44, 39.66) * mm, v(-10.39, 39.64) * mm, v(-10.48, 39.4) * mm]});
            skFitSpline(sketch, "E1555", {"points": [v(-10.48, 39.4) * mm, v(-10.61, 39.04) * mm, v(-8.06, 15.3) * mm, v(-7.87, 15.1) * mm]});
            skFitSpline(sketch, "E1556", {"points": [v(-7.87, 15.1) * mm, v(-7.75, 14.98) * mm, v(-1.25, 13.91) * mm, v(-0.28, 13.85) * mm]});
            skFitSpline(sketch, "E1557", {"points": [v(-0.28, 13.85) * mm, v(-0.1, 13.84) * mm, v(1.76, 14.09) * mm, v(3.85, 14.4) * mm]});
            skFitSpline(sketch, "E1558", {"points": [v(-10.58, -64.87) * mm, v(-11.02, -64.84) * mm, v(-11.34, -64.75) * mm, v(-11.29, -64.68) * mm]});
            skFitSpline(sketch, "E1559", {"points": [v(-11.29, -64.68) * mm, v(-11.24, -64.6) * mm, v(-11.65, -64.49) * mm, v(-12.19, -64.43) * mm]});
            skFitSpline(sketch, "E1560", {"points": [v(-12.19, -64.43) * mm, v(-13.45, -64.29) * mm, v(-15.37, -63.75) * mm, v(-16.26, -63.3) * mm]});
            skFitSpline(sketch, "E1561", {"points": [v(-16.26, -63.3) * mm, v(-17.1, -62.87) * mm, v(-18.56, -61.4) * mm, v(-19.58, -59.97) * mm]});
            skFitSpline(sketch, "E1562", {"points": [v(-19.58, -59.97) * mm, v(-20.2, -59.09) * mm, v(-31.09, -42.02) * mm, v(-32.06, -40.4) * mm]});
            skFitSpline(sketch, "E1563", {"points": [v(-32.06, -40.4) * mm, v(-32.33, -39.94) * mm, v(-32.47, -38.63) * mm, v(-33.03, -30.8) * mm]});
            skFitSpline(sketch, "E1564", {"points": [v(-33.03, -30.8) * mm, v(-33.77, -20.68) * mm, v(-33.94, -18.75) * mm, v(-34.3, -16.58) * mm]});
            skFitSpline(sketch, "E1565", {"points": [v(-34.3, -16.58) * mm, v(-34.6, -14.74) * mm, v(-35.52, -11.17) * mm, v(-36.12, -9.5) * mm]});
            skFitSpline(sketch, "E1566", {"points": [v(-36.12, -9.5) * mm, v(-36.47, -8.55) * mm, v(-36.55, -8.09) * mm, v(-36.48, -7.47) * mm]});
            skFitSpline(sketch, "E1567", {"points": [v(-36.48, -7.47) * mm, v(-36.4, -6.76) * mm, v(-36.47, -6.49) * mm, v(-37.2, -4.96) * mm]});
            skFitSpline(sketch, "E1568", {"points": [v(-37.2, -4.96) * mm, v(-39.08, -1) * mm, v(-40.4, 6.03) * mm, v(-40.4, 12.17) * mm]});
            skFitSpline(sketch, "E1569", {"points": [v(-40.4, 12.17) * mm, v(-40.4, 15.47) * mm, v(-40.15, 17.36) * mm, v(-39.36, 19.72) * mm]});
            skFitSpline(sketch, "E1570", {"points": [v(-39.36, 19.72) * mm, v(-38.8, 21.4) * mm, v(-38.27, 22.35) * mm, v(-37.2, 23.66) * mm]});
            skFitSpline(sketch, "E1571", {"points": [v(-36.25, 33.75) * mm, v(-36.13, 38.79) * mm, v(-35.96, 43.6) * mm, v(-35.87, 44.43) * mm]});
            skFitSpline(sketch, "E1572", {"points": [v(-35.87, 44.43) * mm, v(-35.02, 52.13) * mm, v(-27.54, 59) * mm, v(-16.32, 62.4) * mm]});
            skFitSpline(sketch, "E1573", {"points": [v(-16.32, 62.4) * mm, v(-12.9, 63.43) * mm, v(-7.34, 64.48) * mm, v(-5.2, 64.5) * mm]});
            skFitSpline(sketch, "E1574", {"points": [v(-5.2, 64.5) * mm, v(-4.74, 64.5) * mm, v(-4.53, 64.55) * mm, v(-4.67, 64.64) * mm]});
            skFitSpline(sketch, "E1575", {"points": [v(-4.67, 64.64) * mm, v(-5, 64.85) * mm, v(-0.33, 65.02) * mm, v(2.4, 64.9) * mm]});
            skFitSpline(sketch, "E1576", {"points": [v(2.4, 64.9) * mm, v(3.79, 64.83) * mm, v(4.73, 64.72) * mm, v(4.6, 64.64) * mm]});
            skFitSpline(sketch, "E1577", {"points": [v(4.6, 64.64) * mm, v(4.47, 64.55) * mm, v(4.67, 64.5) * mm, v(5.13, 64.5) * mm]});
            skFitSpline(sketch, "E1578", {"points": [v(5.13, 64.5) * mm, v(6.27, 64.49) * mm, v(10.21, 63.9) * mm, v(12.42, 63.4) * mm]});
            skFitSpline(sketch, "E1579", {"points": [v(12.42, 63.4) * mm, v(23.87, 60.84) * mm, v(32.07, 55.22) * mm, v(34.95, 47.95) * mm]});
            skFitSpline(sketch, "E1580", {"points": [v(34.95, 47.95) * mm, v(35.83, 45.74) * mm, v(35.94, 44.46) * mm, v(36.19, 34.03) * mm]});
            skLineSegment(sketch, "E1581", {"start": v(-37.2, 23.66) * mm, "end": v(-36.46, 24.58) * mm});
            skLineSegment(sketch, "E1582", {"start": v(-36.46, 24.58) * mm, "end": v(-36.25, 33.75) * mm});
            skFitSpline(sketch, "E1583", {"points": [v(36.92, 23.95) * mm, v(39.15, 21.6) * mm, v(40.35, 17.5) * mm, v(40.35, 12.25) * mm]});
            skFitSpline(sketch, "E1584", {"points": [v(40.35, 12.25) * mm, v(40.35, 6.04) * mm, v(39.05, -0.92) * mm, v(37.13, -4.96) * mm]});
            skFitSpline(sketch, "E1585", {"points": [v(37.13, -4.96) * mm, v(36.4, -6.48) * mm, v(36.33, -6.76) * mm, v(36.4, -7.46) * mm]});
            skFitSpline(sketch, "E1586", {"points": [v(36.4, -7.46) * mm, v(36.48, -8.09) * mm, v(36.38, -8.61) * mm, v(35.91, -10) * mm]});
            skFitSpline(sketch, "E1587", {"points": [v(35.91, -10) * mm, v(34.2, -15.1) * mm, v(34.02, -16.46) * mm, v(32.9, -32.02) * mm]});
            skFitSpline(sketch, "E1588", {"points": [v(32.9, -32.02) * mm, v(32.51, -37.23) * mm, v(32.25, -39.93) * mm, v(32.1, -40.21) * mm]});
            skFitSpline(sketch, "E1589", {"points": [v(32.1, -40.21) * mm, v(31.4, -41.53) * mm, v(20.03, -59.26) * mm, v(19.13, -60.46) * mm]});
            skFitSpline(sketch, "E1590", {"points": [v(19.13, -60.46) * mm, v(17.23, -62.98) * mm, v(15.94, -63.76) * mm, v(12.72, -64.34) * mm]});
            skFitSpline(sketch, "E1591", {"points": [v(12.72, -64.34) * mm, v(11.8, -64.4) * mm, v(11.1, -64.47) * mm, v(11.2, -64.5) * mm]});
            skFitSpline(sketch, "E1592", {"points": [v(11.13, -64.14) * mm, v(12.23, -64.36) * mm, v(-7.77, -64.96) * mm, v(-10.66, -64.8) * mm]});
            skLineSegment(sketch, "E1593", {"start": v(36.19, 34.03) * mm, "end": v(36.41, 24.48) * mm});
            skLineSegment(sketch, "E1594", {"start": v(36.41, 24.48) * mm, "end": v(36.92, 23.95) * mm});
            skFitSpline(sketch, "E1595", {"points": [v(12.13, -62.44) * mm, v(15.15, -61.85) * mm, v(15.9, -61.41) * mm, v(17.5, -59.3) * mm]});
            skFitSpline(sketch, "E1596", {"points": [v(17.5, -59.3) * mm, v(18.02, -58.63) * mm, v(21.12, -53.85) * mm, v(24.4, -48.68) * mm]});
            skFitSpline(sketch, "E1597", {"points": [v(30.99, -30.68) * mm, v(31.34, -25.95) * mm, v(31.62, -21.69) * mm, v(31.63, -21.2) * mm]});
            skFitSpline(sketch, "E1598", {"points": [v(31.63, -21.2) * mm, v(31.63, -19.96) * mm, v(31.29, -20.07) * mm, v(30.52, -21.54) * mm]});
            skFitSpline(sketch, "E1599", {"points": [v(30.52, -21.54) * mm, v(30.17, -22.2) * mm, v(29.03, -23.95) * mm, v(27.98, -25.4) * mm]});
            skFitSpline(sketch, "E1600", {"points": [v(27.98, -25.4) * mm, v(25.03, -29.53) * mm, v(24.05, -31.1) * mm, v(22.72, -33.86) * mm]});
            skFitSpline(sketch, "E1601", {"points": [v(22.72, -33.86) * mm, v(21.37, -36.67) * mm, v(19.8, -40.74) * mm, v(19.8, -41.46) * mm]});
            skFitSpline(sketch, "E1602", {"points": [v(19.8, -41.46) * mm, v(19.8, -41.7) * mm, v(20, -43.06) * mm, v(20.25, -44.46) * mm]});
            skLineSegment(sketch, "E1603", {"start": v(24.4, -48.68) * mm, "end": v(30.35, -39.27) * mm});
            skLineSegment(sketch, "E1604", {"start": v(30.35, -39.27) * mm, "end": v(30.99, -30.68) * mm});
            skFitSpline(sketch, "E1605", {"points": [v(20.37, -47.96) * mm, v(19.84, -49.53) * mm, v(17.38, -54.36) * mm, v(16.73, -55.11) * mm]});
            skFitSpline(sketch, "E1606", {"points": [v(16.73, -55.11) * mm, v(16.4, -55.5) * mm, v(15.86, -55.9) * mm, v(15.52, -56) * mm]});
            skFitSpline(sketch, "E1607", {"points": [v(15.52, -56) * mm, v(14.6, -56.31) * mm, v(12.77, -56.1) * mm, v(11.07, -55.5) * mm]});
            skFitSpline(sketch, "E1608", {"points": [v(11.07, -55.5) * mm, v(9.85, -55.06) * mm, v(9.55, -55.01) * mm, v(9.38, -55.2) * mm]});
            skFitSpline(sketch, "E1609", {"points": [v(9.38, -55.2) * mm, v(9.27, -55.31) * mm, v(8.97, -56.05) * mm, v(8.71, -56.83) * mm]});
            skFitSpline(sketch, "E1610", {"points": [v(8.71, -56.83) * mm, v(8.46, -57.6) * mm, v(8.14, -58.38) * mm, v(8, -58.54) * mm]});
            skFitSpline(sketch, "E1611", {"points": [v(8, -58.54) * mm, v(7.77, -58.8) * mm, v(7.17, -58.83) * mm, v(-0.03, -58.83) * mm]});
            skFitSpline(sketch, "E1612", {"points": [v(-0.03, -58.83) * mm, v(-7.24, -58.83) * mm, v(-7.83, -58.8) * mm, v(-8.07, -58.54) * mm]});
            skFitSpline(sketch, "E1613", {"points": [v(-8.07, -58.54) * mm, v(-8.2, -58.38) * mm, v(-8.53, -57.6) * mm, v(-8.78, -56.83) * mm]});
            skFitSpline(sketch, "E1614", {"points": [v(-8.78, -56.83) * mm, v(-9.03, -56.05) * mm, v(-9.33, -55.31) * mm, v(-9.45, -55.2) * mm]});
            skFitSpline(sketch, "E1615", {"points": [v(-9.45, -55.2) * mm, v(-9.62, -55.01) * mm, v(-9.91, -55.06) * mm, v(-11.13, -55.5) * mm]});
            skFitSpline(sketch, "E1616", {"points": [v(-11.13, -55.5) * mm, v(-12.84, -56.1) * mm, v(-14.66, -56.31) * mm, v(-15.59, -56) * mm]});
            skFitSpline(sketch, "E1617", {"points": [v(-15.59, -56) * mm, v(-15.92, -55.9) * mm, v(-16.45, -55.5) * mm, v(-16.76, -55.15) * mm]});
            skFitSpline(sketch, "E1618", {"points": [v(-16.76, -55.15) * mm, v(-17.4, -54.39) * mm, v(-19, -51.34) * mm, v(-20.03, -48.93) * mm]});
            skFitSpline(sketch, "E1619", {"points": [v(-20.03, -48.93) * mm, v(-20.81, -47.08) * mm, v(-20.8, -47.3) * mm, v(-20.2, -43.8) * mm]});
            skFitSpline(sketch, "E1620", {"points": [v(-20.2, -43.8) * mm, v(-19.72, -41.12) * mm, v(-19.7, -41.21) * mm, v(-21.13, -37.62) * mm]});
            skFitSpline(sketch, "E1621", {"points": [v(-21.13, -37.62) * mm, v(-22.77, -33.48) * mm, v(-24.24, -30.67) * mm, v(-25.87, -28.58) * mm]});
            skFitSpline(sketch, "E1622", {"points": [v(-25.87, -28.58) * mm, v(-26.3, -28.03) * mm, v(-27.12, -26.87) * mm, v(-27.7, -26) * mm]});
            skFitSpline(sketch, "E1623", {"points": [v(-27.7, -26) * mm, v(-28.28, -25.13) * mm, v(-29.04, -24) * mm, v(-29.39, -23.48) * mm]});
            skFitSpline(sketch, "E1624", {"points": [v(-29.39, -23.48) * mm, v(-29.73, -22.96) * mm, v(-30.29, -22.04) * mm, v(-30.62, -21.44) * mm]});
            skFitSpline(sketch, "E1625", {"points": [v(-30.62, -21.44) * mm, v(-30.97, -20.8) * mm, v(-31.34, -20.33) * mm, v(-31.49, -20.33) * mm]});
            skFitSpline(sketch, "E1626", {"points": [v(-31.49, -20.33) * mm, v(-31.8, -20.33) * mm, v(-31.8, -20.41) * mm, v(-30.97, -31.67) * mm]});
            skLineSegment(sketch, "E1627", {"start": v(20.25, -44.46) * mm, "end": v(20.7, -47) * mm});
            skLineSegment(sketch, "E1628", {"start": v(20.7, -47) * mm, "end": v(20.37, -47.96) * mm});
            skFitSpline(sketch, "E1629", {"points": [v(-24.23, -49) * mm, v(-20.83, -54.36) * mm, v(-17.63, -59.25) * mm, v(-17.12, -59.87) * mm]});
            skFitSpline(sketch, "E1630", {"points": [v(-17.12, -59.87) * mm, v(-15.95, -61.29) * mm, v(-14.94, -61.88) * mm, v(-13.06, -62.24) * mm]});
            skFitSpline(sketch, "E1631", {"points": [v(-13.06, -62.24) * mm, v(-10.38, -62.76) * mm, v(-9.3, -62.8) * mm, v(0.72, -62.75) * mm]});
            skFitSpline(sketch, "E1632", {"points": [v(0.72, -62.75) * mm, v(9.2, -62.72) * mm, v(10.93, -62.67) * mm, v(12.13, -62.44) * mm]});
            skLineSegment(sketch, "E1633", {"start": v(-30.97, -31.67) * mm, "end": v(-30.4, -39.27) * mm});
            skLineSegment(sketch, "E1634", {"start": v(-30.4, -39.27) * mm, "end": v(-24.23, -49) * mm});
            skFitSpline(sketch, "E1635", {"points": [v(6.77, -56.27) * mm, v(6.9, -56) * mm, v(7.04, -55.5) * mm, v(7.1, -55.14) * mm]});
            skFitSpline(sketch, "E1636", {"points": [v(0.07, -54.5) * mm, v(-6.25, -54.5) * mm, v(-7.05, -54.53) * mm, v(-7.14, -54.76) * mm]});
            skFitSpline(sketch, "E1637", {"points": [v(-7.14, -54.76) * mm, v(-7.25, -55.05) * mm, v(-6.93, -56.3) * mm, v(-6.66, -56.62) * mm]});
            skFitSpline(sketch, "E1638", {"points": [v(-6.66, -56.62) * mm, v(-6.53, -56.79) * mm, v(-5.06, -56.82) * mm, v(0.03, -56.8) * mm]});
            skLineSegment(sketch, "E1639", {"start": v(7.1, -55.14) * mm, "end": v(7.18, -54.5) * mm});
            skLineSegment(sketch, "E1640", {"start": v(7.18, -54.5) * mm, "end": v(0.07, -54.5) * mm});
            skFitSpline(sketch, "E1641", {"points": [v(-11.95, -53.65) * mm, v(-9.75, -52.92) * mm, v(-9.76, -52.94) * mm, v(-10.34, -50.82) * mm]});
            skFitSpline(sketch, "E1642", {"points": [v(-10.34, -50.82) * mm, v(-10.6, -49.86) * mm, v(-10.91, -48.73) * mm, v(-11.03, -48.3) * mm]});
            skFitSpline(sketch, "E1643", {"points": [v(-11.03, -48.3) * mm, v(-11.39, -46.96) * mm, v(-11.54, -46.96) * mm, v(-12.94, -48.3) * mm]});
            skFitSpline(sketch, "E1644", {"points": [v(-12.94, -48.3) * mm, v(-14.72, -50.03) * mm, v(-14.84, -50) * mm, v(-16.53, -47.09) * mm]});
            skFitSpline(sketch, "E1645", {"points": [v(-16.53, -47.09) * mm, v(-18.03, -44.5) * mm, v(-18.32, -44.38) * mm, v(-18.6, -46.25) * mm]});
            skFitSpline(sketch, "E1646", {"points": [v(-18.6, -46.25) * mm, v(-18.7, -46.8) * mm, v(-18.6, -47.2) * mm, v(-18.02, -48.5) * mm]});
            skFitSpline(sketch, "E1647", {"points": [v(-18.02, -48.5) * mm, v(-17.16, -50.48) * mm, v(-15.78, -53.18) * mm, v(-15.34, -53.74) * mm]});
            skFitSpline(sketch, "E1648", {"points": [v(-15.34, -53.74) * mm, v(-14.88, -54.33) * mm, v(-13.92, -54.3) * mm, v(-11.95, -53.65) * mm]});
            skLineSegment(sketch, "E1649", {"start": v(0.03, -56.8) * mm, "end": v(6.55, -56.75) * mm});
            skLineSegment(sketch, "E1650", {"start": v(6.55, -56.75) * mm, "end": v(6.77, -56.27) * mm});
            skFitSpline(sketch, "E1651", {"points": [v(15.36, -53.62) * mm, v(15.84, -52.98) * mm, v(17.37, -49.94) * mm, v(18.12, -48.14) * mm]});
            skFitSpline(sketch, "E1652", {"points": [v(18.12, -48.14) * mm, v(18.54, -47.13) * mm, v(18.63, -46.72) * mm, v(18.54, -46.22) * mm]});
            skFitSpline(sketch, "E1653", {"points": [v(18.54, -46.22) * mm, v(18.24, -44.4) * mm, v(17.98, -44.52) * mm, v(16.48, -47.08) * mm]});
            skFitSpline(sketch, "E1654", {"points": [v(16.48, -47.08) * mm, v(14.79, -49.99) * mm, v(14.65, -50.04) * mm, v(12.86, -48.3) * mm]});
            skFitSpline(sketch, "E1655", {"points": [v(12.86, -48.3) * mm, v(11.8, -47.27) * mm, v(11.6, -47.13) * mm, v(11.4, -47.34) * mm]});
            skFitSpline(sketch, "E1656", {"points": [v(11.4, -47.34) * mm, v(11.15, -47.6) * mm, v(9.97, -51.8) * mm, v(9.97, -52.41) * mm]});
            skFitSpline(sketch, "E1657", {"points": [v(9.97, -52.41) * mm, v(9.97, -52.62) * mm, v(10.06, -52.87) * mm, v(10.18, -52.97) * mm]});
            skFitSpline(sketch, "E1658", {"points": [v(10.18, -52.97) * mm, v(10.6, -53.32) * mm, v(13.4, -54.16) * mm, v(14.17, -54.16) * mm]});
            skFitSpline(sketch, "E1659", {"points": [v(14.17, -54.16) * mm, v(14.86, -54.16) * mm, v(15, -54.1) * mm, v(15.36, -53.62) * mm]});
            skFitSpline(sketch, "E1660", {"points": [v(7.73, -52.3) * mm, v(7.91, -52.1) * mm, v(9.29, -46.98) * mm, v(9.3, -46.46) * mm]});
            skFitSpline(sketch, "E1661", {"points": [v(-9.37, -46.41) * mm, v(-9.37, -46.78) * mm, v(-8.82, -48.95) * mm, v(-8.1, -51.45) * mm]});
            skFitSpline(sketch, "E1662", {"points": [v(-8.1, -51.45) * mm, v(-7.95, -51.97) * mm, v(-7.74, -52.34) * mm, v(-7.57, -52.39) * mm]});
            skFitSpline(sketch, "E1663", {"points": [v(-7.57, -52.39) * mm, v(-7.1, -52.51) * mm, v(7.6, -52.42) * mm, v(7.73, -52.3) * mm]});
            skLineSegment(sketch, "E1664", {"start": v(9.3, -46.46) * mm, "end": v(9.3, -46) * mm});
            skLineSegment(sketch, "E1665", {"start": v(9.3, -46) * mm, "end": v(-0.03, -46) * mm});
            skLineSegment(sketch, "E1666", {"start": v(-0.03, -46) * mm, "end": v(-9.37, -46) * mm});
            skLineSegment(sketch, "E1667", {"start": v(-9.37, -46) * mm, "end": v(-9.37, -46.41) * mm});
            skFitSpline(sketch, "E1668", {"points": [v(-13.14, -45.67) * mm, v(-12.71, -45.22) * mm, v(-12.37, -44.7) * mm, v(-12.37, -44.53) * mm]});
            skFitSpline(sketch, "E1669", {"points": [v(-12.37, -44.53) * mm, v(-12.37, -44.09) * mm, v(-13.85, -41.67) * mm, v(-14.93, -40.36) * mm]});
            skFitSpline(sketch, "E1670", {"points": [v(-14.93, -40.36) * mm, v(-16.44, -38.53) * mm, v(-18.8, -36.27) * mm, v(-19.1, -36.38) * mm]});
            skFitSpline(sketch, "E1671", {"points": [v(-19.1, -36.38) * mm, v(-19.31, -36.47) * mm, v(-19.23, -36.84) * mm, v(-18.54, -38.8) * mm]});
            skFitSpline(sketch, "E1672", {"points": [v(-18.54, -38.8) * mm, v(-17.81, -40.86) * mm, v(-16.52, -43.38) * mm, v(-14.76, -46.12) * mm]});
            skFitSpline(sketch, "E1673", {"points": [v(-14.76, -46.12) * mm, v(-14.4, -46.7) * mm, v(-13.99, -46.58) * mm, v(-13.14, -45.67) * mm]});
            skFitSpline(sketch, "E1674", {"points": [v(16.03, -43.91) * mm, v(17.15, -42.04) * mm, v(17.74, -40.8) * mm, v(18.4, -39) * mm]});
            skFitSpline(sketch, "E1675", {"points": [v(18.4, -39) * mm, v(18.9, -37.67) * mm, v(19.3, -36.49) * mm, v(19.3, -36.37) * mm]});
            skFitSpline(sketch, "E1676", {"points": [v(19.3, -36.37) * mm, v(19.3, -36.26) * mm, v(19.17, -36.17) * mm, v(19, -36.17) * mm]});
            skFitSpline(sketch, "E1677", {"points": [v(19, -36.17) * mm, v(18.7, -36.17) * mm, v(15.25, -39.81) * mm, v(14.08, -41.39) * mm]});
            skFitSpline(sketch, "E1678", {"points": [v(14.08, -41.39) * mm, v(13.36, -42.35) * mm, v(12.3, -44.3) * mm, v(12.3, -44.66) * mm]});
            skFitSpline(sketch, "E1679", {"points": [v(12.3, -44.66) * mm, v(12.3, -44.76) * mm, v(12.65, -45.22) * mm, v(13.08, -45.68) * mm]});
            skFitSpline(sketch, "E1680", {"points": [v(13.08, -45.68) * mm, v(13.6, -46.24) * mm, v(13.97, -46.5) * mm, v(14.2, -46.46) * mm]});
            skFitSpline(sketch, "E1681", {"points": [v(14.2, -46.46) * mm, v(14.44, -46.43) * mm, v(14.98, -45.68) * mm, v(16.03, -43.91) * mm]});
            skFitSpline(sketch, "E1682", {"points": [v(10.14, -43.83) * mm, v(10.32, -43.73) * mm, v(10.7, -43.19) * mm, v(11, -42.62) * mm]});
            skFitSpline(sketch, "E1683", {"points": [v(11, -42.62) * mm, v(12.1, -40.4) * mm, v(12.82, -39.53) * mm, v(17.97, -34.08) * mm]});
            skFitSpline(sketch, "E1684", {"points": [v(17.97, -34.08) * mm, v(22.2, -29.62) * mm, v(23.33, -28.32) * mm, v(24.95, -26.17) * mm]});
            skFitSpline(sketch, "E1685", {"points": [v(24.95, -26.17) * mm, v(27.01, -23.43) * mm, v(27.53, -21.96) * mm, v(27.8, -18.17) * mm]});
            skFitSpline(sketch, "E1686", {"points": [v(27.8, -18.17) * mm, v(27.9, -16.84) * mm, v(28.05, -14.6) * mm, v(28.15, -13.2) * mm]});
            skFitSpline(sketch, "E1687", {"points": [v(28.15, -13.2) * mm, v(28.24, -11.8) * mm, v(28.36, -10.4) * mm, v(28.4, -10.12) * mm]});
            skFitSpline(sketch, "E1688", {"points": [v(28.4, -10.12) * mm, v(28.46, -9.78) * mm, v(28.4, -9.46) * mm, v(28.24, -9.25) * mm]});
            skFitSpline(sketch, "E1689", {"points": [v(28.24, -9.25) * mm, v(27.99, -8.93) * mm, v(27.96, -8.94) * mm, v(27.2, -9.8) * mm]});
            skFitSpline(sketch, "E1690", {"points": [v(27.2, -9.8) * mm, v(25.78, -11.41) * mm, v(23.07, -13.03) * mm, v(20.35, -13.89) * mm]});
            skFitSpline(sketch, "E1691", {"points": [v(20.35, -13.89) * mm, v(19.12, -14.28) * mm, v(13.53, -15.47) * mm, v(11.6, -15.75) * mm]});
            skFitSpline(sketch, "E1692", {"points": [v(11.6, -15.75) * mm, v(11.16, -15.82) * mm, v(10.63, -15.83) * mm, v(10.41, -15.77) * mm]});
            skFitSpline(sketch, "E1693", {"points": [v(10.41, -15.77) * mm, v(9.91, -15.65) * mm, v(8.2, -13.53) * mm, v(7.68, -12.37) * mm]});
            skFitSpline(sketch, "E1694", {"points": [v(7.68, -12.37) * mm, v(7.22, -11.38) * mm, v(7.23, -11.38) * mm, v(5.47, -11.79) * mm]});
            skFitSpline(sketch, "E1695", {"points": [v(5.47, -11.79) * mm, v(3.66, -12.2) * mm, v(-3.72, -12.2) * mm, v(-5.53, -11.79) * mm]});
            skFitSpline(sketch, "E1696", {"points": [v(-5.53, -11.79) * mm, v(-6.22, -11.63) * mm, v(-6.9, -11.5) * mm, v(-7.04, -11.5) * mm]});
            skFitSpline(sketch, "E1697", {"points": [v(-7.04, -11.5) * mm, v(-7.18, -11.5) * mm, v(-7.49, -11.88) * mm, v(-7.73, -12.37) * mm]});
            skFitSpline(sketch, "E1698", {"points": [v(-7.73, -12.37) * mm, v(-8.36, -13.65) * mm, v(-9.97, -15.64) * mm, v(-10.48, -15.77) * mm]});
            skFitSpline(sketch, "E1699", {"points": [v(-10.48, -15.77) * mm, v(-10.71, -15.83) * mm, v(-11.44, -15.79) * mm, v(-12.1, -15.67) * mm]});
            skFitSpline(sketch, "E1700", {"points": [v(-12.1, -15.67) * mm, v(-15.13, -15.15) * mm, v(-19.2, -14.27) * mm, v(-20.43, -13.89) * mm]});
            skFitSpline(sketch, "E1701", {"points": [v(-20.43, -13.89) * mm, v(-23.14, -13.03) * mm, v(-26, -11.31) * mm, v(-27.3, -9.77) * mm]});
            skFitSpline(sketch, "E1702", {"points": [v(-27.3, -9.77) * mm, v(-27.65, -9.35) * mm, v(-28, -9) * mm, v(-28.06, -9) * mm]});
            skFitSpline(sketch, "E1703", {"points": [v(-28.06, -9) * mm, v(-28.47, -9) * mm, v(-28.52, -9.74) * mm, v(-28.3, -11.95) * mm]});
            skFitSpline(sketch, "E1704", {"points": [v(-28.3, -11.95) * mm, v(-28.16, -13.22) * mm, v(-28.01, -15.33) * mm, v(-27.96, -16.66) * mm]});
            skFitSpline(sketch, "E1705", {"points": [v(-27.96, -16.66) * mm, v(-27.76, -21.46) * mm, v(-27.3, -22.95) * mm, v(-25, -26.22) * mm]});
            skFitSpline(sketch, "E1706", {"points": [v(-25, -26.22) * mm, v(-22.92, -29.22) * mm, v(-22.55, -29.63) * mm, v(-17.67, -34.6) * mm]});
            skFitSpline(sketch, "E1707", {"points": [v(-17.67, -34.6) * mm, v(-13.37, -39) * mm, v(-12.15, -40.47) * mm, v(-11.1, -42.55) * mm]});
            skFitSpline(sketch, "E1708", {"points": [v(-11.1, -42.55) * mm, v(-10.76, -43.22) * mm, v(-10.37, -43.74) * mm, v(-10.15, -43.83) * mm]});
            skFitSpline(sketch, "E1709", {"points": [v(-10.15, -43.83) * mm, v(-9.61, -44.04) * mm, v(9.74, -44.04) * mm, v(10.14, -43.83) * mm]});
            skFitSpline(sketch, "E1710", {"points": [v(-30.03, -15.7) * mm, v(-30.04, -14.9) * mm, v(-30.14, -13.28) * mm, v(-30.27, -12.1) * mm]});
            skFitSpline(sketch, "E1711", {"points": [v(-30.27, -12.1) * mm, v(-30.63, -8.67) * mm, v(-30.28, -5.52) * mm, v(-28.98, -0.58) * mm]});
            skFitSpline(sketch, "E1712", {"points": [v(-28.23, 9.75) * mm, v(-28.17, 18.88) * mm, v(-28.35, 21.3) * mm, v(-29.51, 27.08) * mm]});
            skFitSpline(sketch, "E1713", {"points": [v(-29.51, 27.08) * mm, v(-29.86, 28.8) * mm, v(-30, 29.26) * mm, v(-30.24, 29.3) * mm]});
            skFitSpline(sketch, "E1714", {"points": [v(-30.24, 29.3) * mm, v(-30.52, 29.35) * mm, v(-30.53, 28.66) * mm, v(-30.53, 16.64) * mm]});
            skLineSegment(sketch, "E1715", {"start": v(-28.98, -0.58) * mm, "end": v(-28.28, 2.08) * mm});
            skLineSegment(sketch, "E1716", {"start": v(-28.28, 2.08) * mm, "end": v(-28.23, 9.75) * mm});
            skFitSpline(sketch, "E1717", {"points": [v(-32.62, -12.67) * mm, v(-30.88, -16.56) * mm, v(-30.57, -17.17) * mm, v(-30.28, -17.17) * mm]});
            skFitSpline(sketch, "E1718", {"points": [v(-30.28, -17.17) * mm, v(-30.08, -17.17) * mm, v(-30.03, -16.89) * mm, v(-30.03, -15.7) * mm]});
            skLineSegment(sketch, "E1719", {"start": v(-30.53, 16.64) * mm, "end": v(-30.52, 3.92) * mm});
            skLineSegment(sketch, "E1720", {"start": v(-30.52, 3.92) * mm, "end": v(-32.22, -2.92) * mm});
            skLineSegment(sketch, "E1721", {"start": v(-32.22, -2.92) * mm, "end": v(-33.92, -9.75) * mm});
            skLineSegment(sketch, "E1722", {"start": v(-33.92, -9.75) * mm, "end": v(-32.62, -12.67) * mm});
            skFitSpline(sketch, "E1723", {"points": [v(31.03, -16.04) * mm, v(31.82, -14.45) * mm, v(33.8, -9.92) * mm, v(33.8, -9.68) * mm]});
            skFitSpline(sketch, "E1724", {"points": [v(33.8, -9.68) * mm, v(33.8, -9.57) * mm, v(33.05, -6.48) * mm, v(32.13, -2.82) * mm]});
            skFitSpline(sketch, "E1725", {"points": [v(30.47, 16.6) * mm, v(30.47, 27.5) * mm, v(30.43, 29.33) * mm, v(30.23, 29.33) * mm]});
            skFitSpline(sketch, "E1726", {"points": [v(30.23, 29.33) * mm, v(29.91, 29.33) * mm, v(29.72, 28.68) * mm, v(29.22, 25.91) * mm]});
            skFitSpline(sketch, "E1727", {"points": [v(29.22, 25.91) * mm, v(28.28, 20.7) * mm, v(28.25, 20.28) * mm, v(28.18, 11.17) * mm]});
            skLineSegment(sketch, "E1728", {"start": v(32.13, -2.82) * mm, "end": v(30.47, 3.85) * mm});
            skLineSegment(sketch, "E1729", {"start": v(30.47, 3.85) * mm, "end": v(30.47, 16.6) * mm});
            skFitSpline(sketch, "E1730", {"points": [v(28.71, 0.42) * mm, v(29.46, -2.3) * mm, v(30.08, -5.63) * mm, v(30.3, -8.08) * mm]});
            skFitSpline(sketch, "E1731", {"points": [v(30.3, -8.08) * mm, v(30.43, -9.55) * mm, v(30.4, -10.5) * mm, v(30.21, -12.34) * mm]});
            skFitSpline(sketch, "E1732", {"points": [v(30.21, -12.34) * mm, v(29.95, -14.84) * mm, v(29.9, -16.87) * mm, v(30.08, -17.06) * mm]});
            skFitSpline(sketch, "E1733", {"points": [v(30.08, -17.06) * mm, v(30.32, -17.3) * mm, v(30.48, -17.12) * mm, v(31.03, -16.04) * mm]});
            skLineSegment(sketch, "E1734", {"start": v(28.18, 11.17) * mm, "end": v(28.11, 2.58) * mm});
            skLineSegment(sketch, "E1735", {"start": v(28.11, 2.58) * mm, "end": v(28.71, 0.42) * mm});
            skFitSpline(sketch, "E1736", {"points": [v(-10.48, -12.96) * mm, v(-9.73, -12.03) * mm, v(-9.33, -11.23) * mm, v(-9.4, -10.78) * mm]});
            skFitSpline(sketch, "E1737", {"points": [v(-9.4, -10.78) * mm, v(-9.45, -10.38) * mm, v(-10.4, -9.83) * mm, v(-16.06, -6.82) * mm]});
            skFitSpline(sketch, "E1738", {"points": [v(-16.06, -6.82) * mm, v(-19.45, -5.02) * mm, v(-26.1, -1.83) * mm, v(-26.46, -1.83) * mm]});
            skFitSpline(sketch, "E1739", {"points": [v(-26.46, -1.83) * mm, v(-26.87, -1.83) * mm, v(-27.03, -2.46) * mm, v(-27.03, -4.13) * mm]});
            skFitSpline(sketch, "E1740", {"points": [v(-27.03, -4.13) * mm, v(-27.03, -6.03) * mm, v(-26.76, -7.14) * mm, v(-26.03, -8.14) * mm]});
            skFitSpline(sketch, "E1741", {"points": [v(-26.03, -8.14) * mm, v(-25.06, -9.48) * mm, v(-22.73, -10.98) * mm, v(-20.27, -11.85) * mm]});
            skFitSpline(sketch, "E1742", {"points": [v(-20.27, -11.85) * mm, v(-19.08, -12.27) * mm, v(-12.53, -13.65) * mm, v(-11.67, -13.66) * mm]});
            skFitSpline(sketch, "E1743", {"points": [v(-11.67, -13.66) * mm, v(-11.14, -13.67) * mm, v(-10.97, -13.56) * mm, v(-10.48, -12.96) * mm]});
            skFitSpline(sketch, "E1744", {"points": [v(15.47, -12.98) * mm, v(17.35, -12.6) * mm, v(19.58, -12.05) * mm, v(20.44, -11.74) * mm]});
            skFitSpline(sketch, "E1745", {"points": [v(20.44, -11.74) * mm, v(23.3, -10.72) * mm, v(25.57, -9.08) * mm, v(26.43, -7.42) * mm]});
            skFitSpline(sketch, "E1746", {"points": [v(26.43, -7.42) * mm, v(26.82, -6.68) * mm, v(26.88, -6.34) * mm, v(26.93, -4.56) * mm]});
            skFitSpline(sketch, "E1747", {"points": [v(26.93, -4.56) * mm, v(27, -2.51) * mm, v(26.86, -1.83) * mm, v(26.4, -1.83) * mm]});
            skFitSpline(sketch, "E1748", {"points": [v(26.4, -1.83) * mm, v(25.98, -1.83) * mm, v(18.93, -5.25) * mm, v(14.88, -7.42) * mm]});
            skFitSpline(sketch, "E1749", {"points": [v(14.88, -7.42) * mm, v(9.57, -10.26) * mm, v(9.4, -10.37) * mm, v(9.33, -10.8) * mm]});
            skFitSpline(sketch, "E1750", {"points": [v(9.33, -10.8) * mm, v(9.27, -11.2) * mm, v(9.85, -12.3) * mm, v(10.56, -13.15) * mm]});
            skFitSpline(sketch, "E1751", {"points": [v(10.56, -13.15) * mm, v(11.13, -13.82) * mm, v(11.3, -13.82) * mm, v(15.47, -12.98) * mm]});
            skFitSpline(sketch, "E1752", {"points": [v(5.05, -9.83) * mm, v(6.77, -9.44) * mm, v(7.62, -9.07) * mm, v(11.04, -7.2) * mm]});
            skFitSpline(sketch, "E1753", {"points": [v(11.04, -7.2) * mm, v(15.4, -4.83) * mm, v(19.14, -2.93) * mm, v(23.23, -1.01) * mm]});
            skFitSpline(sketch, "E1754", {"points": [v(26.32, 1.02) * mm, v(26.15, 2.72) * mm, v(26.13, 17.46) * mm, v(26.3, 19.33) * mm]});
            skFitSpline(sketch, "E1755", {"points": [v(26.3, 19.33) * mm, v(26.75, 24.23) * mm, v(27.88, 30.14) * mm, v(29.4, 35.46) * mm]});
            skFitSpline(sketch, "E1756", {"points": [v(29.4, 35.46) * mm, v(29.98, 37.48) * mm, v(30.14, 38.28) * mm, v(30.02, 38.48) * mm]});
            skFitSpline(sketch, "E1757", {"points": [v(30.02, 38.48) * mm, v(29.8, 38.82) * mm, v(24.33, 41.57) * mm, v(21.68, 42.66) * mm]});
            skFitSpline(sketch, "E1758", {"points": [v(21.68, 42.66) * mm, v(19.67, 43.5) * mm, v(16.06, 44.52) * mm, v(14.34, 44.74) * mm]});
            skFitSpline(sketch, "E1759", {"points": [v(14.34, 44.74) * mm, v(13.53, 44.85) * mm, v(13.46, 44.83) * mm, v(13.32, 44.47) * mm]});
            skFitSpline(sketch, "E1760", {"points": [v(13.32, 44.47) * mm, v(13.23, 44.26) * mm, v(12.43, 37.3) * mm, v(11.55, 29) * mm]});
            skFitSpline(sketch, "E1761", {"points": [v(11.55, 29) * mm, v(10.46, 18.83) * mm, v(9.86, 13.8) * mm, v(9.7, 13.55) * mm]});
            skFitSpline(sketch, "E1762", {"points": [v(9.7, 13.55) * mm, v(9.58, 13.35) * mm, v(9.34, 13.15) * mm, v(9.17, 13.1) * mm]});
            skFitSpline(sketch, "E1763", {"points": [v(9.17, 13.1) * mm, v(9, 13.04) * mm, v(6.86, 12.7) * mm, v(4.41, 12.34) * mm]});
            skLineSegment(sketch, "E1764", {"start": v(23.23, -1.01) * mm, "end": v(26.38, 0.46) * mm});
            skLineSegment(sketch, "E1765", {"start": v(26.38, 0.46) * mm, "end": v(26.32, 1.02) * mm});
            skFitSpline(sketch, "E1766", {"points": [v(-4.5, 12.34) * mm, v(-6.94, 12.7) * mm, v(-9.12, 13.07) * mm, v(-9.33, 13.16) * mm]});
            skFitSpline(sketch, "E1767", {"points": [v(-9.33, 13.16) * mm, v(-9.53, 13.25) * mm, v(-9.78, 13.5) * mm, v(-9.86, 13.7) * mm]});
            skFitSpline(sketch, "E1768", {"points": [v(-9.86, 13.7) * mm, v(-9.95, 13.91) * mm, v(-10.74, 20.83) * mm, v(-11.62, 29.08) * mm]});
            skFitSpline(sketch, "E1769", {"points": [v(-11.62, 29.08) * mm, v(-12.5, 37.33) * mm, v(-13.3, 44.26) * mm, v(-13.38, 44.47) * mm]});
            skFitSpline(sketch, "E1770", {"points": [v(-13.38, 44.47) * mm, v(-13.53, 44.83) * mm, v(-13.6, 44.86) * mm, v(-14.33, 44.76) * mm]});
            skFitSpline(sketch, "E1771", {"points": [v(-14.33, 44.76) * mm, v(-16.45, 44.46) * mm, v(-19.57, 43.57) * mm, v(-21.92, 42.6) * mm]});
            skFitSpline(sketch, "E1772", {"points": [v(-21.92, 42.6) * mm, v(-24.21, 41.65) * mm, v(-30.04, 38.68) * mm, v(-30.14, 38.4) * mm]});
            skFitSpline(sketch, "E1773", {"points": [v(-30.14, 38.4) * mm, v(-30.2, 38.27) * mm, v(-29.93, 37.1) * mm, v(-29.55, 35.79) * mm]});
            skFitSpline(sketch, "E1774", {"points": [v(-29.55, 35.79) * mm, v(-28, 30.43) * mm, v(-26.97, 25.2) * mm, v(-26.45, 20.16) * mm]});
            skFitSpline(sketch, "E1775", {"points": [v(-26.45, 20.16) * mm, v(-26.23, 18.06) * mm, v(-26.2, 16.1) * mm, v(-26.26, 9.58) * mm]});
            skFitSpline(sketch, "E1776", {"points": [v(-26.26, 9.58) * mm, v(-26.3, 5.18) * mm, v(-26.36, 1.33) * mm, v(-26.39, 1.03) * mm]});
            skLineSegment(sketch, "E1777", {"start": v(4.41, 12.34) * mm, "end": v(-0.03, 11.69) * mm});
            skLineSegment(sketch, "E1778", {"start": v(-0.03, 11.69) * mm, "end": v(-4.5, 12.34) * mm});
            skFitSpline(sketch, "E1779", {"points": [v(-23.7, -0.82) * mm, v(-19.39, -2.83) * mm, v(-16.74, -4.16) * mm, v(-12.7, -6.34) * mm]});
            skFitSpline(sketch, "E1780", {"points": [v(-12.7, -6.34) * mm, v(-10.64, -7.46) * mm, v(-8.54, -8.58) * mm, v(-8.03, -8.85) * mm]});
            skFitSpline(sketch, "E1781", {"points": [v(-8.03, -8.85) * mm, v(-7.04, -9.37) * mm, v(-5.63, -9.77) * mm, v(-3.99, -10) * mm]});
            skFitSpline(sketch, "E1782", {"points": [v(-3.99, -10) * mm, v(-2.6, -10.2) * mm, v(4, -10.07) * mm, v(5.05, -9.83) * mm]});
            skLineSegment(sketch, "E1783", {"start": v(-26.39, 1.03) * mm, "end": v(-26.45, 0.47) * mm});
            skLineSegment(sketch, "E1784", {"start": v(-26.45, 0.47) * mm, "end": v(-23.7, -0.82) * mm});
            skFitSpline(sketch, "E1785", {"points": [v(-34.53, -3.85) * mm, v(-34.44, -3.49) * mm, v(-33.95, -1.6) * mm, v(-33.45, 0.36) * mm]});
            skFitSpline(sketch, "E1786", {"points": [v(-32.02, 39.73) * mm, v(-31.31, 40.33) * mm, v(-24.35, 43.8) * mm, v(-22.02, 44.72) * mm]});
            skFitSpline(sketch, "E1787", {"points": [v(-22.02, 44.72) * mm, v(-18.5, 46.1) * mm, v(-13.2, 47.24) * mm, v(-12.12, 46.83) * mm]});
            skFitSpline(sketch, "E1788", {"points": [v(-12.12, 46.83) * mm, v(-11.56, 46.62) * mm, v(-11.46, 46.29) * mm, v(-11.22, 44) * mm]});
            skFitSpline(sketch, "E1789", {"points": [v(-11.22, 44) * mm, v(-11.1, 42.96) * mm, v(-10.98, 42.04) * mm, v(-10.93, 41.97) * mm]});
            skFitSpline(sketch, "E1790", {"points": [v(-10.93, 41.97) * mm, v(-10.81, 41.77) * mm, v(10.76, 41.8) * mm, v(10.88, 41.99) * mm]});
            skFitSpline(sketch, "E1791", {"points": [v(10.88, 41.99) * mm, v(10.93, 42.07) * mm, v(11.06, 43) * mm, v(11.16, 44.03) * mm]});
            skFitSpline(sketch, "E1792", {"points": [v(11.16, 44.03) * mm, v(11.38, 46.27) * mm, v(11.5, 46.62) * mm, v(12.04, 46.83) * mm]});
            skFitSpline(sketch, "E1793", {"points": [v(12.04, 46.83) * mm, v(13.12, 47.24) * mm, v(18.4, 46.12) * mm, v(21.9, 44.74) * mm]});
            skFitSpline(sketch, "E1794", {"points": [v(21.9, 44.74) * mm, v(24.34, 43.77) * mm, v(31.21, 40.36) * mm, v(31.94, 39.75) * mm]});
            skLineSegment(sketch, "E1795", {"start": v(-33.45, 0.36) * mm, "end": v(-32.53, 3.92) * mm});
            skLineSegment(sketch, "E1796", {"start": v(-32.53, 3.92) * mm, "end": v(-32.53, 21.6) * mm});
            skLineSegment(sketch, "E1797", {"start": v(-32.53, 21.6) * mm, "end": v(-32.53, 39.3) * mm});
            skLineSegment(sketch, "E1798", {"start": v(-32.53, 39.3) * mm, "end": v(-32.02, 39.73) * mm});
            skFitSpline(sketch, "E1799", {"points": [v(33.4, 0.43) * mm, v(33.9, -1.6) * mm, v(34.4, -3.53) * mm, v(34.48, -3.88) * mm]});
            skFitSpline(sketch, "E1800", {"points": [v(34.48, -3.88) * mm, v(34.57, -4.23) * mm, v(34.75, -4.5) * mm, v(34.89, -4.5) * mm]});
            skFitSpline(sketch, "E1801", {"points": [v(34.89, -4.5) * mm, v(35.76, -4.5) * mm, v(37.4, 1.46) * mm, v(38.06, 7.08) * mm]});
            skFitSpline(sketch, "E1802", {"points": [v(38.06, 7.08) * mm, v(38.4, 9.88) * mm, v(38.43, 14.24) * mm, v(38.14, 16.08) * mm]});
            skFitSpline(sketch, "E1803", {"points": [v(38.14, 16.08) * mm, v(37.68, 19.05) * mm, v(36.52, 21.64) * mm, v(35.08, 22.95) * mm]});
            skLineSegment(sketch, "E1804", {"start": v(31.94, 39.75) * mm, "end": v(32.47, 39.3) * mm});
            skLineSegment(sketch, "E1805", {"start": v(32.47, 39.3) * mm, "end": v(32.47, 21.7) * mm});
            skLineSegment(sketch, "E1806", {"start": v(32.47, 21.7) * mm, "end": v(32.47, 4.1) * mm});
            skLineSegment(sketch, "E1807", {"start": v(32.47, 4.1) * mm, "end": v(33.4, 0.43) * mm});
            skFitSpline(sketch, "E1808", {"points": [v(34.4, 25.44) * mm, v(34.35, 26.53) * mm, v(34.22, 31.05) * mm, v(34.12, 35.5) * mm]});
            skFitSpline(sketch, "E1809", {"points": [v(34.12, 35.5) * mm, v(34.03, 39.94) * mm, v(33.87, 44.1) * mm, v(33.78, 44.73) * mm]});
            skFitSpline(sketch, "E1810", {"points": [v(33.78, 44.73) * mm, v(33.46, 47) * mm, v(32.18, 49.59) * mm, v(30.25, 51.85) * mm]});
            skFitSpline(sketch, "E1811", {"points": [v(30.25, 51.85) * mm, v(26.4, 56.35) * mm, v(19.56, 59.87) * mm, v(11.38, 61.55) * mm]});
            skFitSpline(sketch, "E1812", {"points": [v(11.38, 61.55) * mm, v(7.19, 62.42) * mm, v(5.41, 62.58) * mm, v(-0.03, 62.58) * mm]});
            skFitSpline(sketch, "E1813", {"points": [v(-0.03, 62.58) * mm, v(-5.48, 62.58) * mm, v(-7.25, 62.42) * mm, v(-11.45, 61.55) * mm]});
            skFitSpline(sketch, "E1814", {"points": [v(-11.45, 61.55) * mm, v(-23.1, 59.15) * mm, v(-31.59, 53.16) * mm, v(-33.61, 45.9) * mm]});
            skFitSpline(sketch, "E1815", {"points": [v(-33.61, 45.9) * mm, v(-33.84, 45.09) * mm, v(-33.94, 43.03) * mm, v(-34.2, 34.3) * mm]});
            skFitSpline(sketch, "E1816", {"points": [v(-34.2, 34.3) * mm, v(-34.35, 28.47) * mm, v(-34.55, 23.6) * mm, v(-34.63, 23.48) * mm]});
            skFitSpline(sketch, "E1817", {"points": [v(-34.63, 23.48) * mm, v(-34.7, 23.35) * mm, v(-34.97, 23.08) * mm, v(-35.22, 22.87) * mm]});
            skFitSpline(sketch, "E1818", {"points": [v(-35.22, 22.87) * mm, v(-36.43, 21.85) * mm, v(-37.64, 19.2) * mm, v(-38.13, 16.54) * mm]});
            skFitSpline(sketch, "E1819", {"points": [v(-38.13, 16.54) * mm, v(-39.01, 11.62) * mm, v(-37.73, 1.04) * mm, v(-35.7, -3.42) * mm]});
            skFitSpline(sketch, "E1820", {"points": [v(-35.7, -3.42) * mm, v(-35.14, -4.68) * mm, v(-34.8, -4.8) * mm, v(-34.53, -3.85) * mm]});
            skLineSegment(sketch, "E1821", {"start": v(35.08, 22.95) * mm, "end": v(34.5, 23.47) * mm});
            skLineSegment(sketch, "E1822", {"start": v(34.5, 23.47) * mm, "end": v(34.4, 25.44) * mm});
            skFitSpline(sketch, "E1823", {"points": [v(4.22, 14.34) * mm, v(6.62, 14.68) * mm, v(7.77, 14.91) * mm, v(7.9, 15.08) * mm]});
            skFitSpline(sketch, "E1824", {"points": [v(7.9, 15.08) * mm, v(8, 15.21) * mm, v(8.23, 16.77) * mm, v(8.42, 18.53) * mm]});
            skFitSpline(sketch, "E1825", {"points": [v(8.42, 18.53) * mm, v(10.71, 39.73) * mm, v(10.7, 39.52) * mm, v(10.45, 39.68) * mm]});
            skFitSpline(sketch, "E1826", {"points": [v(10.45, 39.68) * mm, v(10.15, 39.87) * mm, v(-10.2, 39.87) * mm, v(-10.51, 39.68) * mm]});
            skFitSpline(sketch, "E1827", {"points": [v(-10.51, 39.68) * mm, v(-10.7, 39.55) * mm, v(-10.54, 37.62) * mm, v(-9.47, 27.56) * mm]});
            skFitSpline(sketch, "E1828", {"points": [v(-9.47, 27.56) * mm, v(-8.76, 20.97) * mm, v(-8.12, 15.42) * mm, v(-8.03, 15.22) * mm]});
            skFitSpline(sketch, "E1829", {"points": [v(-8.03, 15.22) * mm, v(-7.92, 14.95) * mm, v(-7.69, 14.83) * mm, v(-7.17, 14.75) * mm]});
            skFitSpline(sketch, "E1830", {"points": [v(-7.17, 14.75) * mm, v(-2.05, 13.99) * mm, v(-0.05, 13.73) * mm, v(0.3, 13.78) * mm]});
            skFitSpline(sketch, "E1831", {"points": [v(0.3, 13.78) * mm, v(0.53, 13.81) * mm, v(2.3, 14.06) * mm, v(4.22, 14.34) * mm]});
            skSolve(sketch);
        }
        {
            var Q0;
            {var subQ111=sQuery(id+"F0.wireOp",EDGE,"E1312");Q0=makeQuery(id+"F0.imprint","IMPRINT",FACE,{"disambiguationData":[TD([[makeQuery(id+"F0.imprint","IMPRINT",EDGE,{"derivedFrom":subQ111}),-1.0]])]});}
            extrude(context, id + "F1", {"entities" : qUnion([Q0]), "flatOperationType" : FlatOperationType.REMOVE, "depth" : 2 * mm, "offsetDistance" : 25 * mm, "domain" : OperationDomain.MODEL});
        }
    });
